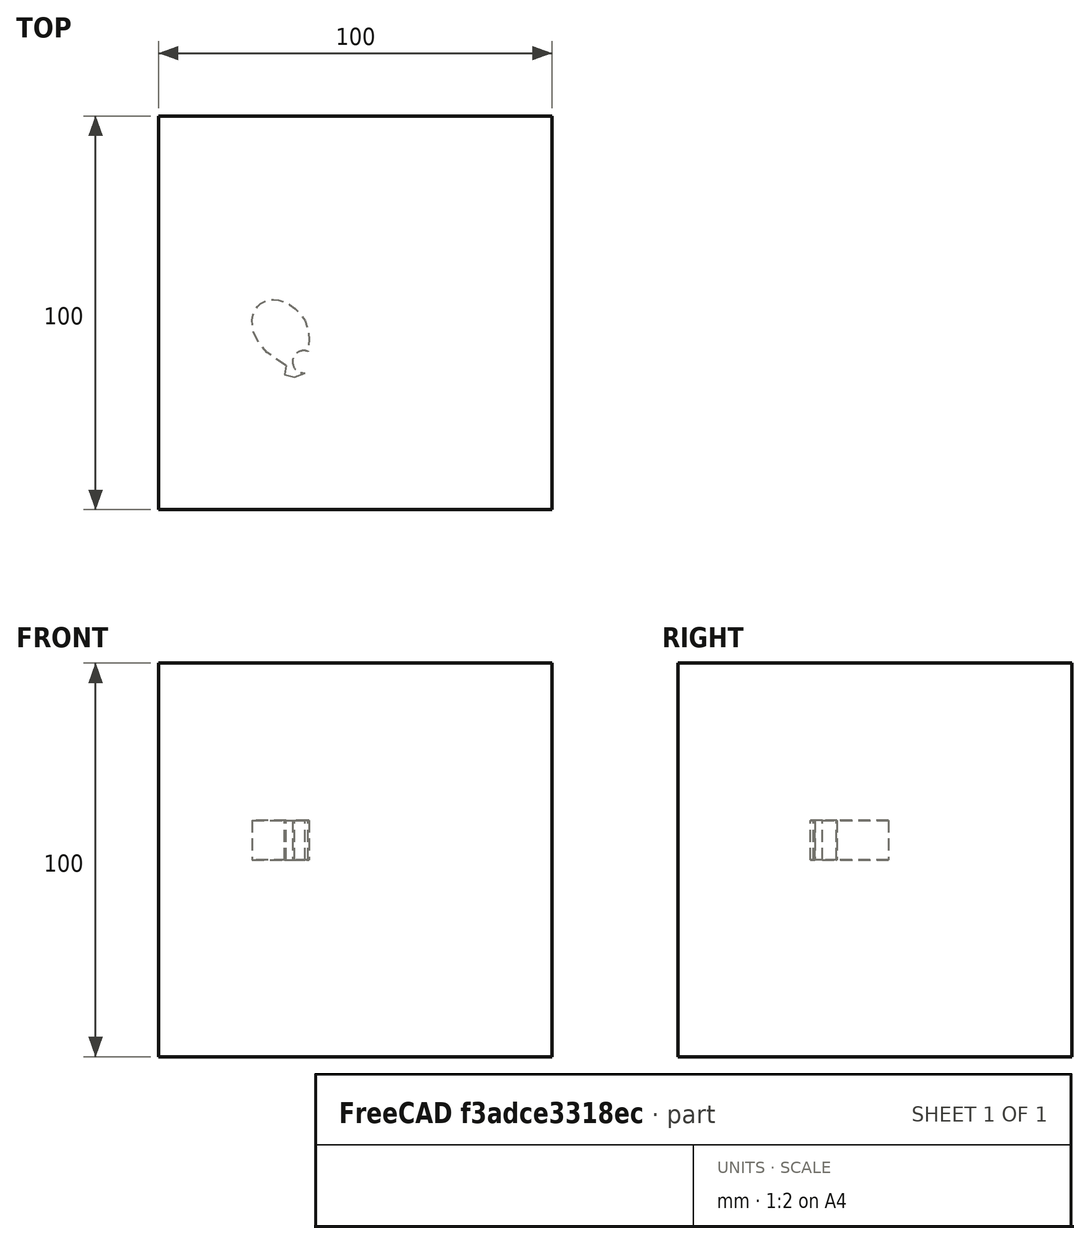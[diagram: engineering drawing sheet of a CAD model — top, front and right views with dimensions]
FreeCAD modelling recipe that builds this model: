
FCSTD DOCUMENT  (FreeCAD 0.19RUnknown)
Label: mirrorTest-3c
License: All rights reserved
LicenseURL: http://en.wikipedia.org/wiki/All_rights_reserved
objects: App::DocumentObjectGroupPython×1248, Part::Mirroring×2, App::Part×2, Part::FeaturePython×1, Sketcher::SketchObject×1, Part::Extrusion×1
note: 5 computed .brp shape members not serialized (recipe doc carries the construction recipe); baked Part::Feature solids carry a one-line shape summary decoded from their .brp

FEATURE [App::DocumentObjectGroupPython] HALFPI  # scripted group (container) (typed FeaturePython)
  name = HALFPI
  value = pi/2.
FEATURE [App::DocumentObjectGroupPython] PI  # scripted group (container) (typed FeaturePython)
  name = PI
  value = 1.*pi
FEATURE [App::DocumentObjectGroupPython] TWOPI  # scripted group (container) (typed FeaturePython)
  name = TWOPI
  value = 2.*pi
FEATURE [App::DocumentObjectGroupPython] Constants  # scripted group (container) (typed FeaturePython)
  Group = -> [HALFPI,PI,TWOPI]
FEATURE [App::DocumentObjectGroupPython] Variables  # scripted group (container) (typed FeaturePython)
FEATURE [App::DocumentObjectGroupPython] Quantities  # scripted group (container) (typed FeaturePython)
FEATURE [App::DocumentObjectGroupPython] Isotopes  # scripted group (container) (typed FeaturePython)
FEATURE [App::DocumentObjectGroupPython] Elements  # scripted group (container) (typed FeaturePython)
FEATURE [App::DocumentObjectGroupPython] G4Isotopes  # scripted group (container) (typed FeaturePython)
FEATURE [App::DocumentObjectGroupPython] H_element  # scripted group (container) (typed FeaturePython)
  Z = 1
  atom_value = 1.008
  formula = H
  name = H_element
FEATURE [App::DocumentObjectGroupPython] He_element  # scripted group (container) (typed FeaturePython)
  Z = 2
  atom_value = 4.0026
  formula = He
  name = He_element
FEATURE [App::DocumentObjectGroupPython] Li_element  # scripted group (container) (typed FeaturePython)
  Z = 3
  atom_value = 6.94
  formula = Li
  name = Li_element
FEATURE [App::DocumentObjectGroupPython] Be_element  # scripted group (container) (typed FeaturePython)
  Z = 4
  atom_value = 9.01218
  formula = Be
  name = Be_element
FEATURE [App::DocumentObjectGroupPython] B_element  # scripted group (container) (typed FeaturePython)
  Z = 5
  atom_value = 10.81
  formula = B
  name = B_element
FEATURE [App::DocumentObjectGroupPython] C_element  # scripted group (container) (typed FeaturePython)
  Z = 6
  atom_value = 12.011
  formula = C
  name = C_element
FEATURE [App::DocumentObjectGroupPython] N_element  # scripted group (container) (typed FeaturePython)
  Z = 7
  atom_value = 14.007
  formula = N
  name = N_element
FEATURE [App::DocumentObjectGroupPython] O_element  # scripted group (container) (typed FeaturePython)
  Z = 8
  atom_value = 15.999
  formula = O
  name = O_element
FEATURE [App::DocumentObjectGroupPython] F_element  # scripted group (container) (typed FeaturePython)
  Z = 9
  atom_value = 18.9984
  formula = F
  name = F_element
FEATURE [App::DocumentObjectGroupPython] Ne_element  # scripted group (container) (typed FeaturePython)
  Z = 10
  atom_value = 20.1797
  formula = Ne
  name = Ne_element
FEATURE [App::DocumentObjectGroupPython] Na_element  # scripted group (container) (typed FeaturePython)
  Z = 11
  atom_value = 22.9898
  formula = Na
  name = Na_element
FEATURE [App::DocumentObjectGroupPython] Mg_element  # scripted group (container) (typed FeaturePython)
  Z = 12
  atom_value = 24.305
  formula = Mg
  name = Mg_element
FEATURE [App::DocumentObjectGroupPython] Al_element  # scripted group (container) (typed FeaturePython)
  Z = 13
  atom_value = 26.9815
  formula = Al
  name = Al_element
FEATURE [App::DocumentObjectGroupPython] Si_element  # scripted group (container) (typed FeaturePython)
  Z = 14
  atom_value = 28.085
  formula = Si
  name = Si_element
FEATURE [App::DocumentObjectGroupPython] P_element  # scripted group (container) (typed FeaturePython)
  Z = 15
  atom_value = 30.9738
  formula = P
  name = P_element
FEATURE [App::DocumentObjectGroupPython] S_element  # scripted group (container) (typed FeaturePython)
  Z = 16
  atom_value = 32.06
  formula = S
  name = S_element
FEATURE [App::DocumentObjectGroupPython] Cl_element  # scripted group (container) (typed FeaturePython)
  Z = 17
  atom_value = 35.45
  formula = Cl
  name = Cl_element
FEATURE [App::DocumentObjectGroupPython] Ar_element  # scripted group (container) (typed FeaturePython)
  Z = 18
  atom_value = 39.95
  formula = Ar
  name = Ar_element
FEATURE [App::DocumentObjectGroupPython] K_element  # scripted group (container) (typed FeaturePython)
  Z = 19
  atom_value = 39.0983
  formula = K
  name = K_element
FEATURE [App::DocumentObjectGroupPython] Ca_element  # scripted group (container) (typed FeaturePython)
  Z = 20
  atom_value = 40.078
  formula = Ca
  name = Ca_element
FEATURE [App::DocumentObjectGroupPython] Sc_element  # scripted group (container) (typed FeaturePython)
  Z = 21
  atom_value = 44.9559
  formula = Sc
  name = Sc_element
FEATURE [App::DocumentObjectGroupPython] Ti_element  # scripted group (container) (typed FeaturePython)
  Z = 22
  atom_value = 47.867
  formula = Ti
  name = Ti_element
FEATURE [App::DocumentObjectGroupPython] V_element  # scripted group (container) (typed FeaturePython)
  Z = 23
  atom_value = 50.9415
  formula = V
  name = V_element
FEATURE [App::DocumentObjectGroupPython] Cr_element  # scripted group (container) (typed FeaturePython)
  Z = 24
  atom_value = 51.9961
  formula = Cr
  name = Cr_element
FEATURE [App::DocumentObjectGroupPython] Mn_element  # scripted group (container) (typed FeaturePython)
  Z = 25
  atom_value = 54.938
  formula = Mn
  name = Mn_element
FEATURE [App::DocumentObjectGroupPython] Fe_element  # scripted group (container) (typed FeaturePython)
  Z = 26
  atom_value = 55.845
  formula = Fe
  name = Fe_element
FEATURE [App::DocumentObjectGroupPython] Co_element  # scripted group (container) (typed FeaturePython)
  Z = 27
  atom_value = 58.9332
  formula = Co
  name = Co_element
FEATURE [App::DocumentObjectGroupPython] Ni_element  # scripted group (container) (typed FeaturePython)
  Z = 28
  atom_value = 58.6934
  formula = Ni
  name = Ni_element
FEATURE [App::DocumentObjectGroupPython] Cu_element  # scripted group (container) (typed FeaturePython)
  Z = 29
  atom_value = 63.546
  formula = Cu
  name = Cu_element
FEATURE [App::DocumentObjectGroupPython] Zn_element  # scripted group (container) (typed FeaturePython)
  Z = 30
  atom_value = 65.38
  formula = Zn
  name = Zn_element
FEATURE [App::DocumentObjectGroupPython] Ga_element  # scripted group (container) (typed FeaturePython)
  Z = 31
  atom_value = 69.723
  formula = Ga
  name = Ga_element
FEATURE [App::DocumentObjectGroupPython] Ge_element  # scripted group (container) (typed FeaturePython)
  Z = 32
  atom_value = 72.63
  formula = Ge
  name = Ge_element
FEATURE [App::DocumentObjectGroupPython] As_element  # scripted group (container) (typed FeaturePython)
  Z = 33
  atom_value = 74.9216
  formula = As
  name = As_element
FEATURE [App::DocumentObjectGroupPython] Se_element  # scripted group (container) (typed FeaturePython)
  Z = 34
  atom_value = 78.971
  formula = Se
  name = Se_element
FEATURE [App::DocumentObjectGroupPython] Br_element  # scripted group (container) (typed FeaturePython)
  Z = 35
  atom_value = 79.904
  formula = Br
  name = Br_element
FEATURE [App::DocumentObjectGroupPython] Kr_element  # scripted group (container) (typed FeaturePython)
  Z = 36
  atom_value = 83.798
  formula = Kr
  name = Kr_element
FEATURE [App::DocumentObjectGroupPython] Rb_element  # scripted group (container) (typed FeaturePython)
  Z = 37
  atom_value = 85.4678
  formula = Rb
  name = Rb_element
FEATURE [App::DocumentObjectGroupPython] Sr_element  # scripted group (container) (typed FeaturePython)
  Z = 38
  atom_value = 87.62
  formula = Sr
  name = Sr_element
FEATURE [App::DocumentObjectGroupPython] Y_element  # scripted group (container) (typed FeaturePython)
  Z = 39
  atom_value = 88.9058
  formula = Y
  name = Y_element
FEATURE [App::DocumentObjectGroupPython] Zr_element  # scripted group (container) (typed FeaturePython)
  Z = 40
  atom_value = 91.224
  formula = Zr
  name = Zr_element
FEATURE [App::DocumentObjectGroupPython] Nb_element  # scripted group (container) (typed FeaturePython)
  Z = 41
  atom_value = 92.9064
  formula = Nb
  name = Nb_element
FEATURE [App::DocumentObjectGroupPython] Mo_element  # scripted group (container) (typed FeaturePython)
  Z = 42
  atom_value = 95.95
  formula = Mo
  name = Mo_element
FEATURE [App::DocumentObjectGroupPython] Tc_element  # scripted group (container) (typed FeaturePython)
  Z = 43
  atom_value = 97
  formula = Tc
  name = Tc_element
FEATURE [App::DocumentObjectGroupPython] Ru_element  # scripted group (container) (typed FeaturePython)
  Z = 44
  atom_value = 101.07
  formula = Ru
  name = Ru_element
FEATURE [App::DocumentObjectGroupPython] Rh_element  # scripted group (container) (typed FeaturePython)
  Z = 45
  atom_value = 102.905
  formula = Rh
  name = Rh_element
FEATURE [App::DocumentObjectGroupPython] Pd_element  # scripted group (container) (typed FeaturePython)
  Z = 46
  atom_value = 106.42
  formula = Pd
  name = Pd_element
FEATURE [App::DocumentObjectGroupPython] Ag_element  # scripted group (container) (typed FeaturePython)
  Z = 47
  atom_value = 107.868
  formula = Ag
  name = Ag_element
FEATURE [App::DocumentObjectGroupPython] Cd_element  # scripted group (container) (typed FeaturePython)
  Z = 48
  atom_value = 112.414
  formula = Cd
  name = Cd_element
FEATURE [App::DocumentObjectGroupPython] In_element  # scripted group (container) (typed FeaturePython)
  Z = 49
  atom_value = 114.818
  formula = In
  name = In_element
FEATURE [App::DocumentObjectGroupPython] Sn_element  # scripted group (container) (typed FeaturePython)
  Z = 50
  atom_value = 118.71
  formula = Sn
  name = Sn_element
FEATURE [App::DocumentObjectGroupPython] Sb_element  # scripted group (container) (typed FeaturePython)
  Z = 51
  atom_value = 121.76
  formula = Sb
  name = Sb_element
FEATURE [App::DocumentObjectGroupPython] Te_element  # scripted group (container) (typed FeaturePython)
  Z = 52
  atom_value = 127.6
  formula = Te
  name = Te_element
FEATURE [App::DocumentObjectGroupPython] I_element  # scripted group (container) (typed FeaturePython)
  Z = 53
  atom_value = 126.904
  formula = I
  name = I_element
FEATURE [App::DocumentObjectGroupPython] Xe_element  # scripted group (container) (typed FeaturePython)
  Z = 54
  atom_value = 131.293
  formula = Xe
  name = Xe_element
FEATURE [App::DocumentObjectGroupPython] Cs_element  # scripted group (container) (typed FeaturePython)
  Z = 55
  atom_value = 132.905
  formula = Cs
  name = Cs_element
FEATURE [App::DocumentObjectGroupPython] Ba_element  # scripted group (container) (typed FeaturePython)
  Z = 56
  atom_value = 137.327
  formula = Ba
  name = Ba_element
FEATURE [App::DocumentObjectGroupPython] La_element  # scripted group (container) (typed FeaturePython)
  Z = 57
  atom_value = 138.905
  formula = La
  name = La_element
FEATURE [App::DocumentObjectGroupPython] Ce_element  # scripted group (container) (typed FeaturePython)
  Z = 58
  atom_value = 140.116
  formula = Ce
  name = Ce_element
FEATURE [App::DocumentObjectGroupPython] Pr_element  # scripted group (container) (typed FeaturePython)
  Z = 59
  atom_value = 140.908
  formula = Pr
  name = Pr_element
FEATURE [App::DocumentObjectGroupPython] Nd_element  # scripted group (container) (typed FeaturePython)
  Z = 60
  atom_value = 144.242
  formula = Nd
  name = Nd_element
FEATURE [App::DocumentObjectGroupPython] Pm_element  # scripted group (container) (typed FeaturePython)
  Z = 61
  atom_value = 145
  formula = Pm
  name = Pm_element
FEATURE [App::DocumentObjectGroupPython] Sm_element  # scripted group (container) (typed FeaturePython)
  Z = 62
  atom_value = 150.36
  formula = Sm
  name = Sm_element
FEATURE [App::DocumentObjectGroupPython] Eu_element  # scripted group (container) (typed FeaturePython)
  Z = 63
  atom_value = 151.964
  formula = Eu
  name = Eu_element
FEATURE [App::DocumentObjectGroupPython] Gd_element  # scripted group (container) (typed FeaturePython)
  Z = 64
  atom_value = 157.25
  formula = Gd
  name = Gd_element
FEATURE [App::DocumentObjectGroupPython] Tb_element  # scripted group (container) (typed FeaturePython)
  Z = 65
  atom_value = 158.925
  formula = Tb
  name = Tb_element
FEATURE [App::DocumentObjectGroupPython] Dy_element  # scripted group (container) (typed FeaturePython)
  Z = 66
  atom_value = 162.5
  formula = Dy
  name = Dy_element
FEATURE [App::DocumentObjectGroupPython] Ho_element  # scripted group (container) (typed FeaturePython)
  Z = 67
  atom_value = 164.93
  formula = Ho
  name = Ho_element
FEATURE [App::DocumentObjectGroupPython] Er_element  # scripted group (container) (typed FeaturePython)
  Z = 68
  atom_value = 167.259
  formula = Er
  name = Er_element
FEATURE [App::DocumentObjectGroupPython] Tm_element  # scripted group (container) (typed FeaturePython)
  Z = 69
  atom_value = 168.934
  formula = Tm
  name = Tm_element
FEATURE [App::DocumentObjectGroupPython] Yb_element  # scripted group (container) (typed FeaturePython)
  Z = 70
  atom_value = 173.045
  formula = Yb
  name = Yb_element
FEATURE [App::DocumentObjectGroupPython] Lu_element  # scripted group (container) (typed FeaturePython)
  Z = 71
  atom_value = 174.967
  formula = Lu
  name = Lu_element
FEATURE [App::DocumentObjectGroupPython] Hf_element  # scripted group (container) (typed FeaturePython)
  Z = 72
  atom_value = 178.49
  formula = Hf
  name = Hf_element
FEATURE [App::DocumentObjectGroupPython] Ta_element  # scripted group (container) (typed FeaturePython)
  Z = 73
  atom_value = 180.948
  formula = Ta
  name = Ta_element
FEATURE [App::DocumentObjectGroupPython] W_element  # scripted group (container) (typed FeaturePython)
  Z = 74
  atom_value = 183.84
  formula = W
  name = W_element
FEATURE [App::DocumentObjectGroupPython] Re_element  # scripted group (container) (typed FeaturePython)
  Z = 75
  atom_value = 186.207
  formula = Re
  name = Re_element
FEATURE [App::DocumentObjectGroupPython] Os_element  # scripted group (container) (typed FeaturePython)
  Z = 76
  atom_value = 190.23
  formula = Os
  name = Os_element
FEATURE [App::DocumentObjectGroupPython] Ir_element  # scripted group (container) (typed FeaturePython)
  Z = 77
  atom_value = 192.217
  formula = Ir
  name = Ir_element
FEATURE [App::DocumentObjectGroupPython] Pt_element  # scripted group (container) (typed FeaturePython)
  Z = 78
  atom_value = 195.084
  formula = Pt
  name = Pt_element
FEATURE [App::DocumentObjectGroupPython] Au_element  # scripted group (container) (typed FeaturePython)
  Z = 79
  atom_value = 196.967
  formula = Au
  name = Au_element
FEATURE [App::DocumentObjectGroupPython] Hg_element  # scripted group (container) (typed FeaturePython)
  Z = 80
  atom_value = 200.592
  formula = Hg
  name = Hg_element
FEATURE [App::DocumentObjectGroupPython] Tl_element  # scripted group (container) (typed FeaturePython)
  Z = 81
  atom_value = 204.38
  formula = Tl
  name = Tl_element
FEATURE [App::DocumentObjectGroupPython] Pb_element  # scripted group (container) (typed FeaturePython)
  Z = 82
  atom_value = 207.2
  formula = Pb
  name = Pb_element
FEATURE [App::DocumentObjectGroupPython] Bi_element  # scripted group (container) (typed FeaturePython)
  Z = 83
  atom_value = 208.98
  formula = Bi
  name = Bi_element
FEATURE [App::DocumentObjectGroupPython] Po_element  # scripted group (container) (typed FeaturePython)
  Z = 84
  atom_value = 209
  formula = Po
  name = Po_element
FEATURE [App::DocumentObjectGroupPython] At_element  # scripted group (container) (typed FeaturePython)
  Z = 85
  atom_value = 210
  formula = At
  name = At_element
FEATURE [App::DocumentObjectGroupPython] Rn_element  # scripted group (container) (typed FeaturePython)
  Z = 86
  atom_value = 222
  formula = Rn
  name = Rn_element
FEATURE [App::DocumentObjectGroupPython] Fr_element  # scripted group (container) (typed FeaturePython)
  Z = 87
  atom_value = 223
  formula = Fr
  name = Fr_element
FEATURE [App::DocumentObjectGroupPython] Ra_element  # scripted group (container) (typed FeaturePython)
  Z = 88
  atom_value = 226
  formula = Ra
  name = Ra_element
FEATURE [App::DocumentObjectGroupPython] Ac_element  # scripted group (container) (typed FeaturePython)
  Z = 89
  atom_value = 227
  formula = Ac
  name = Ac_element
FEATURE [App::DocumentObjectGroupPython] Th_element  # scripted group (container) (typed FeaturePython)
  Z = 90
  atom_value = 232.038
  formula = Th
  name = Th_element
FEATURE [App::DocumentObjectGroupPython] Pa_element  # scripted group (container) (typed FeaturePython)
  Z = 91
  atom_value = 231.036
  formula = Pa
  name = Pa_element
FEATURE [App::DocumentObjectGroupPython] U_element  # scripted group (container) (typed FeaturePython)
  Z = 92
  atom_value = 238.029
  formula = U
  name = U_element
FEATURE [App::DocumentObjectGroupPython] Np_element  # scripted group (container) (typed FeaturePython)
  Z = 93
  atom_value = 237
  formula = Np
  name = Np_element
FEATURE [App::DocumentObjectGroupPython] Pu_element  # scripted group (container) (typed FeaturePython)
  Z = 94
  atom_value = 244
  formula = Pu
  name = Pu_element
FEATURE [App::DocumentObjectGroupPython] Am_element  # scripted group (container) (typed FeaturePython)
  Z = 95
  atom_value = 243
  formula = Am
  name = Am_element
FEATURE [App::DocumentObjectGroupPython] Cm_element  # scripted group (container) (typed FeaturePython)
  Z = 96
  atom_value = 247
  formula = Cm
  name = Cm_element
FEATURE [App::DocumentObjectGroupPython] Bk_element  # scripted group (container) (typed FeaturePython)
  Z = 97
  atom_value = 247
  formula = Bk
  name = Bk_element
FEATURE [App::DocumentObjectGroupPython] Cf_element  # scripted group (container) (typed FeaturePython)
  Z = 98
  atom_value = 251
  formula = Cf
  name = Cf_element
FEATURE [App::DocumentObjectGroupPython] G4Elements  # scripted group (container) (typed FeaturePython)
  Group = -> [H_element,He_element,Li_element,Be_element,B_element,C_element,N_element,O_element,F_element,Ne_element,Na_element,Mg_element,Al_element,Si_element,P_element,S_element,Cl_element,Ar_element,K_element,Ca_element,Sc_element,Ti_element,V_element,Cr_element,Mn_element,Fe_element,Co_element,Ni_element,Cu_element,Zn_element,Ga_element,Ge_element,As_element,Se_element,Br_element,Kr_element,Rb_element,+61 more]
FEATURE [App::DocumentObjectGroupPython] H_element001  label="H_element : 0.101"  # scripted group (container) (typed FeaturePython)
  n = 0.101327
FEATURE [App::DocumentObjectGroupPython] C_element001  label="C_element : 0.775"  # scripted group (container) (typed FeaturePython)
  n = 0.7755
FEATURE [App::DocumentObjectGroupPython] N_element001  label="N_element : 0.035"  # scripted group (container) (typed FeaturePython)
  n = 0.035057
FEATURE [App::DocumentObjectGroupPython] O_element001  label="O_element : 0.052"  # scripted group (container) (typed FeaturePython)
  n = 0.0523159
FEATURE [App::DocumentObjectGroupPython] F_element001  label="F_element : 0.017"  # scripted group (container) (typed FeaturePython)
  n = 0.017422
FEATURE [App::DocumentObjectGroupPython] Ca_element001  label="Ca_element : 0.018"  # scripted group (container) (typed FeaturePython)
  n = 0.018378
FEATURE [App::DocumentObjectGroupPython] G4_A_150_TISSUE  label="G4_A-150_TISSUE"  # scripted group (container) (typed FeaturePython)
  Dunit = g/cm3
  Dvalue = 1.127
  Group = -> [H_element001,C_element001,N_element001,O_element001,F_element001,Ca_element001]
  conduct = 2
  density = 1
  expand = 3
  formula = G4_A-150_TISSUE
  name = G4_A-150_TISSUE
  specific = 4
FEATURE [App::DocumentObjectGroupPython] C_element002  label="C_element : 3"  # scripted group (container) (typed FeaturePython)
  n = 3
  ref = C_element
FEATURE [App::DocumentObjectGroupPython] H_element002  label="H_element : 6"  # scripted group (container) (typed FeaturePython)
  n = 6
  ref = H_element
FEATURE [App::DocumentObjectGroupPython] O_element002  label="O_element : 1"  # scripted group (container) (typed FeaturePython)
  n = 1
  ref = O_element
FEATURE [App::DocumentObjectGroupPython] G4_ACETONE  # scripted group (container) (typed FeaturePython)
  Dunit = g/cm3
  Dvalue = 0.7899
  Group = -> [C_element002,H_element002,O_element002]
  conduct = 2
  density = 1
  expand = 3
  formula = G4_ACETONE
  name = G4_ACETONE
  specific = 4
FEATURE [App::DocumentObjectGroupPython] C_element003  label="C_element : 2"  # scripted group (container) (typed FeaturePython)
  n = 2
  ref = C_element
FEATURE [App::DocumentObjectGroupPython] H_element003  label="H_element : 2"  # scripted group (container) (typed FeaturePython)
  n = 2
  ref = H_element
FEATURE [App::DocumentObjectGroupPython] G4_ACETYLENE  # scripted group (container) (typed FeaturePython)
  Dunit = g/cm3
  Dvalue = 0.0010967
  Group = -> [C_element003,H_element003]
  conduct = 2
  density = 1
  expand = 3
  formula = G4_ACETYLENE
  name = G4_ACETYLENE
  specific = 4
FEATURE [App::DocumentObjectGroupPython] C_element004  label="C_element : 5"  # scripted group (container) (typed FeaturePython)
  n = 5
  ref = C_element
FEATURE [App::DocumentObjectGroupPython] H_element004  label="H_element : 5"  # scripted group (container) (typed FeaturePython)
  n = 5
  ref = H_element
FEATURE [App::DocumentObjectGroupPython] N_element002  label="N_element : 5"  # scripted group (container) (typed FeaturePython)
  n = 5
  ref = N_element
FEATURE [App::DocumentObjectGroupPython] G4_ADENINE  # scripted group (container) (typed FeaturePython)
  Dunit = g/cm3
  Dvalue = 1.6
  Group = -> [C_element004,H_element004,N_element002]
  conduct = 2
  density = 1
  expand = 3
  formula = G4_ADENINE
  name = G4_ADENINE
  specific = 4
FEATURE [App::DocumentObjectGroupPython] H_element005  label="H_element : 0.114"  # scripted group (container) (typed FeaturePython)
  n = 0.114
FEATURE [App::DocumentObjectGroupPython] C_element005  label="C_element : 0.598"  # scripted group (container) (typed FeaturePython)
  n = 0.598
FEATURE [App::DocumentObjectGroupPython] N_element003  label="N_element : 0.007"  # scripted group (container) (typed FeaturePython)
  n = 0.007
FEATURE [App::DocumentObjectGroupPython] O_element003  label="O_element : 0.278"  # scripted group (container) (typed FeaturePython)
  n = 0.278
FEATURE [App::DocumentObjectGroupPython] Na_element001  label="Na_element : 0.001"  # scripted group (container) (typed FeaturePython)
  n = 0.001
FEATURE [App::DocumentObjectGroupPython] S_element001  label="S_element : 0.001"  # scripted group (container) (typed FeaturePython)
  n = 0.001
FEATURE [App::DocumentObjectGroupPython] Cl_element001  label="Cl_element : 0.001"  # scripted group (container) (typed FeaturePython)
  n = 0.001
FEATURE [App::DocumentObjectGroupPython] G4_ADIPOSE_TISSUE_ICRP  # scripted group (container) (typed FeaturePython)
  Dunit = g/cm3
  Dvalue = 0.95
  Group = -> [H_element005,C_element005,N_element003,O_element003,Na_element001,S_element001,Cl_element001]
  conduct = 2
  density = 1
  expand = 3
  formula = G4_ADIPOSE_TISSUE_ICRP
  name = G4_ADIPOSE_TISSUE_ICRP
  specific = 4
FEATURE [App::DocumentObjectGroupPython] C_element006  label="C_element : 0.000"  # scripted group (container) (typed FeaturePython)
  n = 0.000124
FEATURE [App::DocumentObjectGroupPython] N_element004  label="N_element : 0.755"  # scripted group (container) (typed FeaturePython)
  n = 0.755268
FEATURE [App::DocumentObjectGroupPython] O_element004  label="O_element : 0.232"  # scripted group (container) (typed FeaturePython)
  n = 0.231781
FEATURE [App::DocumentObjectGroupPython] Ar_element001  label="Ar_element : 0.013"  # scripted group (container) (typed FeaturePython)
  n = 0.012827
FEATURE [App::DocumentObjectGroupPython] G4_AIR  # scripted group (container) (typed FeaturePython)
  Dunit = g/cm3
  Dvalue = 0.00120479
  Group = -> [C_element006,N_element004,O_element004,Ar_element001]
  conduct = 2
  density = 1
  expand = 3
  formula = G4_AIR
  name = G4_AIR
  specific = 4
FEATURE [App::DocumentObjectGroupPython] C_element007  label="C_element : 006"  # scripted group (container) (typed FeaturePython)
  n = 3
  ref = C_element
FEATURE [App::DocumentObjectGroupPython] H_element006  label="H_element : 7"  # scripted group (container) (typed FeaturePython)
  n = 7
  ref = H_element
FEATURE [App::DocumentObjectGroupPython] N_element005  label="N_element : 1"  # scripted group (container) (typed FeaturePython)
  n = 1
  ref = N_element
FEATURE [App::DocumentObjectGroupPython] O_element005  label="O_element : 2"  # scripted group (container) (typed FeaturePython)
  n = 2
  ref = O_element
FEATURE [App::DocumentObjectGroupPython] G4_ALANINE  # scripted group (container) (typed FeaturePython)
  Dunit = g/cm3
  Dvalue = 1.42
  Group = -> [C_element007,H_element006,N_element005,O_element005]
  conduct = 2
  density = 1
  expand = 3
  formula = G4_ALANINE
  name = G4_ALANINE
  specific = 4
FEATURE [App::DocumentObjectGroupPython] Al_element001  label="Al_element : 2"  # scripted group (container) (typed FeaturePython)
  n = 2
  ref = Al_element
FEATURE [App::DocumentObjectGroupPython] O_element006  label="O_element : 3"  # scripted group (container) (typed FeaturePython)
  n = 3
  ref = O_element
FEATURE [App::DocumentObjectGroupPython] G4_ALUMINUM_OXIDE  # scripted group (container) (typed FeaturePython)
  Dunit = g/cm3
  Dvalue = 3.97
  Group = -> [Al_element001,O_element006]
  conduct = 2
  density = 1
  expand = 3
  formula = G4_ALUMINUM_OXIDE
  name = G4_ALUMINUM_OXIDE
  specific = 4
FEATURE [App::DocumentObjectGroupPython] H_element007  label="H_element : 0.106"  # scripted group (container) (typed FeaturePython)
  n = 0.10593
FEATURE [App::DocumentObjectGroupPython] C_element008  label="C_element : 0.789"  # scripted group (container) (typed FeaturePython)
  n = 0.788974
FEATURE [App::DocumentObjectGroupPython] O_element007  label="O_element : 0.105"  # scripted group (container) (typed FeaturePython)
  n = 0.105096
FEATURE [App::DocumentObjectGroupPython] G4_AMBER  # scripted group (container) (typed FeaturePython)
  Dunit = g/cm3
  Dvalue = 1.1
  Group = -> [H_element007,C_element008,O_element007]
  conduct = 2
  density = 1
  expand = 3
  formula = G4_AMBER
  name = G4_AMBER
  specific = 4
FEATURE [App::DocumentObjectGroupPython] N_element006  label="N_element : 006"  # scripted group (container) (typed FeaturePython)
  n = 1
  ref = N_element
FEATURE [App::DocumentObjectGroupPython] H_element008  label="H_element : 3"  # scripted group (container) (typed FeaturePython)
  n = 3
  ref = H_element
FEATURE [App::DocumentObjectGroupPython] G4_AMMONIA  # scripted group (container) (typed FeaturePython)
  Dunit = g/cm3
  Dvalue = 0.000826019
  Group = -> [N_element006,H_element008]
  conduct = 2
  density = 1
  expand = 3
  formula = G4_AMMONIA
  name = G4_AMMONIA
  specific = 4
FEATURE [App::DocumentObjectGroupPython] C_element009  label="C_element : 6"  # scripted group (container) (typed FeaturePython)
  n = 6
  ref = C_element
FEATURE [App::DocumentObjectGroupPython] H_element009  label="H_element : 008"  # scripted group (container) (typed FeaturePython)
  n = 7
  ref = H_element
FEATURE [App::DocumentObjectGroupPython] N_element007  label="N_element : 007"  # scripted group (container) (typed FeaturePython)
  n = 1
  ref = N_element
FEATURE [App::DocumentObjectGroupPython] G4_ANILINE  # scripted group (container) (typed FeaturePython)
  Dunit = g/cm3
  Dvalue = 1.0235
  Group = -> [C_element009,H_element009,N_element007]
  conduct = 2
  density = 1
  expand = 3
  formula = G4_ANILINE
  name = G4_ANILINE
  specific = 4
FEATURE [App::DocumentObjectGroupPython] C_element010  label="C_element : 14"  # scripted group (container) (typed FeaturePython)
  n = 14
  ref = C_element
FEATURE [App::DocumentObjectGroupPython] H_element010  label="H_element : 10"  # scripted group (container) (typed FeaturePython)
  n = 10
  ref = H_element
FEATURE [App::DocumentObjectGroupPython] G4_ANTHRACENE  # scripted group (container) (typed FeaturePython)
  Dunit = g/cm3
  Dvalue = 1.283
  Group = -> [C_element010,H_element010]
  conduct = 2
  density = 1
  expand = 3
  formula = G4_ANTHRACENE
  name = G4_ANTHRACENE
  specific = 4
FEATURE [App::DocumentObjectGroupPython] H_element011  label="H_element : 0.065"  # scripted group (container) (typed FeaturePython)
  n = 0.0654709
FEATURE [App::DocumentObjectGroupPython] C_element011  label="C_element : 0.537"  # scripted group (container) (typed FeaturePython)
  n = 0.536944
FEATURE [App::DocumentObjectGroupPython] N_element008  label="N_element : 0.021"  # scripted group (container) (typed FeaturePython)
  n = 0.0215
FEATURE [App::DocumentObjectGroupPython] O_element008  label="O_element : 0.032"  # scripted group (container) (typed FeaturePython)
  n = 0.032085
FEATURE [App::DocumentObjectGroupPython] F_element002  label="F_element : 0.167"  # scripted group (container) (typed FeaturePython)
  n = 0.167411
FEATURE [App::DocumentObjectGroupPython] Ca_element002  label="Ca_element : 0.177"  # scripted group (container) (typed FeaturePython)
  n = 0.176589
FEATURE [App::DocumentObjectGroupPython] G4_B_100_BONE  label="G4_B-100_BONE"  # scripted group (container) (typed FeaturePython)
  Dunit = g/cm3
  Dvalue = 1.45
  Group = -> [H_element011,C_element011,N_element008,O_element008,F_element002,Ca_element002]
  conduct = 2
  density = 1
  expand = 3
  formula = G4_B-100_BONE
  name = G4_B-100_BONE
  specific = 4
FEATURE [App::DocumentObjectGroupPython] H_element012  label="H_element : 0.057"  # scripted group (container) (typed FeaturePython)
  n = 0.057441
FEATURE [App::DocumentObjectGroupPython] C_element012  label="C_element : 0.790"  # scripted group (container) (typed FeaturePython)
  n = 0.774591
FEATURE [App::DocumentObjectGroupPython] O_element009  label="O_element : 0.168"  # scripted group (container) (typed FeaturePython)
  n = 0.167968
FEATURE [App::DocumentObjectGroupPython] G4_BAKELITE  # scripted group (container) (typed FeaturePython)
  Dunit = g/cm3
  Dvalue = 1.25
  Group = -> [H_element012,C_element012,O_element009]
  conduct = 2
  density = 1
  expand = 3
  formula = G4_BAKELITE
  name = G4_BAKELITE
  specific = 4
FEATURE [App::DocumentObjectGroupPython] Ba_element001  label="Ba_element : 1"  # scripted group (container) (typed FeaturePython)
  n = 1
  ref = Ba_element
FEATURE [App::DocumentObjectGroupPython] F_element003  label="F_element : 2"  # scripted group (container) (typed FeaturePython)
  n = 2
  ref = F_element
FEATURE [App::DocumentObjectGroupPython] G4_BARIUM_FLUORIDE  # scripted group (container) (typed FeaturePython)
  Dunit = g/cm3
  Dvalue = 4.89
  Group = -> [Ba_element001,F_element003]
  conduct = 2
  density = 1
  expand = 3
  formula = G4_BARIUM_FLUORIDE
  name = G4_BARIUM_FLUORIDE
  specific = 4
FEATURE [App::DocumentObjectGroupPython] Ba_element002  label="Ba_element : 002"  # scripted group (container) (typed FeaturePython)
  n = 1
  ref = Ba_element
FEATURE [App::DocumentObjectGroupPython] S_element002  label="S_element : 1"  # scripted group (container) (typed FeaturePython)
  n = 1
  ref = S_element
FEATURE [App::DocumentObjectGroupPython] O_element010  label="O_element : 4"  # scripted group (container) (typed FeaturePython)
  n = 4
  ref = O_element
FEATURE [App::DocumentObjectGroupPython] G4_BARIUM_SULFATE  # scripted group (container) (typed FeaturePython)
  Dunit = g/cm3
  Dvalue = 4.5
  Group = -> [Ba_element002,S_element002,O_element010]
  conduct = 2
  density = 1
  expand = 3
  formula = G4_BARIUM_SULFATE
  name = G4_BARIUM_SULFATE
  specific = 4
FEATURE [App::DocumentObjectGroupPython] C_element013  label="C_element : 007"  # scripted group (container) (typed FeaturePython)
  n = 6
  ref = C_element
FEATURE [App::DocumentObjectGroupPython] H_element013  label="H_element : 009"  # scripted group (container) (typed FeaturePython)
  n = 6
  ref = H_element
FEATURE [App::DocumentObjectGroupPython] G4_BENZENE  # scripted group (container) (typed FeaturePython)
  Dunit = g/cm3
  Dvalue = 0.87865
  Group = -> [C_element013,H_element013]
  conduct = 2
  density = 1
  expand = 3
  formula = G4_BENZENE
  name = G4_BENZENE
  specific = 4
FEATURE [App::DocumentObjectGroupPython] Be_element001  label="Be_element : 1"  # scripted group (container) (typed FeaturePython)
  n = 1
  ref = Be_element
FEATURE [App::DocumentObjectGroupPython] O_element011  label="O_element : 005"  # scripted group (container) (typed FeaturePython)
  n = 1
  ref = O_element
FEATURE [App::DocumentObjectGroupPython] G4_BERYLLIUM_OXIDE  # scripted group (container) (typed FeaturePython)
  Dunit = g/cm3
  Dvalue = 3.01
  Group = -> [Be_element001,O_element011]
  conduct = 2
  density = 1
  expand = 3
  formula = G4_BERYLLIUM_OXIDE
  name = G4_BERYLLIUM_OXIDE
  specific = 4
FEATURE [App::DocumentObjectGroupPython] Bi_element001  label="Bi_element : 4"  # scripted group (container) (typed FeaturePython)
  n = 4
  ref = Bi_element
FEATURE [App::DocumentObjectGroupPython] Ge_element001  label="Ge_element : 3"  # scripted group (container) (typed FeaturePython)
  n = 3
  ref = Ge_element
FEATURE [App::DocumentObjectGroupPython] O_element012  label="O_element : 12"  # scripted group (container) (typed FeaturePython)
  n = 12
  ref = O_element
FEATURE [App::DocumentObjectGroupPython] G4_BGO  # scripted group (container) (typed FeaturePython)
  Dunit = g/cm3
  Dvalue = 7.13
  Group = -> [Bi_element001,Ge_element001,O_element012]
  conduct = 2
  density = 1
  expand = 3
  formula = G4_BGO
  name = G4_BGO
  specific = 4
FEATURE [App::DocumentObjectGroupPython] H_element014  label="H_element : 0.102"  # scripted group (container) (typed FeaturePython)
  n = 0.102
FEATURE [App::DocumentObjectGroupPython] C_element014  label="C_element : 0.110"  # scripted group (container) (typed FeaturePython)
  n = 0.11
FEATURE [App::DocumentObjectGroupPython] N_element009  label="N_element : 0.033"  # scripted group (container) (typed FeaturePython)
  n = 0.033
FEATURE [App::DocumentObjectGroupPython] O_element013  label="O_element : 0.745"  # scripted group (container) (typed FeaturePython)
  n = 0.745
FEATURE [App::DocumentObjectGroupPython] Na_element002  label="Na_element : 0.002"  # scripted group (container) (typed FeaturePython)
  n = 0.001
FEATURE [App::DocumentObjectGroupPython] P_element001  label="P_element : 0.001"  # scripted group (container) (typed FeaturePython)
  n = 0.001
FEATURE [App::DocumentObjectGroupPython] S_element003  label="S_element : 0.002"  # scripted group (container) (typed FeaturePython)
  n = 0.002
FEATURE [App::DocumentObjectGroupPython] Cl_element002  label="Cl_element : 0.003"  # scripted group (container) (typed FeaturePython)
  n = 0.003
FEATURE [App::DocumentObjectGroupPython] K_element001  label="K_element : 0.002"  # scripted group (container) (typed FeaturePython)
  n = 0.002
FEATURE [App::DocumentObjectGroupPython] Fe_element001  label="Fe_element : 0.001"  # scripted group (container) (typed FeaturePython)
  n = 0.001
FEATURE [App::DocumentObjectGroupPython] G4_BLOOD_ICRP  # scripted group (container) (typed FeaturePython)
  Dunit = g/cm3
  Dvalue = 1.06
  Group = -> [H_element014,C_element014,N_element009,O_element013,Na_element002,P_element001,S_element003,Cl_element002,K_element001,Fe_element001]
  conduct = 2
  density = 1
  expand = 3
  formula = G4_BLOOD_ICRP
  name = G4_BLOOD_ICRP
  specific = 4
FEATURE [App::DocumentObjectGroupPython] H_element015  label="H_element : 0.064"  # scripted group (container) (typed FeaturePython)
  n = 0.064
FEATURE [App::DocumentObjectGroupPython] C_element015  label="C_element : 0.278"  # scripted group (container) (typed FeaturePython)
  n = 0.278
FEATURE [App::DocumentObjectGroupPython] N_element010  label="N_element : 0.027"  # scripted group (container) (typed FeaturePython)
  n = 0.027
FEATURE [App::DocumentObjectGroupPython] O_element014  label="O_element : 0.410"  # scripted group (container) (typed FeaturePython)
  n = 0.41
FEATURE [App::DocumentObjectGroupPython] Mg_element001  label="Mg_element : 0.002"  # scripted group (container) (typed FeaturePython)
  n = 0.002
FEATURE [App::DocumentObjectGroupPython] P_element002  label="P_element : 0.070"  # scripted group (container) (typed FeaturePython)
  n = 0.07
FEATURE [App::DocumentObjectGroupPython] S_element004  label="S_element : 0.003"  # scripted group (container) (typed FeaturePython)
  n = 0.002
FEATURE [App::DocumentObjectGroupPython] Ca_element003  label="Ca_element : 0.147"  # scripted group (container) (typed FeaturePython)
  n = 0.147
FEATURE [App::DocumentObjectGroupPython] G4_BONE_COMPACT_ICRU  # scripted group (container) (typed FeaturePython)
  Dunit = g/cm3
  Dvalue = 1.85
  Group = -> [H_element015,C_element015,N_element010,O_element014,Mg_element001,P_element002,S_element004,Ca_element003]
  conduct = 2
  density = 1
  expand = 3
  formula = G4_BONE_COMPACT_ICRU
  name = G4_BONE_COMPACT_ICRU
  specific = 4
FEATURE [App::DocumentObjectGroupPython] H_element016  label="H_element : 0.034"  # scripted group (container) (typed FeaturePython)
  n = 0.034
FEATURE [App::DocumentObjectGroupPython] C_element016  label="C_element : 0.155"  # scripted group (container) (typed FeaturePython)
  n = 0.155
FEATURE [App::DocumentObjectGroupPython] N_element011  label="N_element : 0.042"  # scripted group (container) (typed FeaturePython)
  n = 0.042
FEATURE [App::DocumentObjectGroupPython] O_element015  label="O_element : 0.435"  # scripted group (container) (typed FeaturePython)
  n = 0.435
FEATURE [App::DocumentObjectGroupPython] Na_element003  label="Na_element : 0.003"  # scripted group (container) (typed FeaturePython)
  n = 0.001
FEATURE [App::DocumentObjectGroupPython] Mg_element002  label="Mg_element : 0.003"  # scripted group (container) (typed FeaturePython)
  n = 0.002
FEATURE [App::DocumentObjectGroupPython] P_element003  label="P_element : 0.103"  # scripted group (container) (typed FeaturePython)
  n = 0.103
FEATURE [App::DocumentObjectGroupPython] S_element005  label="S_element : 0.004"  # scripted group (container) (typed FeaturePython)
  n = 0.003
FEATURE [App::DocumentObjectGroupPython] Ca_element004  label="Ca_element : 0.225"  # scripted group (container) (typed FeaturePython)
  n = 0.225
FEATURE [App::DocumentObjectGroupPython] G4_BONE_CORTICAL_ICRP  # scripted group (container) (typed FeaturePython)
  Dunit = g/cm3
  Dvalue = 1.92
  Group = -> [H_element016,C_element016,N_element011,O_element015,Na_element003,Mg_element002,P_element003,S_element005,Ca_element004]
  conduct = 2
  density = 1
  expand = 3
  formula = G4_BONE_CORTICAL_ICRP
  name = G4_BONE_CORTICAL_ICRP
  specific = 4
FEATURE [App::DocumentObjectGroupPython] B_element001  label="B_element : 4"  # scripted group (container) (typed FeaturePython)
  n = 4
  ref = B_element
FEATURE [App::DocumentObjectGroupPython] C_element017  label="C_element : 1"  # scripted group (container) (typed FeaturePython)
  n = 1
  ref = C_element
FEATURE [App::DocumentObjectGroupPython] G4_BORON_CARBIDE  # scripted group (container) (typed FeaturePython)
  Dunit = g/cm3
  Dvalue = 2.52
  Group = -> [B_element001,C_element017]
  conduct = 2
  density = 1
  expand = 3
  formula = G4_BORON_CARBIDE
  name = G4_BORON_CARBIDE
  specific = 4
FEATURE [App::DocumentObjectGroupPython] B_element002  label="B_element : 2"  # scripted group (container) (typed FeaturePython)
  n = 2
  ref = B_element
FEATURE [App::DocumentObjectGroupPython] O_element016  label="O_element : 006"  # scripted group (container) (typed FeaturePython)
  n = 3
  ref = O_element
FEATURE [App::DocumentObjectGroupPython] G4_BORON_OXIDE  # scripted group (container) (typed FeaturePython)
  Dunit = g/cm3
  Dvalue = 1.812
  Group = -> [B_element002,O_element016]
  conduct = 2
  density = 1
  expand = 3
  formula = G4_BORON_OXIDE
  name = G4_BORON_OXIDE
  specific = 4
FEATURE [App::DocumentObjectGroupPython] H_element017  label="H_element : 0.107"  # scripted group (container) (typed FeaturePython)
  n = 0.107
FEATURE [App::DocumentObjectGroupPython] C_element018  label="C_element : 0.145"  # scripted group (container) (typed FeaturePython)
  n = 0.145
FEATURE [App::DocumentObjectGroupPython] N_element012  label="N_element : 0.022"  # scripted group (container) (typed FeaturePython)
  n = 0.022
FEATURE [App::DocumentObjectGroupPython] O_element017  label="O_element : 0.712"  # scripted group (container) (typed FeaturePython)
  n = 0.712
FEATURE [App::DocumentObjectGroupPython] Na_element004  label="Na_element : 0.004"  # scripted group (container) (typed FeaturePython)
  n = 0.002
FEATURE [App::DocumentObjectGroupPython] P_element004  label="P_element : 0.004"  # scripted group (container) (typed FeaturePython)
  n = 0.004
FEATURE [App::DocumentObjectGroupPython] S_element006  label="S_element : 0.005"  # scripted group (container) (typed FeaturePython)
  n = 0.002
FEATURE [App::DocumentObjectGroupPython] Cl_element003  label="Cl_element : 0.004"  # scripted group (container) (typed FeaturePython)
  n = 0.003
FEATURE [App::DocumentObjectGroupPython] K_element002  label="K_element : 0.003"  # scripted group (container) (typed FeaturePython)
  n = 0.003
FEATURE [App::DocumentObjectGroupPython] G4_BRAIN_ICRP  # scripted group (container) (typed FeaturePython)
  Dunit = g/cm3
  Dvalue = 1.04
  Group = -> [H_element017,C_element018,N_element012,O_element017,Na_element004,P_element004,S_element006,Cl_element003,K_element002]
  conduct = 2
  density = 1
  expand = 3
  formula = G4_BRAIN_ICRP
  name = G4_BRAIN_ICRP
  specific = 4
FEATURE [App::DocumentObjectGroupPython] C_element019  label="C_element : 4"  # scripted group (container) (typed FeaturePython)
  n = 4
  ref = C_element
FEATURE [App::DocumentObjectGroupPython] H_element018  label="H_element : 010"  # scripted group (container) (typed FeaturePython)
  n = 10
  ref = H_element
FEATURE [App::DocumentObjectGroupPython] G4_BUTANE  # scripted group (container) (typed FeaturePython)
  Dunit = g/cm3
  Dvalue = 0.00249343
  Group = -> [C_element019,H_element018]
  conduct = 2
  density = 1
  expand = 3
  formula = G4_BUTANE
  name = G4_BUTANE
  specific = 4
FEATURE [App::DocumentObjectGroupPython] C_element020  label="C_element : 008"  # scripted group (container) (typed FeaturePython)
  n = 4
  ref = C_element
FEATURE [App::DocumentObjectGroupPython] H_element019  label="H_element : 011"  # scripted group (container) (typed FeaturePython)
  n = 10
  ref = H_element
FEATURE [App::DocumentObjectGroupPython] O_element018  label="O_element : 007"  # scripted group (container) (typed FeaturePython)
  n = 1
  ref = O_element
FEATURE [App::DocumentObjectGroupPython] G4_N_BUTYL_ALCOHOL  label="G4_N-BUTYL_ALCOHOL"  # scripted group (container) (typed FeaturePython)
  Dunit = g/cm3
  Dvalue = 0.8098
  Group = -> [C_element020,H_element019,O_element018]
  conduct = 2
  density = 1
  expand = 3
  formula = G4_N-BUTYL_ALCOHOL
  name = G4_N-BUTYL_ALCOHOL
  specific = 4
FEATURE [App::DocumentObjectGroupPython] H_element020  label="H_element : 0.025"  # scripted group (container) (typed FeaturePython)
  n = 0.02468
FEATURE [App::DocumentObjectGroupPython] C_element021  label="C_element : 0.502"  # scripted group (container) (typed FeaturePython)
  n = 0.501611
FEATURE [App::DocumentObjectGroupPython] O_element019  label="O_element : 0.005"  # scripted group (container) (typed FeaturePython)
  n = 0.004527
FEATURE [App::DocumentObjectGroupPython] F_element004  label="F_element : 0.465"  # scripted group (container) (typed FeaturePython)
  n = 0.465209
FEATURE [App::DocumentObjectGroupPython] Si_element001  label="Si_element : 0.004"  # scripted group (container) (typed FeaturePython)
  n = 0.003973
FEATURE [App::DocumentObjectGroupPython] G4_C_552  label="G4_C-552"  # scripted group (container) (typed FeaturePython)
  Dunit = g/cm3
  Dvalue = 1.76
  Group = -> [H_element020,C_element021,O_element019,F_element004,Si_element001]
  conduct = 2
  density = 1
  expand = 3
  formula = G4_C-552
  name = G4_C-552
  specific = 4
FEATURE [App::DocumentObjectGroupPython] Cd_element001  label="Cd_element : 1"  # scripted group (container) (typed FeaturePython)
  n = 1
  ref = Cd_element
FEATURE [App::DocumentObjectGroupPython] Te_element001  label="Te_element : 1"  # scripted group (container) (typed FeaturePython)
  n = 1
  ref = Te_element
FEATURE [App::DocumentObjectGroupPython] G4_CADMIUM_TELLURIDE  # scripted group (container) (typed FeaturePython)
  Dunit = g/cm3
  Dvalue = 6.2
  Group = -> [Cd_element001,Te_element001]
  conduct = 2
  density = 1
  expand = 3
  formula = G4_CADMIUM_TELLURIDE
  name = G4_CADMIUM_TELLURIDE
  specific = 4
FEATURE [App::DocumentObjectGroupPython] Cd_element002  label="Cd_element : 002"  # scripted group (container) (typed FeaturePython)
  n = 1
  ref = Cd_element
FEATURE [App::DocumentObjectGroupPython] W_element001  label="W_element : 1"  # scripted group (container) (typed FeaturePython)
  n = 1
  ref = W_element
FEATURE [App::DocumentObjectGroupPython] O_element020  label="O_element : 008"  # scripted group (container) (typed FeaturePython)
  n = 4
  ref = O_element
FEATURE [App::DocumentObjectGroupPython] G4_CADMIUM_TUNGSTATE  # scripted group (container) (typed FeaturePython)
  Dunit = g/cm3
  Dvalue = 7.9
  Group = -> [Cd_element002,W_element001,O_element020]
  conduct = 2
  density = 1
  expand = 3
  formula = G4_CADMIUM_TUNGSTATE
  name = G4_CADMIUM_TUNGSTATE
  specific = 4
FEATURE [App::DocumentObjectGroupPython] Ca_element005  label="Ca_element : 1"  # scripted group (container) (typed FeaturePython)
  n = 1
  ref = Ca_element
FEATURE [App::DocumentObjectGroupPython] C_element022  label="C_element : 009"  # scripted group (container) (typed FeaturePython)
  n = 1
  ref = C_element
FEATURE [App::DocumentObjectGroupPython] O_element021  label="O_element : 009"  # scripted group (container) (typed FeaturePython)
  n = 3
  ref = O_element
FEATURE [App::DocumentObjectGroupPython] G4_CALCIUM_CARBONATE  # scripted group (container) (typed FeaturePython)
  Dunit = g/cm3
  Dvalue = 2.8
  Group = -> [Ca_element005,C_element022,O_element021]
  conduct = 2
  density = 1
  expand = 3
  formula = G4_CALCIUM_CARBONATE
  name = G4_CALCIUM_CARBONATE
  specific = 4
FEATURE [App::DocumentObjectGroupPython] Ca_element006  label="Ca_element : 002"  # scripted group (container) (typed FeaturePython)
  n = 1
  ref = Ca_element
FEATURE [App::DocumentObjectGroupPython] F_element005  label="F_element : 003"  # scripted group (container) (typed FeaturePython)
  n = 2
  ref = F_element
FEATURE [App::DocumentObjectGroupPython] G4_CALCIUM_FLUORIDE  # scripted group (container) (typed FeaturePython)
  Dunit = g/cm3
  Dvalue = 3.18
  Group = -> [Ca_element006,F_element005]
  conduct = 2
  density = 1
  expand = 3
  formula = G4_CALCIUM_FLUORIDE
  name = G4_CALCIUM_FLUORIDE
  specific = 4
FEATURE [App::DocumentObjectGroupPython] Ca_element007  label="Ca_element : 003"  # scripted group (container) (typed FeaturePython)
  n = 1
  ref = Ca_element
FEATURE [App::DocumentObjectGroupPython] O_element022  label="O_element : 010"  # scripted group (container) (typed FeaturePython)
  n = 1
  ref = O_element
FEATURE [App::DocumentObjectGroupPython] G4_CALCIUM_OXIDE  # scripted group (container) (typed FeaturePython)
  Dunit = g/cm3
  Dvalue = 3.3
  Group = -> [Ca_element007,O_element022]
  conduct = 2
  density = 1
  expand = 3
  formula = G4_CALCIUM_OXIDE
  name = G4_CALCIUM_OXIDE
  specific = 4
FEATURE [App::DocumentObjectGroupPython] Ca_element008  label="Ca_element : 004"  # scripted group (container) (typed FeaturePython)
  n = 1
  ref = Ca_element
FEATURE [App::DocumentObjectGroupPython] S_element007  label="S_element : 002"  # scripted group (container) (typed FeaturePython)
  n = 1
  ref = S_element
FEATURE [App::DocumentObjectGroupPython] O_element023  label="O_element : 011"  # scripted group (container) (typed FeaturePython)
  n = 4
  ref = O_element
FEATURE [App::DocumentObjectGroupPython] G4_CALCIUM_SULFATE  # scripted group (container) (typed FeaturePython)
  Dunit = g/cm3
  Dvalue = 2.96
  Group = -> [Ca_element008,S_element007,O_element023]
  conduct = 2
  density = 1
  expand = 3
  formula = G4_CALCIUM_SULFATE
  name = G4_CALCIUM_SULFATE
  specific = 4
FEATURE [App::DocumentObjectGroupPython] Ca_element009  label="Ca_element : 005"  # scripted group (container) (typed FeaturePython)
  n = 1
  ref = Ca_element
FEATURE [App::DocumentObjectGroupPython] W_element002  label="W_element : 002"  # scripted group (container) (typed FeaturePython)
  n = 1
  ref = W_element
FEATURE [App::DocumentObjectGroupPython] O_element024  label="O_element : 012"  # scripted group (container) (typed FeaturePython)
  n = 4
  ref = O_element
FEATURE [App::DocumentObjectGroupPython] G4_CALCIUM_TUNGSTATE  # scripted group (container) (typed FeaturePython)
  Dunit = g/cm3
  Dvalue = 6.062
  Group = -> [Ca_element009,W_element002,O_element024]
  conduct = 2
  density = 1
  expand = 3
  formula = G4_CALCIUM_TUNGSTATE
  name = G4_CALCIUM_TUNGSTATE
  specific = 4
FEATURE [App::DocumentObjectGroupPython] C_element023  label="C_element : 010"  # scripted group (container) (typed FeaturePython)
  n = 1
  ref = C_element
FEATURE [App::DocumentObjectGroupPython] O_element025  label="O_element : 013"  # scripted group (container) (typed FeaturePython)
  n = 2
  ref = O_element
FEATURE [App::DocumentObjectGroupPython] G4_CARBON_DIOXIDE  # scripted group (container) (typed FeaturePython)
  Dunit = g/cm3
  Dvalue = 0.00184212
  Group = -> [C_element023,O_element025]
  conduct = 2
  density = 1
  expand = 3
  formula = G4_CARBON_DIOXIDE
  name = G4_CARBON_DIOXIDE
  specific = 4
FEATURE [App::DocumentObjectGroupPython] C_element024  label="C_element : 011"  # scripted group (container) (typed FeaturePython)
  n = 1
  ref = C_element
FEATURE [App::DocumentObjectGroupPython] Cl_element004  label="Cl_element : 4"  # scripted group (container) (typed FeaturePython)
  n = 4
  ref = Cl_element
FEATURE [App::DocumentObjectGroupPython] G4_CARBON_TETRACHLORIDE  # scripted group (container) (typed FeaturePython)
  Dunit = g/cm3
  Dvalue = 1.594
  Group = -> [C_element024,Cl_element004]
  conduct = 2
  density = 1
  expand = 3
  formula = G4_CARBON_TETRACHLORIDE
  name = G4_CARBON_TETRACHLORIDE
  specific = 4
FEATURE [App::DocumentObjectGroupPython] C_element025  label="C_element : 012"  # scripted group (container) (typed FeaturePython)
  n = 6
  ref = C_element
FEATURE [App::DocumentObjectGroupPython] H_element021  label="H_element : 012"  # scripted group (container) (typed FeaturePython)
  n = 10
  ref = H_element
FEATURE [App::DocumentObjectGroupPython] O_element026  label="O_element : 5"  # scripted group (container) (typed FeaturePython)
  n = 5
  ref = O_element
FEATURE [App::DocumentObjectGroupPython] G4_CELLULOSE_CELLOPHANE  # scripted group (container) (typed FeaturePython)
  Dunit = g/cm3
  Dvalue = 1.42
  Group = -> [C_element025,H_element021,O_element026]
  conduct = 2
  density = 1
  expand = 3
  formula = G4_CELLULOSE_CELLOPHANE
  name = G4_CELLULOSE_CELLOPHANE
  specific = 4
FEATURE [App::DocumentObjectGroupPython] H_element022  label="H_element : 0.067"  # scripted group (container) (typed FeaturePython)
  n = 0.067125
FEATURE [App::DocumentObjectGroupPython] C_element026  label="C_element : 0.545"  # scripted group (container) (typed FeaturePython)
  n = 0.545403
FEATURE [App::DocumentObjectGroupPython] O_element027  label="O_element : 0.387"  # scripted group (container) (typed FeaturePython)
  n = 0.387472
FEATURE [App::DocumentObjectGroupPython] G4_CELLULOSE_BUTYRATE  # scripted group (container) (typed FeaturePython)
  Dunit = g/cm3
  Dvalue = 1.2
  Group = -> [H_element022,C_element026,O_element027]
  conduct = 2
  density = 1
  expand = 3
  formula = G4_CELLULOSE_BUTYRATE
  name = G4_CELLULOSE_BUTYRATE
  specific = 4
FEATURE [App::DocumentObjectGroupPython] H_element023  label="H_element : 0.029"  # scripted group (container) (typed FeaturePython)
  n = 0.029216
FEATURE [App::DocumentObjectGroupPython] C_element027  label="C_element : 0.271"  # scripted group (container) (typed FeaturePython)
  n = 0.271296
FEATURE [App::DocumentObjectGroupPython] N_element013  label="N_element : 0.121"  # scripted group (container) (typed FeaturePython)
  n = 0.121276
FEATURE [App::DocumentObjectGroupPython] O_element028  label="O_element : 0.578"  # scripted group (container) (typed FeaturePython)
  n = 0.578212
FEATURE [App::DocumentObjectGroupPython] G4_CELLULOSE_NITRATE  # scripted group (container) (typed FeaturePython)
  Dunit = g/cm3
  Dvalue = 1.49
  Group = -> [H_element023,C_element027,N_element013,O_element028]
  conduct = 2
  density = 1
  expand = 3
  formula = G4_CELLULOSE_NITRATE
  name = G4_CELLULOSE_NITRATE
  specific = 4
FEATURE [App::DocumentObjectGroupPython] H_element024  label="H_element : 0.108"  # scripted group (container) (typed FeaturePython)
  n = 0.107596
FEATURE [App::DocumentObjectGroupPython] N_element014  label="N_element : 0.001"  # scripted group (container) (typed FeaturePython)
  n = 0.0008
FEATURE [App::DocumentObjectGroupPython] O_element029  label="O_element : 0.875"  # scripted group (container) (typed FeaturePython)
  n = 0.874976
FEATURE [App::DocumentObjectGroupPython] S_element008  label="S_element : 0.015"  # scripted group (container) (typed FeaturePython)
  n = 0.014627
FEATURE [App::DocumentObjectGroupPython] Ce_element001  label="Ce_element : 0.002"  # scripted group (container) (typed FeaturePython)
  n = 0.002001
FEATURE [App::DocumentObjectGroupPython] G4_CERIC_SULFATE  # scripted group (container) (typed FeaturePython)
  Dunit = g/cm3
  Dvalue = 1.03
  Group = -> [H_element024,N_element014,O_element029,S_element008,Ce_element001]
  conduct = 2
  density = 1
  expand = 3
  formula = G4_CERIC_SULFATE
  name = G4_CERIC_SULFATE
  specific = 4
FEATURE [App::DocumentObjectGroupPython] Cs_element001  label="Cs_element : 1"  # scripted group (container) (typed FeaturePython)
  n = 1
  ref = Cs_element
FEATURE [App::DocumentObjectGroupPython] F_element006  label="F_element : 1"  # scripted group (container) (typed FeaturePython)
  n = 1
  ref = F_element
FEATURE [App::DocumentObjectGroupPython] G4_CESIUM_FLUORIDE  # scripted group (container) (typed FeaturePython)
  Dunit = g/cm3
  Dvalue = 4.115
  Group = -> [Cs_element001,F_element006]
  conduct = 2
  density = 1
  expand = 3
  formula = G4_CESIUM_FLUORIDE
  name = G4_CESIUM_FLUORIDE
  specific = 4
FEATURE [App::DocumentObjectGroupPython] Cs_element002  label="Cs_element : 002"  # scripted group (container) (typed FeaturePython)
  n = 1
  ref = Cs_element
FEATURE [App::DocumentObjectGroupPython] I_element001  label="I_element : 1"  # scripted group (container) (typed FeaturePython)
  n = 1
  ref = I_element
FEATURE [App::DocumentObjectGroupPython] G4_CESIUM_IODIDE  # scripted group (container) (typed FeaturePython)
  Dunit = g/cm3
  Dvalue = 4.51
  Group = -> [Cs_element002,I_element001]
  conduct = 2
  density = 1
  expand = 3
  formula = G4_CESIUM_IODIDE
  name = G4_CESIUM_IODIDE
  specific = 4
FEATURE [App::DocumentObjectGroupPython] C_element028  label="C_element : 013"  # scripted group (container) (typed FeaturePython)
  n = 6
  ref = C_element
FEATURE [App::DocumentObjectGroupPython] H_element025  label="H_element : 013"  # scripted group (container) (typed FeaturePython)
  n = 5
  ref = H_element
FEATURE [App::DocumentObjectGroupPython] Cl_element005  label="Cl_element : 1"  # scripted group (container) (typed FeaturePython)
  n = 1
  ref = Cl_element
FEATURE [App::DocumentObjectGroupPython] G4_CHLOROBENZENE  # scripted group (container) (typed FeaturePython)
  Dunit = g/cm3
  Dvalue = 1.1058
  Group = -> [C_element028,H_element025,Cl_element005]
  conduct = 2
  density = 1
  expand = 3
  formula = G4_CHLOROBENZENE
  name = G4_CHLOROBENZENE
  specific = 4
FEATURE [App::DocumentObjectGroupPython] C_element029  label="C_element : 014"  # scripted group (container) (typed FeaturePython)
  n = 1
  ref = C_element
FEATURE [App::DocumentObjectGroupPython] H_element026  label="H_element : 1"  # scripted group (container) (typed FeaturePython)
  n = 1
  ref = H_element
FEATURE [App::DocumentObjectGroupPython] Cl_element006  label="Cl_element : 3"  # scripted group (container) (typed FeaturePython)
  n = 3
  ref = Cl_element
FEATURE [App::DocumentObjectGroupPython] G4_CHLOROFORM  # scripted group (container) (typed FeaturePython)
  Dunit = g/cm3
  Dvalue = 1.4832
  Group = -> [C_element029,H_element026,Cl_element006]
  conduct = 2
  density = 1
  expand = 3
  formula = G4_CHLOROFORM
  name = G4_CHLOROFORM
  specific = 4
FEATURE [App::DocumentObjectGroupPython] H_element027  label="H_element : 0.010"  # scripted group (container) (typed FeaturePython)
  n = 0.01
FEATURE [App::DocumentObjectGroupPython] C_element030  label="C_element : 0.001"  # scripted group (container) (typed FeaturePython)
  n = 0.001
FEATURE [App::DocumentObjectGroupPython] O_element030  label="O_element : 0.529"  # scripted group (container) (typed FeaturePython)
  n = 0.529107
FEATURE [App::DocumentObjectGroupPython] Na_element005  label="Na_element : 0.016"  # scripted group (container) (typed FeaturePython)
  n = 0.016
FEATURE [App::DocumentObjectGroupPython] Mg_element003  label="Mg_element : 0.004"  # scripted group (container) (typed FeaturePython)
  n = 0.002
FEATURE [App::DocumentObjectGroupPython] Al_element002  label="Al_element : 0.034"  # scripted group (container) (typed FeaturePython)
  n = 0.033872
FEATURE [App::DocumentObjectGroupPython] Si_element002  label="Si_element : 0.337"  # scripted group (container) (typed FeaturePython)
  n = 0.337021
FEATURE [App::DocumentObjectGroupPython] K_element003  label="K_element : 0.013"  # scripted group (container) (typed FeaturePython)
  n = 0.013
FEATURE [App::DocumentObjectGroupPython] Ca_element010  label="Ca_element : 0.044"  # scripted group (container) (typed FeaturePython)
  n = 0.044
FEATURE [App::DocumentObjectGroupPython] Fe_element002  label="Fe_element : 0.014"  # scripted group (container) (typed FeaturePython)
  n = 0.014
FEATURE [App::DocumentObjectGroupPython] G4_CONCRETE  # scripted group (container) (typed FeaturePython)
  Dunit = g/cm3
  Dvalue = 2.3
  Group = -> [H_element027,C_element030,O_element030,Na_element005,Mg_element003,Al_element002,Si_element002,K_element003,Ca_element010,Fe_element002]
  conduct = 2
  density = 1
  expand = 3
  formula = G4_CONCRETE
  name = G4_CONCRETE
  specific = 4
FEATURE [App::DocumentObjectGroupPython] C_element031  label="C_element : 015"  # scripted group (container) (typed FeaturePython)
  n = 6
  ref = C_element
FEATURE [App::DocumentObjectGroupPython] H_element028  label="H_element : 12"  # scripted group (container) (typed FeaturePython)
  n = 12
  ref = H_element
FEATURE [App::DocumentObjectGroupPython] G4_CYCLOHEXANE  # scripted group (container) (typed FeaturePython)
  Dunit = g/cm3
  Dvalue = 0.779
  Group = -> [C_element031,H_element028]
  conduct = 2
  density = 1
  expand = 3
  formula = G4_CYCLOHEXANE
  name = G4_CYCLOHEXANE
  specific = 4
FEATURE [App::DocumentObjectGroupPython] C_element032  label="C_element : 016"  # scripted group (container) (typed FeaturePython)
  n = 6
  ref = C_element
FEATURE [App::DocumentObjectGroupPython] H_element029  label="H_element : 4"  # scripted group (container) (typed FeaturePython)
  n = 4
  ref = H_element
FEATURE [App::DocumentObjectGroupPython] Cl_element007  label="Cl_element : 2"  # scripted group (container) (typed FeaturePython)
  n = 2
  ref = Cl_element
FEATURE [App::DocumentObjectGroupPython] G4_1_2_DICHLOROBENZENE  label="G4_1.2-DICHLOROBENZENE"  # scripted group (container) (typed FeaturePython)
  Dunit = g/cm3
  Dvalue = 1.3048
  Group = -> [C_element032,H_element029,Cl_element007]
  conduct = 2
  density = 1
  expand = 3
  formula = G4_1.2-DICHLOROBENZENE
  name = G4_1.2-DICHLOROBENZENE
  specific = 4
FEATURE [App::DocumentObjectGroupPython] C_element033  label="C_element : 017"  # scripted group (container) (typed FeaturePython)
  n = 4
  ref = C_element
FEATURE [App::DocumentObjectGroupPython] H_element030  label="H_element : 8"  # scripted group (container) (typed FeaturePython)
  n = 8
  ref = H_element
FEATURE [App::DocumentObjectGroupPython] O_element031  label="O_element : 014"  # scripted group (container) (typed FeaturePython)
  n = 1
  ref = O_element
FEATURE [App::DocumentObjectGroupPython] Cl_element008  label="Cl_element : 005"  # scripted group (container) (typed FeaturePython)
  n = 2
  ref = Cl_element
FEATURE [App::DocumentObjectGroupPython] G4_DICHLORODIETHYL_ETHER  # scripted group (container) (typed FeaturePython)
  Dunit = g/cm3
  Dvalue = 1.2199
  Group = -> [C_element033,H_element030,O_element031,Cl_element008]
  conduct = 2
  density = 1
  expand = 3
  formula = G4_DICHLORODIETHYL_ETHER
  name = G4_DICHLORODIETHYL_ETHER
  specific = 4
FEATURE [App::DocumentObjectGroupPython] C_element034  label="C_element : 018"  # scripted group (container) (typed FeaturePython)
  n = 2
  ref = C_element
FEATURE [App::DocumentObjectGroupPython] H_element031  label="H_element : 014"  # scripted group (container) (typed FeaturePython)
  n = 4
  ref = H_element
FEATURE [App::DocumentObjectGroupPython] Cl_element009  label="Cl_element : 006"  # scripted group (container) (typed FeaturePython)
  n = 2
  ref = Cl_element
FEATURE [App::DocumentObjectGroupPython] G4_1_2_DICHLOROETHANE  label="G4_1.2-DICHLOROETHANE"  # scripted group (container) (typed FeaturePython)
  Dunit = g/cm3
  Dvalue = 1.2351
  Group = -> [C_element034,H_element031,Cl_element009]
  conduct = 2
  density = 1
  expand = 3
  formula = G4_1.2-DICHLOROETHANE
  name = G4_1.2-DICHLOROETHANE
  specific = 4
FEATURE [App::DocumentObjectGroupPython] C_element035  label="C_element : 019"  # scripted group (container) (typed FeaturePython)
  n = 4
  ref = C_element
FEATURE [App::DocumentObjectGroupPython] H_element032  label="H_element : 015"  # scripted group (container) (typed FeaturePython)
  n = 10
  ref = H_element
FEATURE [App::DocumentObjectGroupPython] O_element032  label="O_element : 015"  # scripted group (container) (typed FeaturePython)
  n = 1
  ref = O_element
FEATURE [App::DocumentObjectGroupPython] G4_DIETHYL_ETHER  # scripted group (container) (typed FeaturePython)
  Dunit = g/cm3
  Dvalue = 0.71378
  Group = -> [C_element035,H_element032,O_element032]
  conduct = 2
  density = 1
  expand = 3
  formula = G4_DIETHYL_ETHER
  name = G4_DIETHYL_ETHER
  specific = 4
FEATURE [App::DocumentObjectGroupPython] C_element036  label="C_element : 020"  # scripted group (container) (typed FeaturePython)
  n = 3
  ref = C_element
FEATURE [App::DocumentObjectGroupPython] H_element033  label="H_element : 016"  # scripted group (container) (typed FeaturePython)
  n = 7
  ref = H_element
FEATURE [App::DocumentObjectGroupPython] N_element015  label="N_element : 008"  # scripted group (container) (typed FeaturePython)
  n = 1
  ref = N_element
FEATURE [App::DocumentObjectGroupPython] O_element033  label="O_element : 016"  # scripted group (container) (typed FeaturePython)
  n = 1
  ref = O_element
FEATURE [App::DocumentObjectGroupPython] G4_N_N_DIMETHYL_FORMAMIDE  label="G4_N.N-DIMETHYL_FORMAMIDE"  # scripted group (container) (typed FeaturePython)
  Dunit = g/cm3
  Dvalue = 0.9487
  Group = -> [C_element036,H_element033,N_element015,O_element033]
  conduct = 2
  density = 1
  expand = 3
  formula = G4_N.N-DIMETHYL_FORMAMIDE
  name = G4_N.N-DIMETHYL_FORMAMIDE
  specific = 4
FEATURE [App::DocumentObjectGroupPython] C_element037  label="C_element : 021"  # scripted group (container) (typed FeaturePython)
  n = 2
  ref = C_element
FEATURE [App::DocumentObjectGroupPython] H_element034  label="H_element : 017"  # scripted group (container) (typed FeaturePython)
  n = 6
  ref = H_element
FEATURE [App::DocumentObjectGroupPython] O_element034  label="O_element : 017"  # scripted group (container) (typed FeaturePython)
  n = 1
  ref = O_element
FEATURE [App::DocumentObjectGroupPython] S_element009  label="S_element : 003"  # scripted group (container) (typed FeaturePython)
  n = 1
  ref = S_element
FEATURE [App::DocumentObjectGroupPython] G4_DIMETHYL_SULFOXIDE  # scripted group (container) (typed FeaturePython)
  Dunit = g/cm3
  Dvalue = 1.1014
  Group = -> [C_element037,H_element034,O_element034,S_element009]
  conduct = 2
  density = 1
  expand = 3
  formula = G4_DIMETHYL_SULFOXIDE
  name = G4_DIMETHYL_SULFOXIDE
  specific = 4
FEATURE [App::DocumentObjectGroupPython] C_element038  label="C_element : 022"  # scripted group (container) (typed FeaturePython)
  n = 2
  ref = C_element
FEATURE [App::DocumentObjectGroupPython] H_element035  label="H_element : 018"  # scripted group (container) (typed FeaturePython)
  n = 6
  ref = H_element
FEATURE [App::DocumentObjectGroupPython] G4_ETHANE  # scripted group (container) (typed FeaturePython)
  Dunit = g/cm3
  Dvalue = 0.00125324
  Group = -> [C_element038,H_element035]
  conduct = 2
  density = 1
  expand = 3
  formula = G4_ETHANE
  name = G4_ETHANE
  specific = 4
FEATURE [App::DocumentObjectGroupPython] C_element039  label="C_element : 023"  # scripted group (container) (typed FeaturePython)
  n = 2
  ref = C_element
FEATURE [App::DocumentObjectGroupPython] H_element036  label="H_element : 019"  # scripted group (container) (typed FeaturePython)
  n = 6
  ref = H_element
FEATURE [App::DocumentObjectGroupPython] O_element035  label="O_element : 018"  # scripted group (container) (typed FeaturePython)
  n = 1
  ref = O_element
FEATURE [App::DocumentObjectGroupPython] G4_ETHYL_ALCOHOL  # scripted group (container) (typed FeaturePython)
  Dunit = g/cm3
  Dvalue = 0.7893
  Group = -> [C_element039,H_element036,O_element035]
  conduct = 2
  density = 1
  expand = 3
  formula = G4_ETHYL_ALCOHOL
  name = G4_ETHYL_ALCOHOL
  specific = 4
FEATURE [App::DocumentObjectGroupPython] H_element037  label="H_element : 0.090"  # scripted group (container) (typed FeaturePython)
  n = 0.090027
FEATURE [App::DocumentObjectGroupPython] C_element040  label="C_element : 0.585"  # scripted group (container) (typed FeaturePython)
  n = 0.585182
FEATURE [App::DocumentObjectGroupPython] O_element036  label="O_element : 0.325"  # scripted group (container) (typed FeaturePython)
  n = 0.324791
FEATURE [App::DocumentObjectGroupPython] G4_ETHYL_CELLULOSE  # scripted group (container) (typed FeaturePython)
  Dunit = g/cm3
  Dvalue = 1.13
  Group = -> [H_element037,C_element040,O_element036]
  conduct = 2
  density = 1
  expand = 3
  formula = G4_ETHYL_CELLULOSE
  name = G4_ETHYL_CELLULOSE
  specific = 4
FEATURE [App::DocumentObjectGroupPython] C_element041  label="C_element : 024"  # scripted group (container) (typed FeaturePython)
  n = 2
  ref = C_element
FEATURE [App::DocumentObjectGroupPython] H_element038  label="H_element : 020"  # scripted group (container) (typed FeaturePython)
  n = 4
  ref = H_element
FEATURE [App::DocumentObjectGroupPython] G4_ETHYLENE  # scripted group (container) (typed FeaturePython)
  Dunit = g/cm3
  Dvalue = 0.00117497
  Group = -> [C_element041,H_element038]
  conduct = 2
  density = 1
  expand = 3
  formula = G4_ETHYLENE
  name = G4_ETHYLENE
  specific = 4
FEATURE [App::DocumentObjectGroupPython] H_element039  label="H_element : 0.096"  # scripted group (container) (typed FeaturePython)
  n = 0.096
FEATURE [App::DocumentObjectGroupPython] C_element042  label="C_element : 0.195"  # scripted group (container) (typed FeaturePython)
  n = 0.195
FEATURE [App::DocumentObjectGroupPython] N_element016  label="N_element : 0.057"  # scripted group (container) (typed FeaturePython)
  n = 0.057
FEATURE [App::DocumentObjectGroupPython] O_element037  label="O_element : 0.646"  # scripted group (container) (typed FeaturePython)
  n = 0.646
FEATURE [App::DocumentObjectGroupPython] Na_element006  label="Na_element : 0.017"  # scripted group (container) (typed FeaturePython)
  n = 0.001
FEATURE [App::DocumentObjectGroupPython] P_element005  label="P_element : 0.104"  # scripted group (container) (typed FeaturePython)
  n = 0.001
FEATURE [App::DocumentObjectGroupPython] S_element010  label="S_element : 0.016"  # scripted group (container) (typed FeaturePython)
  n = 0.003
FEATURE [App::DocumentObjectGroupPython] Cl_element010  label="Cl_element : 0.005"  # scripted group (container) (typed FeaturePython)
  n = 0.001
FEATURE [App::DocumentObjectGroupPython] G4_EYE_LENS_ICRP  # scripted group (container) (typed FeaturePython)
  Dunit = g/cm3
  Dvalue = 1.07
  Group = -> [H_element039,C_element042,N_element016,O_element037,Na_element006,P_element005,S_element010,Cl_element010]
  conduct = 2
  density = 1
  expand = 3
  formula = G4_EYE_LENS_ICRP
  name = G4_EYE_LENS_ICRP
  specific = 4
FEATURE [App::DocumentObjectGroupPython] Fe_element003  label="Fe_element : 2"  # scripted group (container) (typed FeaturePython)
  n = 2
  ref = Fe_element
FEATURE [App::DocumentObjectGroupPython] O_element038  label="O_element : 019"  # scripted group (container) (typed FeaturePython)
  n = 3
  ref = O_element
FEATURE [App::DocumentObjectGroupPython] G4_FERRIC_OXIDE  # scripted group (container) (typed FeaturePython)
  Dunit = g/cm3
  Dvalue = 5.2
  Group = -> [Fe_element003,O_element038]
  conduct = 2
  density = 1
  expand = 3
  formula = G4_FERRIC_OXIDE
  name = G4_FERRIC_OXIDE
  specific = 4
FEATURE [App::DocumentObjectGroupPython] Fe_element004  label="Fe_element : 1"  # scripted group (container) (typed FeaturePython)
  n = 1
  ref = Fe_element
FEATURE [App::DocumentObjectGroupPython] B_element003  label="B_element : 1"  # scripted group (container) (typed FeaturePython)
  n = 1
  ref = B_element
FEATURE [App::DocumentObjectGroupPython] G4_FERROBORIDE  # scripted group (container) (typed FeaturePython)
  Dunit = g/cm3
  Dvalue = 7.15
  Group = -> [Fe_element004,B_element003]
  conduct = 2
  density = 1
  expand = 3
  formula = G4_FERROBORIDE
  name = G4_FERROBORIDE
  specific = 4
FEATURE [App::DocumentObjectGroupPython] Fe_element005  label="Fe_element : 003"  # scripted group (container) (typed FeaturePython)
  n = 1
  ref = Fe_element
FEATURE [App::DocumentObjectGroupPython] O_element039  label="O_element : 020"  # scripted group (container) (typed FeaturePython)
  n = 1
  ref = O_element
FEATURE [App::DocumentObjectGroupPython] G4_FERROUS_OXIDE  # scripted group (container) (typed FeaturePython)
  Dunit = g/cm3
  Dvalue = 5.7
  Group = -> [Fe_element005,O_element039]
  conduct = 2
  density = 1
  expand = 3
  formula = G4_FERROUS_OXIDE
  name = G4_FERROUS_OXIDE
  specific = 4
FEATURE [App::DocumentObjectGroupPython] H_element040  label="H_element : 0.115"  # scripted group (container) (typed FeaturePython)
  n = 0.108259
FEATURE [App::DocumentObjectGroupPython] N_element017  label="N_element : 0.000"  # scripted group (container) (typed FeaturePython)
  n = 2.7e-05
FEATURE [App::DocumentObjectGroupPython] O_element040  label="O_element : 0.879"  # scripted group (container) (typed FeaturePython)
  n = 0.878636
FEATURE [App::DocumentObjectGroupPython] Na_element007  label="Na_element : 0.000"  # scripted group (container) (typed FeaturePython)
  n = 2.2e-05
FEATURE [App::DocumentObjectGroupPython] S_element011  label="S_element : 0.013"  # scripted group (container) (typed FeaturePython)
  n = 0.012968
FEATURE [App::DocumentObjectGroupPython] Cl_element011  label="Cl_element : 0.000"  # scripted group (container) (typed FeaturePython)
  n = 3.4e-05
FEATURE [App::DocumentObjectGroupPython] Fe_element006  label="Fe_element : 0.000"  # scripted group (container) (typed FeaturePython)
  n = 5.4e-05
FEATURE [App::DocumentObjectGroupPython] G4_FERROUS_SULFATE  # scripted group (container) (typed FeaturePython)
  Dunit = g/cm3
  Dvalue = 1.024
  Group = -> [H_element040,N_element017,O_element040,Na_element007,S_element011,Cl_element011,Fe_element006]
  conduct = 2
  density = 1
  expand = 3
  formula = G4_FERROUS_SULFATE
  name = G4_FERROUS_SULFATE
  specific = 4
FEATURE [App::DocumentObjectGroupPython] C_element043  label="C_element : 0.099"  # scripted group (container) (typed FeaturePython)
  n = 0.099335
FEATURE [App::DocumentObjectGroupPython] F_element007  label="F_element : 0.314"  # scripted group (container) (typed FeaturePython)
  n = 0.314247
FEATURE [App::DocumentObjectGroupPython] Cl_element012  label="Cl_element : 0.586"  # scripted group (container) (typed FeaturePython)
  n = 0.586418
FEATURE [App::DocumentObjectGroupPython] G4_FREON_12  label="G4_FREON-12"  # scripted group (container) (typed FeaturePython)
  Dunit = g/cm3
  Dvalue = 1.12
  Group = -> [C_element043,F_element007,Cl_element012]
  conduct = 2
  density = 1
  expand = 3
  formula = G4_FREON-12
  name = G4_FREON-12
  specific = 4
FEATURE [App::DocumentObjectGroupPython] C_element044  label="C_element : 0.057"  # scripted group (container) (typed FeaturePython)
  n = 0.057245
FEATURE [App::DocumentObjectGroupPython] F_element008  label="F_element : 0.181"  # scripted group (container) (typed FeaturePython)
  n = 0.181096
FEATURE [App::DocumentObjectGroupPython] Br_element001  label="Br_element : 0.762"  # scripted group (container) (typed FeaturePython)
  n = 0.761659
FEATURE [App::DocumentObjectGroupPython] G4_FREON_12B2  label="G4_FREON-12B2"  # scripted group (container) (typed FeaturePython)
  Dunit = g/cm3
  Dvalue = 1.8
  Group = -> [C_element044,F_element008,Br_element001]
  conduct = 2
  density = 1
  expand = 3
  formula = G4_FREON-12B2
  name = G4_FREON-12B2
  specific = 4
FEATURE [App::DocumentObjectGroupPython] C_element045  label="C_element : 0.115"  # scripted group (container) (typed FeaturePython)
  n = 0.114983
FEATURE [App::DocumentObjectGroupPython] F_element009  label="F_element : 0.546"  # scripted group (container) (typed FeaturePython)
  n = 0.545621
FEATURE [App::DocumentObjectGroupPython] Cl_element013  label="Cl_element : 0.339"  # scripted group (container) (typed FeaturePython)
  n = 0.339396
FEATURE [App::DocumentObjectGroupPython] G4_FREON_13  label="G4_FREON-13"  # scripted group (container) (typed FeaturePython)
  Dunit = g/cm3
  Dvalue = 0.95
  Group = -> [C_element045,F_element009,Cl_element013]
  conduct = 2
  density = 1
  expand = 3
  formula = G4_FREON-13
  name = G4_FREON-13
  specific = 4
FEATURE [App::DocumentObjectGroupPython] C_element046  label="C_element : 025"  # scripted group (container) (typed FeaturePython)
  n = 1
  ref = C_element
FEATURE [App::DocumentObjectGroupPython] F_element010  label="F_element : 3"  # scripted group (container) (typed FeaturePython)
  n = 3
  ref = F_element
FEATURE [App::DocumentObjectGroupPython] Br_element002  label="Br_element : 1"  # scripted group (container) (typed FeaturePython)
  n = 1
  ref = Br_element
FEATURE [App::DocumentObjectGroupPython] G4_FREON_13B1  label="G4_FREON-13B1"  # scripted group (container) (typed FeaturePython)
  Dunit = g/cm3
  Dvalue = 1.5
  Group = -> [C_element046,F_element010,Br_element002]
  conduct = 2
  density = 1
  expand = 3
  formula = G4_FREON-13B1
  name = G4_FREON-13B1
  specific = 4
FEATURE [App::DocumentObjectGroupPython] C_element047  label="C_element : 0.061"  # scripted group (container) (typed FeaturePython)
  n = 0.061309
FEATURE [App::DocumentObjectGroupPython] F_element011  label="F_element : 0.291"  # scripted group (container) (typed FeaturePython)
  n = 0.290924
FEATURE [App::DocumentObjectGroupPython] I_element002  label="I_element : 0.648"  # scripted group (container) (typed FeaturePython)
  n = 0.647767
FEATURE [App::DocumentObjectGroupPython] G4_FREON_13I1  label="G4_FREON-13I1"  # scripted group (container) (typed FeaturePython)
  Dunit = g/cm3
  Dvalue = 1.8
  Group = -> [C_element047,F_element011,I_element002]
  conduct = 2
  density = 1
  expand = 3
  formula = G4_FREON-13I1
  name = G4_FREON-13I1
  specific = 4
FEATURE [App::DocumentObjectGroupPython] Gd_element001  label="Gd_element : 2"  # scripted group (container) (typed FeaturePython)
  n = 2
  ref = Gd_element
FEATURE [App::DocumentObjectGroupPython] O_element041  label="O_element : 021"  # scripted group (container) (typed FeaturePython)
  n = 2
  ref = O_element
FEATURE [App::DocumentObjectGroupPython] S_element012  label="S_element : 004"  # scripted group (container) (typed FeaturePython)
  n = 1
  ref = S_element
FEATURE [App::DocumentObjectGroupPython] G4_GADOLINIUM_OXYSULFIDE  # scripted group (container) (typed FeaturePython)
  Dunit = g/cm3
  Dvalue = 7.44
  Group = -> [Gd_element001,O_element041,S_element012]
  conduct = 2
  density = 1
  expand = 3
  formula = G4_GADOLINIUM_OXYSULFIDE
  name = G4_GADOLINIUM_OXYSULFIDE
  specific = 4
FEATURE [App::DocumentObjectGroupPython] Ga_element001  label="Ga_element : 1"  # scripted group (container) (typed FeaturePython)
  n = 1
  ref = Ga_element
FEATURE [App::DocumentObjectGroupPython] As_element001  label="As_element : 1"  # scripted group (container) (typed FeaturePython)
  n = 1
  ref = As_element
FEATURE [App::DocumentObjectGroupPython] G4_GALLIUM_ARSENIDE  # scripted group (container) (typed FeaturePython)
  Dunit = g/cm3
  Dvalue = 5.31
  Group = -> [Ga_element001,As_element001]
  conduct = 2
  density = 1
  expand = 3
  formula = G4_GALLIUM_ARSENIDE
  name = G4_GALLIUM_ARSENIDE
  specific = 4
FEATURE [App::DocumentObjectGroupPython] H_element041  label="H_element : 0.081"  # scripted group (container) (typed FeaturePython)
  n = 0.08118
FEATURE [App::DocumentObjectGroupPython] C_element048  label="C_element : 0.416"  # scripted group (container) (typed FeaturePython)
  n = 0.41606
FEATURE [App::DocumentObjectGroupPython] N_element018  label="N_element : 0.111"  # scripted group (container) (typed FeaturePython)
  n = 0.11124
FEATURE [App::DocumentObjectGroupPython] O_element042  label="O_element : 0.381"  # scripted group (container) (typed FeaturePython)
  n = 0.38064
FEATURE [App::DocumentObjectGroupPython] S_element013  label="S_element : 0.011"  # scripted group (container) (typed FeaturePython)
  n = 0.01088
FEATURE [App::DocumentObjectGroupPython] G4_GEL_PHOTO_EMULSION  # scripted group (container) (typed FeaturePython)
  Dunit = g/cm3
  Dvalue = 1.2914
  Group = -> [H_element041,C_element048,N_element018,O_element042,S_element013]
  conduct = 2
  density = 1
  expand = 3
  formula = G4_GEL_PHOTO_EMULSION
  name = G4_GEL_PHOTO_EMULSION
  specific = 4
FEATURE [App::DocumentObjectGroupPython] B_element004  label="B_element : 0.040"  # scripted group (container) (typed FeaturePython)
  n = 0.0400639
FEATURE [App::DocumentObjectGroupPython] O_element043  label="O_element : 0.540"  # scripted group (container) (typed FeaturePython)
  n = 0.539561
FEATURE [App::DocumentObjectGroupPython] Na_element008  label="Na_element : 0.028"  # scripted group (container) (typed FeaturePython)
  n = 0.0281909
FEATURE [App::DocumentObjectGroupPython] Al_element003  label="Al_element : 0.012"  # scripted group (container) (typed FeaturePython)
  n = 0.011644
FEATURE [App::DocumentObjectGroupPython] Si_element003  label="Si_element : 0.377"  # scripted group (container) (typed FeaturePython)
  n = 0.377219
FEATURE [App::DocumentObjectGroupPython] K_element004  label="K_element : 0.014"  # scripted group (container) (typed FeaturePython)
  n = 0.00332099
FEATURE [App::DocumentObjectGroupPython] G4_Pyrex_Glass  # scripted group (container) (typed FeaturePython)
  Dunit = g/cm3
  Dvalue = 2.23
  Group = -> [B_element004,O_element043,Na_element008,Al_element003,Si_element003,K_element004]
  conduct = 2
  density = 1
  expand = 3
  formula = G4_Pyrex_Glass
  name = G4_Pyrex_Glass
  specific = 4
FEATURE [App::DocumentObjectGroupPython] O_element044  label="O_element : 0.156"  # scripted group (container) (typed FeaturePython)
  n = 0.156453
FEATURE [App::DocumentObjectGroupPython] Si_element004  label="Si_element : 0.081"  # scripted group (container) (typed FeaturePython)
  n = 0.080866
FEATURE [App::DocumentObjectGroupPython] Ti_element001  label="Ti_element : 0.008"  # scripted group (container) (typed FeaturePython)
  n = 0.008092
FEATURE [App::DocumentObjectGroupPython] As_element002  label="As_element : 0.003"  # scripted group (container) (typed FeaturePython)
  n = 0.002651
FEATURE [App::DocumentObjectGroupPython] Pb_element001  label="Pb_element : 0.752"  # scripted group (container) (typed FeaturePython)
  n = 0.751938
FEATURE [App::DocumentObjectGroupPython] G4_GLASS_LEAD  # scripted group (container) (typed FeaturePython)
  Dunit = g/cm3
  Dvalue = 6.22
  Group = -> [O_element044,Si_element004,Ti_element001,As_element002,Pb_element001]
  conduct = 2
  density = 1
  expand = 3
  formula = G4_GLASS_LEAD
  name = G4_GLASS_LEAD
  specific = 4
FEATURE [App::DocumentObjectGroupPython] O_element045  label="O_element : 0.460"  # scripted group (container) (typed FeaturePython)
  n = 0.4598
FEATURE [App::DocumentObjectGroupPython] Na_element009  label="Na_element : 0.096"  # scripted group (container) (typed FeaturePython)
  n = 0.0964411
FEATURE [App::DocumentObjectGroupPython] Si_element005  label="Si_element : 0.378"  # scripted group (container) (typed FeaturePython)
  n = 0.336553
FEATURE [App::DocumentObjectGroupPython] Ca_element011  label="Ca_element : 0.107"  # scripted group (container) (typed FeaturePython)
  n = 0.107205
FEATURE [App::DocumentObjectGroupPython] G4_GLASS_PLATE  # scripted group (container) (typed FeaturePython)
  Dunit = g/cm3
  Dvalue = 2.4
  Group = -> [O_element045,Na_element009,Si_element005,Ca_element011]
  conduct = 2
  density = 1
  expand = 3
  formula = G4_GLASS_PLATE
  name = G4_GLASS_PLATE
  specific = 4
FEATURE [App::DocumentObjectGroupPython] C_element049  label="C_element : 026"  # scripted group (container) (typed FeaturePython)
  n = 5
  ref = C_element
FEATURE [App::DocumentObjectGroupPython] H_element042  label="H_element : 021"  # scripted group (container) (typed FeaturePython)
  n = 10
  ref = H_element
FEATURE [App::DocumentObjectGroupPython] N_element019  label="N_element : 2"  # scripted group (container) (typed FeaturePython)
  n = 2
  ref = N_element
FEATURE [App::DocumentObjectGroupPython] O_element046  label="O_element : 022"  # scripted group (container) (typed FeaturePython)
  n = 3
  ref = O_element
FEATURE [App::DocumentObjectGroupPython] G4_GLUTAMINE  # scripted group (container) (typed FeaturePython)
  Dunit = g/cm3
  Dvalue = 1.46
  Group = -> [C_element049,H_element042,N_element019,O_element046]
  conduct = 2
  density = 1
  expand = 3
  formula = G4_GLUTAMINE
  name = G4_GLUTAMINE
  specific = 4
FEATURE [App::DocumentObjectGroupPython] C_element050  label="C_element : 027"  # scripted group (container) (typed FeaturePython)
  n = 3
  ref = C_element
FEATURE [App::DocumentObjectGroupPython] H_element043  label="H_element : 022"  # scripted group (container) (typed FeaturePython)
  n = 8
  ref = H_element
FEATURE [App::DocumentObjectGroupPython] O_element047  label="O_element : 023"  # scripted group (container) (typed FeaturePython)
  n = 3
  ref = O_element
FEATURE [App::DocumentObjectGroupPython] G4_GLYCEROL  # scripted group (container) (typed FeaturePython)
  Dunit = g/cm3
  Dvalue = 1.2613
  Group = -> [C_element050,H_element043,O_element047]
  conduct = 2
  density = 1
  expand = 3
  formula = G4_GLYCEROL
  name = G4_GLYCEROL
  specific = 4
FEATURE [App::DocumentObjectGroupPython] C_element051  label="C_element : 028"  # scripted group (container) (typed FeaturePython)
  n = 5
  ref = C_element
FEATURE [App::DocumentObjectGroupPython] H_element044  label="H_element : 023"  # scripted group (container) (typed FeaturePython)
  n = 5
  ref = H_element
FEATURE [App::DocumentObjectGroupPython] N_element020  label="N_element : 009"  # scripted group (container) (typed FeaturePython)
  n = 5
  ref = N_element
FEATURE [App::DocumentObjectGroupPython] O_element048  label="O_element : 024"  # scripted group (container) (typed FeaturePython)
  n = 1
  ref = O_element
FEATURE [App::DocumentObjectGroupPython] G4_GUANINE  # scripted group (container) (typed FeaturePython)
  Dunit = g/cm3
  Dvalue = 2.2
  Group = -> [C_element051,H_element044,N_element020,O_element048]
  conduct = 2
  density = 1
  expand = 3
  formula = G4_GUANINE
  name = G4_GUANINE
  specific = 4
FEATURE [App::DocumentObjectGroupPython] Ca_element012  label="Ca_element : 006"  # scripted group (container) (typed FeaturePython)
  n = 1
  ref = Ca_element
FEATURE [App::DocumentObjectGroupPython] S_element014  label="S_element : 005"  # scripted group (container) (typed FeaturePython)
  n = 1
  ref = S_element
FEATURE [App::DocumentObjectGroupPython] O_element049  label="O_element : 6"  # scripted group (container) (typed FeaturePython)
  n = 6
  ref = O_element
FEATURE [App::DocumentObjectGroupPython] H_element045  label="H_element : 024"  # scripted group (container) (typed FeaturePython)
  n = 4
  ref = H_element
FEATURE [App::DocumentObjectGroupPython] G4_GYPSUM  # scripted group (container) (typed FeaturePython)
  Dunit = g/cm3
  Dvalue = 2.32
  Group = -> [Ca_element012,S_element014,O_element049,H_element045]
  conduct = 2
  density = 1
  expand = 3
  formula = G4_GYPSUM
  name = G4_GYPSUM
  specific = 4
FEATURE [App::DocumentObjectGroupPython] C_element052  label="C_element : 7"  # scripted group (container) (typed FeaturePython)
  n = 7
  ref = C_element
FEATURE [App::DocumentObjectGroupPython] H_element046  label="H_element : 16"  # scripted group (container) (typed FeaturePython)
  n = 16
  ref = H_element
FEATURE [App::DocumentObjectGroupPython] G4_N_HEPTANE  label="G4_N-HEPTANE"  # scripted group (container) (typed FeaturePython)
  Dunit = g/cm3
  Dvalue = 0.68376
  Group = -> [C_element052,H_element046]
  conduct = 2
  density = 1
  expand = 3
  formula = G4_N-HEPTANE
  name = G4_N-HEPTANE
  specific = 4
FEATURE [App::DocumentObjectGroupPython] C_element053  label="C_element : 029"  # scripted group (container) (typed FeaturePython)
  n = 6
  ref = C_element
FEATURE [App::DocumentObjectGroupPython] H_element047  label="H_element : 14"  # scripted group (container) (typed FeaturePython)
  n = 14
  ref = H_element
FEATURE [App::DocumentObjectGroupPython] G4_N_HEXANE  label="G4_N-HEXANE"  # scripted group (container) (typed FeaturePython)
  Dunit = g/cm3
  Dvalue = 0.6603
  Group = -> [C_element053,H_element047]
  conduct = 2
  density = 1
  expand = 3
  formula = G4_N-HEXANE
  name = G4_N-HEXANE
  specific = 4
FEATURE [App::DocumentObjectGroupPython] C_element054  label="C_element : 22"  # scripted group (container) (typed FeaturePython)
  n = 22
  ref = C_element
FEATURE [App::DocumentObjectGroupPython] H_element048  label="H_element : 025"  # scripted group (container) (typed FeaturePython)
  n = 10
  ref = H_element
FEATURE [App::DocumentObjectGroupPython] N_element021  label="N_element : 010"  # scripted group (container) (typed FeaturePython)
  n = 2
  ref = N_element
FEATURE [App::DocumentObjectGroupPython] O_element050  label="O_element : 025"  # scripted group (container) (typed FeaturePython)
  n = 5
  ref = O_element
FEATURE [App::DocumentObjectGroupPython] G4_KAPTON  # scripted group (container) (typed FeaturePython)
  Dunit = g/cm3
  Dvalue = 1.42
  Group = -> [C_element054,H_element048,N_element021,O_element050]
  conduct = 2
  density = 1
  expand = 3
  formula = G4_KAPTON
  name = G4_KAPTON
  specific = 4
FEATURE [App::DocumentObjectGroupPython] La_element001  label="La_element : 1"  # scripted group (container) (typed FeaturePython)
  n = 1
  ref = La_element
FEATURE [App::DocumentObjectGroupPython] Br_element003  label="Br_element : 002"  # scripted group (container) (typed FeaturePython)
  n = 1
  ref = Br_element
FEATURE [App::DocumentObjectGroupPython] O_element051  label="O_element : 026"  # scripted group (container) (typed FeaturePython)
  n = 1
  ref = O_element
FEATURE [App::DocumentObjectGroupPython] G4_LANTHANUM_OXYBROMIDE  # scripted group (container) (typed FeaturePython)
  Dunit = g/cm3
  Dvalue = 6.28
  Group = -> [La_element001,Br_element003,O_element051]
  conduct = 2
  density = 1
  expand = 3
  formula = G4_LANTHANUM_OXYBROMIDE
  name = G4_LANTHANUM_OXYBROMIDE
  specific = 4
FEATURE [App::DocumentObjectGroupPython] La_element002  label="La_element : 2"  # scripted group (container) (typed FeaturePython)
  n = 2
  ref = La_element
FEATURE [App::DocumentObjectGroupPython] O_element052  label="O_element : 027"  # scripted group (container) (typed FeaturePython)
  n = 2
  ref = O_element
FEATURE [App::DocumentObjectGroupPython] S_element015  label="S_element : 006"  # scripted group (container) (typed FeaturePython)
  n = 1
  ref = S_element
FEATURE [App::DocumentObjectGroupPython] G4_LANTHANUM_OXYSULFIDE  # scripted group (container) (typed FeaturePython)
  Dunit = g/cm3
  Dvalue = 5.86
  Group = -> [La_element002,O_element052,S_element015]
  conduct = 2
  density = 1
  expand = 3
  formula = G4_LANTHANUM_OXYSULFIDE
  name = G4_LANTHANUM_OXYSULFIDE
  specific = 4
FEATURE [App::DocumentObjectGroupPython] O_element053  label="O_element : 0.072"  # scripted group (container) (typed FeaturePython)
  n = 0.071682
FEATURE [App::DocumentObjectGroupPython] Pb_element002  label="Pb_element : 0.928"  # scripted group (container) (typed FeaturePython)
  n = 0.928318
FEATURE [App::DocumentObjectGroupPython] G4_LEAD_OXIDE  # scripted group (container) (typed FeaturePython)
  Dunit = g/cm3
  Dvalue = 9.53
  Group = -> [O_element053,Pb_element002]
  conduct = 2
  density = 1
  expand = 3
  formula = G4_LEAD_OXIDE
  name = G4_LEAD_OXIDE
  specific = 4
FEATURE [App::DocumentObjectGroupPython] Li_element001  label="Li_element : 1"  # scripted group (container) (typed FeaturePython)
  n = 1
  ref = Li_element
FEATURE [App::DocumentObjectGroupPython] N_element022  label="N_element : 011"  # scripted group (container) (typed FeaturePython)
  n = 1
  ref = N_element
FEATURE [App::DocumentObjectGroupPython] H_element049  label="H_element : 026"  # scripted group (container) (typed FeaturePython)
  n = 2
  ref = H_element
FEATURE [App::DocumentObjectGroupPython] G4_LITHIUM_AMIDE  # scripted group (container) (typed FeaturePython)
  Dunit = g/cm3
  Dvalue = 1.178
  Group = -> [Li_element001,N_element022,H_element049]
  conduct = 2
  density = 1
  expand = 3
  formula = G4_LITHIUM_AMIDE
  name = G4_LITHIUM_AMIDE
  specific = 4
FEATURE [App::DocumentObjectGroupPython] Li_element002  label="Li_element : 2"  # scripted group (container) (typed FeaturePython)
  n = 2
  ref = Li_element
FEATURE [App::DocumentObjectGroupPython] C_element055  label="C_element : 030"  # scripted group (container) (typed FeaturePython)
  n = 1
  ref = C_element
FEATURE [App::DocumentObjectGroupPython] O_element054  label="O_element : 028"  # scripted group (container) (typed FeaturePython)
  n = 3
  ref = O_element
FEATURE [App::DocumentObjectGroupPython] G4_LITHIUM_CARBONATE  # scripted group (container) (typed FeaturePython)
  Dunit = g/cm3
  Dvalue = 2.11
  Group = -> [Li_element002,C_element055,O_element054]
  conduct = 2
  density = 1
  expand = 3
  formula = G4_LITHIUM_CARBONATE
  name = G4_LITHIUM_CARBONATE
  specific = 4
FEATURE [App::DocumentObjectGroupPython] Li_element003  label="Li_element : 003"  # scripted group (container) (typed FeaturePython)
  n = 1
  ref = Li_element
FEATURE [App::DocumentObjectGroupPython] F_element012  label="F_element : 004"  # scripted group (container) (typed FeaturePython)
  n = 1
  ref = F_element
FEATURE [App::DocumentObjectGroupPython] G4_LITHIUM_FLUORIDE  # scripted group (container) (typed FeaturePython)
  Dunit = g/cm3
  Dvalue = 2.635
  Group = -> [Li_element003,F_element012]
  conduct = 2
  density = 1
  expand = 3
  formula = G4_LITHIUM_FLUORIDE
  name = G4_LITHIUM_FLUORIDE
  specific = 4
FEATURE [App::DocumentObjectGroupPython] Li_element004  label="Li_element : 004"  # scripted group (container) (typed FeaturePython)
  n = 1
  ref = Li_element
FEATURE [App::DocumentObjectGroupPython] H_element050  label="H_element : 027"  # scripted group (container) (typed FeaturePython)
  n = 1
  ref = H_element
FEATURE [App::DocumentObjectGroupPython] G4_LITHIUM_HYDRIDE  # scripted group (container) (typed FeaturePython)
  Dunit = g/cm3
  Dvalue = 0.82
  Group = -> [Li_element004,H_element050]
  conduct = 2
  density = 1
  expand = 3
  formula = G4_LITHIUM_HYDRIDE
  name = G4_LITHIUM_HYDRIDE
  specific = 4
FEATURE [App::DocumentObjectGroupPython] Li_element005  label="Li_element : 005"  # scripted group (container) (typed FeaturePython)
  n = 1
  ref = Li_element
FEATURE [App::DocumentObjectGroupPython] I_element003  label="I_element : 002"  # scripted group (container) (typed FeaturePython)
  n = 1
  ref = I_element
FEATURE [App::DocumentObjectGroupPython] G4_LITHIUM_IODIDE  # scripted group (container) (typed FeaturePython)
  Dunit = g/cm3
  Dvalue = 3.494
  Group = -> [Li_element005,I_element003]
  conduct = 2
  density = 1
  expand = 3
  formula = G4_LITHIUM_IODIDE
  name = G4_LITHIUM_IODIDE
  specific = 4
FEATURE [App::DocumentObjectGroupPython] Li_element006  label="Li_element : 006"  # scripted group (container) (typed FeaturePython)
  n = 2
  ref = Li_element
FEATURE [App::DocumentObjectGroupPython] O_element055  label="O_element : 029"  # scripted group (container) (typed FeaturePython)
  n = 1
  ref = O_element
FEATURE [App::DocumentObjectGroupPython] G4_LITHIUM_OXIDE  # scripted group (container) (typed FeaturePython)
  Dunit = g/cm3
  Dvalue = 2.013
  Group = -> [Li_element006,O_element055]
  conduct = 2
  density = 1
  expand = 3
  formula = G4_LITHIUM_OXIDE
  name = G4_LITHIUM_OXIDE
  specific = 4
FEATURE [App::DocumentObjectGroupPython] Li_element007  label="Li_element : 007"  # scripted group (container) (typed FeaturePython)
  n = 2
  ref = Li_element
FEATURE [App::DocumentObjectGroupPython] B_element005  label="B_element : 005"  # scripted group (container) (typed FeaturePython)
  n = 4
  ref = B_element
FEATURE [App::DocumentObjectGroupPython] O_element056  label="O_element : 7"  # scripted group (container) (typed FeaturePython)
  n = 7
  ref = O_element
FEATURE [App::DocumentObjectGroupPython] G4_LITHIUM_TETRABORATE  # scripted group (container) (typed FeaturePython)
  Dunit = g/cm3
  Dvalue = 2.44
  Group = -> [Li_element007,B_element005,O_element056]
  conduct = 2
  density = 1
  expand = 3
  formula = G4_LITHIUM_TETRABORATE
  name = G4_LITHIUM_TETRABORATE
  specific = 4
FEATURE [App::DocumentObjectGroupPython] H_element051  label="H_element : 0.105"  # scripted group (container) (typed FeaturePython)
  n = 0.105
FEATURE [App::DocumentObjectGroupPython] C_element056  label="C_element : 0.083"  # scripted group (container) (typed FeaturePython)
  n = 0.083
FEATURE [App::DocumentObjectGroupPython] N_element023  label="N_element : 0.023"  # scripted group (container) (typed FeaturePython)
  n = 0.023
FEATURE [App::DocumentObjectGroupPython] O_element057  label="O_element : 0.779"  # scripted group (container) (typed FeaturePython)
  n = 0.779
FEATURE [App::DocumentObjectGroupPython] Na_element010  label="Na_element : 0.097"  # scripted group (container) (typed FeaturePython)
  n = 0.002
FEATURE [App::DocumentObjectGroupPython] P_element006  label="P_element : 0.105"  # scripted group (container) (typed FeaturePython)
  n = 0.001
FEATURE [App::DocumentObjectGroupPython] S_element016  label="S_element : 0.017"  # scripted group (container) (typed FeaturePython)
  n = 0.002
FEATURE [App::DocumentObjectGroupPython] Cl_element014  label="Cl_element : 0.587"  # scripted group (container) (typed FeaturePython)
  n = 0.003
FEATURE [App::DocumentObjectGroupPython] K_element005  label="K_element : 0.015"  # scripted group (container) (typed FeaturePython)
  n = 0.002
FEATURE [App::DocumentObjectGroupPython] G4_LUNG_ICRP  # scripted group (container) (typed FeaturePython)
  Dunit = g/cm3
  Dvalue = 1.04
  Group = -> [H_element051,C_element056,N_element023,O_element057,Na_element010,P_element006,S_element016,Cl_element014,K_element005]
  conduct = 2
  density = 1
  expand = 3
  formula = G4_LUNG_ICRP
  name = G4_LUNG_ICRP
  specific = 4
FEATURE [App::DocumentObjectGroupPython] H_element052  label="H_element : 0.116"  # scripted group (container) (typed FeaturePython)
  n = 0.114318
FEATURE [App::DocumentObjectGroupPython] C_element057  label="C_element : 0.656"  # scripted group (container) (typed FeaturePython)
  n = 0.655824
FEATURE [App::DocumentObjectGroupPython] O_element058  label="O_element : 0.092"  # scripted group (container) (typed FeaturePython)
  n = 0.0921831
FEATURE [App::DocumentObjectGroupPython] Mg_element004  label="Mg_element : 0.135"  # scripted group (container) (typed FeaturePython)
  n = 0.134792
FEATURE [App::DocumentObjectGroupPython] Ca_element013  label="Ca_element : 0.003"  # scripted group (container) (typed FeaturePython)
  n = 0.002883
FEATURE [App::DocumentObjectGroupPython] G4_M3_WAX  # scripted group (container) (typed FeaturePython)
  Dunit = g/cm3
  Dvalue = 1.05
  Group = -> [H_element052,C_element057,O_element058,Mg_element004,Ca_element013]
  conduct = 2
  density = 1
  expand = 3
  formula = G4_M3_WAX
  name = G4_M3_WAX
  specific = 4
FEATURE [App::DocumentObjectGroupPython] Mg_element005  label="Mg_element : 1"  # scripted group (container) (typed FeaturePython)
  n = 1
  ref = Mg_element
FEATURE [App::DocumentObjectGroupPython] C_element058  label="C_element : 031"  # scripted group (container) (typed FeaturePython)
  n = 1
  ref = C_element
FEATURE [App::DocumentObjectGroupPython] O_element059  label="O_element : 030"  # scripted group (container) (typed FeaturePython)
  n = 3
  ref = O_element
FEATURE [App::DocumentObjectGroupPython] G4_MAGNESIUM_CARBONATE  # scripted group (container) (typed FeaturePython)
  Dunit = g/cm3
  Dvalue = 2.958
  Group = -> [Mg_element005,C_element058,O_element059]
  conduct = 2
  density = 1
  expand = 3
  formula = G4_MAGNESIUM_CARBONATE
  name = G4_MAGNESIUM_CARBONATE
  specific = 4
FEATURE [App::DocumentObjectGroupPython] Mg_element006  label="Mg_element : 002"  # scripted group (container) (typed FeaturePython)
  n = 1
  ref = Mg_element
FEATURE [App::DocumentObjectGroupPython] F_element013  label="F_element : 005"  # scripted group (container) (typed FeaturePython)
  n = 2
  ref = F_element
FEATURE [App::DocumentObjectGroupPython] G4_MAGNESIUM_FLUORIDE  # scripted group (container) (typed FeaturePython)
  Dunit = g/cm3
  Dvalue = 3
  Group = -> [Mg_element006,F_element013]
  conduct = 2
  density = 1
  expand = 3
  formula = G4_MAGNESIUM_FLUORIDE
  name = G4_MAGNESIUM_FLUORIDE
  specific = 4
FEATURE [App::DocumentObjectGroupPython] Mg_element007  label="Mg_element : 003"  # scripted group (container) (typed FeaturePython)
  n = 1
  ref = Mg_element
FEATURE [App::DocumentObjectGroupPython] O_element060  label="O_element : 031"  # scripted group (container) (typed FeaturePython)
  n = 1
  ref = O_element
FEATURE [App::DocumentObjectGroupPython] G4_MAGNESIUM_OXIDE  # scripted group (container) (typed FeaturePython)
  Dunit = g/cm3
  Dvalue = 3.58
  Group = -> [Mg_element007,O_element060]
  conduct = 2
  density = 1
  expand = 3
  formula = G4_MAGNESIUM_OXIDE
  name = G4_MAGNESIUM_OXIDE
  specific = 4
FEATURE [App::DocumentObjectGroupPython] Mg_element008  label="Mg_element : 004"  # scripted group (container) (typed FeaturePython)
  n = 1
  ref = Mg_element
FEATURE [App::DocumentObjectGroupPython] B_element006  label="B_element : 006"  # scripted group (container) (typed FeaturePython)
  n = 4
  ref = B_element
FEATURE [App::DocumentObjectGroupPython] O_element061  label="O_element : 032"  # scripted group (container) (typed FeaturePython)
  n = 7
  ref = O_element
FEATURE [App::DocumentObjectGroupPython] G4_MAGNESIUM_TETRABORATE  # scripted group (container) (typed FeaturePython)
  Dunit = g/cm3
  Dvalue = 2.53
  Group = -> [Mg_element008,B_element006,O_element061]
  conduct = 2
  density = 1
  expand = 3
  formula = G4_MAGNESIUM_TETRABORATE
  name = G4_MAGNESIUM_TETRABORATE
  specific = 4
FEATURE [App::DocumentObjectGroupPython] Hg_element001  label="Hg_element : 1"  # scripted group (container) (typed FeaturePython)
  n = 1
  ref = Hg_element
FEATURE [App::DocumentObjectGroupPython] I_element004  label="I_element : 2"  # scripted group (container) (typed FeaturePython)
  n = 2
  ref = I_element
FEATURE [App::DocumentObjectGroupPython] G4_MERCURIC_IODIDE  # scripted group (container) (typed FeaturePython)
  Dunit = g/cm3
  Dvalue = 6.36
  Group = -> [Hg_element001,I_element004]
  conduct = 2
  density = 1
  expand = 3
  formula = G4_MERCURIC_IODIDE
  name = G4_MERCURIC_IODIDE
  specific = 4
FEATURE [App::DocumentObjectGroupPython] C_element059  label="C_element : 032"  # scripted group (container) (typed FeaturePython)
  n = 1
  ref = C_element
FEATURE [App::DocumentObjectGroupPython] H_element053  label="H_element : 028"  # scripted group (container) (typed FeaturePython)
  n = 4
  ref = H_element
FEATURE [App::DocumentObjectGroupPython] G4_METHANE  # scripted group (container) (typed FeaturePython)
  Dunit = g/cm3
  Dvalue = 0.000667151
  Group = -> [C_element059,H_element053]
  conduct = 2
  density = 1
  expand = 3
  formula = G4_METHANE
  name = G4_METHANE
  specific = 4
FEATURE [App::DocumentObjectGroupPython] C_element060  label="C_element : 033"  # scripted group (container) (typed FeaturePython)
  n = 1
  ref = C_element
FEATURE [App::DocumentObjectGroupPython] H_element054  label="H_element : 029"  # scripted group (container) (typed FeaturePython)
  n = 4
  ref = H_element
FEATURE [App::DocumentObjectGroupPython] O_element062  label="O_element : 033"  # scripted group (container) (typed FeaturePython)
  n = 1
  ref = O_element
FEATURE [App::DocumentObjectGroupPython] G4_METHANOL  # scripted group (container) (typed FeaturePython)
  Dunit = g/cm3
  Dvalue = 0.7914
  Group = -> [C_element060,H_element054,O_element062]
  conduct = 2
  density = 1
  expand = 3
  formula = G4_METHANOL
  name = G4_METHANOL
  specific = 4
FEATURE [App::DocumentObjectGroupPython] H_element055  label="H_element : 0.134"  # scripted group (container) (typed FeaturePython)
  n = 0.13404
FEATURE [App::DocumentObjectGroupPython] C_element061  label="C_element : 0.778"  # scripted group (container) (typed FeaturePython)
  n = 0.77796
FEATURE [App::DocumentObjectGroupPython] O_element063  label="O_element : 0.035"  # scripted group (container) (typed FeaturePython)
  n = 0.03502
FEATURE [App::DocumentObjectGroupPython] Mg_element009  label="Mg_element : 0.039"  # scripted group (container) (typed FeaturePython)
  n = 0.038594
FEATURE [App::DocumentObjectGroupPython] Ti_element002  label="Ti_element : 0.014"  # scripted group (container) (typed FeaturePython)
  n = 0.014386
FEATURE [App::DocumentObjectGroupPython] G4_MIX_D_WAX  # scripted group (container) (typed FeaturePython)
  Dunit = g/cm3
  Dvalue = 0.99
  Group = -> [H_element055,C_element061,O_element063,Mg_element009,Ti_element002]
  conduct = 2
  density = 1
  expand = 3
  formula = G4_MIX_D_WAX
  name = G4_MIX_D_WAX
  specific = 4
FEATURE [App::DocumentObjectGroupPython] H_element056  label="H_element : 0.135"  # scripted group (container) (typed FeaturePython)
  n = 0.081192
FEATURE [App::DocumentObjectGroupPython] C_element062  label="C_element : 0.583"  # scripted group (container) (typed FeaturePython)
  n = 0.583442
FEATURE [App::DocumentObjectGroupPython] N_element024  label="N_element : 0.018"  # scripted group (container) (typed FeaturePython)
  n = 0.017798
FEATURE [App::DocumentObjectGroupPython] O_element064  label="O_element : 0.186"  # scripted group (container) (typed FeaturePython)
  n = 0.186381
FEATURE [App::DocumentObjectGroupPython] Mg_element010  label="Mg_element : 0.130"  # scripted group (container) (typed FeaturePython)
  n = 0.130287
FEATURE [App::DocumentObjectGroupPython] Cl_element015  label="Cl_element : 0.588"  # scripted group (container) (typed FeaturePython)
  n = 0.0009
FEATURE [App::DocumentObjectGroupPython] G4_MS20_TISSUE  # scripted group (container) (typed FeaturePython)
  Dunit = g/cm3
  Dvalue = 1
  Group = -> [H_element056,C_element062,N_element024,O_element064,Mg_element010,Cl_element015]
  conduct = 2
  density = 1
  expand = 3
  formula = G4_MS20_TISSUE
  name = G4_MS20_TISSUE
  specific = 4
FEATURE [App::DocumentObjectGroupPython] H_element057  label="H_element : 0.136"  # scripted group (container) (typed FeaturePython)
  n = 0.102
FEATURE [App::DocumentObjectGroupPython] C_element063  label="C_element : 0.143"  # scripted group (container) (typed FeaturePython)
  n = 0.143
FEATURE [App::DocumentObjectGroupPython] N_element025  label="N_element : 0.034"  # scripted group (container) (typed FeaturePython)
  n = 0.034
FEATURE [App::DocumentObjectGroupPython] O_element065  label="O_element : 0.710"  # scripted group (container) (typed FeaturePython)
  n = 0.71
FEATURE [App::DocumentObjectGroupPython] Na_element011  label="Na_element : 0.098"  # scripted group (container) (typed FeaturePython)
  n = 0.001
FEATURE [App::DocumentObjectGroupPython] P_element007  label="P_element : 0.002"  # scripted group (container) (typed FeaturePython)
  n = 0.002
FEATURE [App::DocumentObjectGroupPython] S_element017  label="S_element : 0.018"  # scripted group (container) (typed FeaturePython)
  n = 0.003
FEATURE [App::DocumentObjectGroupPython] Cl_element016  label="Cl_element : 0.589"  # scripted group (container) (typed FeaturePython)
  n = 0.001
FEATURE [App::DocumentObjectGroupPython] K_element006  label="K_element : 0.004"  # scripted group (container) (typed FeaturePython)
  n = 0.004
FEATURE [App::DocumentObjectGroupPython] G4_MUSCLE_SKELETAL_ICRP  # scripted group (container) (typed FeaturePython)
  Dunit = g/cm3
  Dvalue = 1.05
  Group = -> [H_element057,C_element063,N_element025,O_element065,Na_element011,P_element007,S_element017,Cl_element016,K_element006]
  conduct = 2
  density = 1
  expand = 3
  formula = G4_MUSCLE_SKELETAL_ICRP
  name = G4_MUSCLE_SKELETAL_ICRP
  specific = 4
FEATURE [App::DocumentObjectGroupPython] H_element058  label="H_element : 0.137"  # scripted group (container) (typed FeaturePython)
  n = 0.102102
FEATURE [App::DocumentObjectGroupPython] C_element064  label="C_element : 0.123"  # scripted group (container) (typed FeaturePython)
  n = 0.123123
FEATURE [App::DocumentObjectGroupPython] N_element026  label="N_element : 0.756"  # scripted group (container) (typed FeaturePython)
  n = 0.035035
FEATURE [App::DocumentObjectGroupPython] O_element066  label="O_element : 0.730"  # scripted group (container) (typed FeaturePython)
  n = 0.72973
FEATURE [App::DocumentObjectGroupPython] Na_element012  label="Na_element : 0.099"  # scripted group (container) (typed FeaturePython)
  n = 0.001001
FEATURE [App::DocumentObjectGroupPython] P_element008  label="P_element : 0.106"  # scripted group (container) (typed FeaturePython)
  n = 0.002002
FEATURE [App::DocumentObjectGroupPython] S_element018  label="S_element : 0.019"  # scripted group (container) (typed FeaturePython)
  n = 0.004004
FEATURE [App::DocumentObjectGroupPython] K_element007  label="K_element : 0.016"  # scripted group (container) (typed FeaturePython)
  n = 0.003003
FEATURE [App::DocumentObjectGroupPython] G4_MUSCLE_STRIATED_ICRU  # scripted group (container) (typed FeaturePython)
  Dunit = g/cm3
  Dvalue = 1.04
  Group = -> [H_element058,C_element064,N_element026,O_element066,Na_element012,P_element008,S_element018,K_element007]
  conduct = 2
  density = 1
  expand = 3
  formula = G4_MUSCLE_STRIATED_ICRU
  name = G4_MUSCLE_STRIATED_ICRU
  specific = 4
FEATURE [App::DocumentObjectGroupPython] H_element059  label="H_element : 0.098"  # scripted group (container) (typed FeaturePython)
  n = 0.0982341
FEATURE [App::DocumentObjectGroupPython] C_element065  label="C_element : 0.156"  # scripted group (container) (typed FeaturePython)
  n = 0.156214
FEATURE [App::DocumentObjectGroupPython] N_element027  label="N_element : 0.757"  # scripted group (container) (typed FeaturePython)
  n = 0.035451
FEATURE [App::DocumentObjectGroupPython] O_element067  label="O_element : 0.880"  # scripted group (container) (typed FeaturePython)
  n = 0.710101
FEATURE [App::DocumentObjectGroupPython] G4_MUSCLE_WITH_SUCROSE  # scripted group (container) (typed FeaturePython)
  Dunit = g/cm3
  Dvalue = 1.11
  Group = -> [H_element059,C_element065,N_element027,O_element067]
  conduct = 2
  density = 1
  expand = 3
  formula = G4_MUSCLE_WITH_SUCROSE
  name = G4_MUSCLE_WITH_SUCROSE
  specific = 4
FEATURE [App::DocumentObjectGroupPython] H_element060  label="H_element : 0.138"  # scripted group (container) (typed FeaturePython)
  n = 0.101969
FEATURE [App::DocumentObjectGroupPython] C_element066  label="C_element : 0.120"  # scripted group (container) (typed FeaturePython)
  n = 0.120058
FEATURE [App::DocumentObjectGroupPython] N_element028  label="N_element : 0.758"  # scripted group (container) (typed FeaturePython)
  n = 0.035451
FEATURE [App::DocumentObjectGroupPython] O_element068  label="O_element : 0.743"  # scripted group (container) (typed FeaturePython)
  n = 0.742522
FEATURE [App::DocumentObjectGroupPython] G4_MUSCLE_WITHOUT_SUCROSE  # scripted group (container) (typed FeaturePython)
  Dunit = g/cm3
  Dvalue = 1.07
  Group = -> [H_element060,C_element066,N_element028,O_element068]
  conduct = 2
  density = 1
  expand = 3
  formula = G4_MUSCLE_WITHOUT_SUCROSE
  name = G4_MUSCLE_WITHOUT_SUCROSE
  specific = 4
FEATURE [App::DocumentObjectGroupPython] C_element067  label="C_element : 10"  # scripted group (container) (typed FeaturePython)
  n = 10
  ref = C_element
FEATURE [App::DocumentObjectGroupPython] H_element061  label="H_element : 030"  # scripted group (container) (typed FeaturePython)
  n = 8
  ref = H_element
FEATURE [App::DocumentObjectGroupPython] G4_NAPHTHALENE  # scripted group (container) (typed FeaturePython)
  Dunit = g/cm3
  Dvalue = 1.145
  Group = -> [C_element067,H_element061]
  conduct = 2
  density = 1
  expand = 3
  formula = G4_NAPHTHALENE
  name = G4_NAPHTHALENE
  specific = 4
FEATURE [App::DocumentObjectGroupPython] C_element068  label="C_element : 034"  # scripted group (container) (typed FeaturePython)
  n = 6
  ref = C_element
FEATURE [App::DocumentObjectGroupPython] H_element062  label="H_element : 031"  # scripted group (container) (typed FeaturePython)
  n = 5
  ref = H_element
FEATURE [App::DocumentObjectGroupPython] N_element029  label="N_element : 012"  # scripted group (container) (typed FeaturePython)
  n = 1
  ref = N_element
FEATURE [App::DocumentObjectGroupPython] O_element069  label="O_element : 034"  # scripted group (container) (typed FeaturePython)
  n = 2
  ref = O_element
FEATURE [App::DocumentObjectGroupPython] G4_NITROBENZENE  # scripted group (container) (typed FeaturePython)
  Dunit = g/cm3
  Dvalue = 1.19867
  Group = -> [C_element068,H_element062,N_element029,O_element069]
  conduct = 2
  density = 1
  expand = 3
  formula = G4_NITROBENZENE
  name = G4_NITROBENZENE
  specific = 4
FEATURE [App::DocumentObjectGroupPython] N_element030  label="N_element : 013"  # scripted group (container) (typed FeaturePython)
  n = 2
  ref = N_element
FEATURE [App::DocumentObjectGroupPython] O_element070  label="O_element : 035"  # scripted group (container) (typed FeaturePython)
  n = 1
  ref = O_element
FEATURE [App::DocumentObjectGroupPython] G4_NITROUS_OXIDE  # scripted group (container) (typed FeaturePython)
  Dunit = g/cm3
  Dvalue = 0.00183094
  Group = -> [N_element030,O_element070]
  conduct = 2
  density = 1
  expand = 3
  formula = G4_NITROUS_OXIDE
  name = G4_NITROUS_OXIDE
  specific = 4
FEATURE [App::DocumentObjectGroupPython] H_element063  label="H_element : 0.104"  # scripted group (container) (typed FeaturePython)
  n = 0.103509
FEATURE [App::DocumentObjectGroupPython] C_element069  label="C_element : 0.648"  # scripted group (container) (typed FeaturePython)
  n = 0.648416
FEATURE [App::DocumentObjectGroupPython] N_element031  label="N_element : 0.100"  # scripted group (container) (typed FeaturePython)
  n = 0.0995361
FEATURE [App::DocumentObjectGroupPython] O_element071  label="O_element : 0.149"  # scripted group (container) (typed FeaturePython)
  n = 0.148539
FEATURE [App::DocumentObjectGroupPython] G4_NYLON_8062  label="G4_NYLON-8062"  # scripted group (container) (typed FeaturePython)
  Dunit = g/cm3
  Dvalue = 1.08
  Group = -> [H_element063,C_element069,N_element031,O_element071]
  conduct = 2
  density = 1
  expand = 3
  formula = G4_NYLON-8062
  name = G4_NYLON-8062
  specific = 4
FEATURE [App::DocumentObjectGroupPython] C_element070  label="C_element : 035"  # scripted group (container) (typed FeaturePython)
  n = 6
  ref = C_element
FEATURE [App::DocumentObjectGroupPython] H_element064  label="H_element : 11"  # scripted group (container) (typed FeaturePython)
  n = 11
  ref = H_element
FEATURE [App::DocumentObjectGroupPython] N_element032  label="N_element : 014"  # scripted group (container) (typed FeaturePython)
  n = 1
  ref = N_element
FEATURE [App::DocumentObjectGroupPython] O_element072  label="O_element : 036"  # scripted group (container) (typed FeaturePython)
  n = 1
  ref = O_element
FEATURE [App::DocumentObjectGroupPython] G4_NYLON_6_6  label="G4_NYLON-6-6"  # scripted group (container) (typed FeaturePython)
  Dunit = g/cm3
  Dvalue = 1.14
  Group = -> [C_element070,H_element064,N_element032,O_element072]
  conduct = 2
  density = 1
  expand = 3
  formula = G4_NYLON-6-6
  name = G4_NYLON-6-6
  specific = 4
FEATURE [App::DocumentObjectGroupPython] H_element065  label="H_element : 0.139"  # scripted group (container) (typed FeaturePython)
  n = 0.107062
FEATURE [App::DocumentObjectGroupPython] C_element071  label="C_element : 0.680"  # scripted group (container) (typed FeaturePython)
  n = 0.680449
FEATURE [App::DocumentObjectGroupPython] N_element033  label="N_element : 0.099"  # scripted group (container) (typed FeaturePython)
  n = 0.099189
FEATURE [App::DocumentObjectGroupPython] O_element073  label="O_element : 0.113"  # scripted group (container) (typed FeaturePython)
  n = 0.1133
FEATURE [App::DocumentObjectGroupPython] G4_NYLON_6_10  label="G4_NYLON-6-10"  # scripted group (container) (typed FeaturePython)
  Dunit = g/cm3
  Dvalue = 1.14
  Group = -> [H_element065,C_element071,N_element033,O_element073]
  conduct = 2
  density = 1
  expand = 3
  formula = G4_NYLON-6-10
  name = G4_NYLON-6-10
  specific = 4
FEATURE [App::DocumentObjectGroupPython] H_element066  label="H_element : 0.140"  # scripted group (container) (typed FeaturePython)
  n = 0.115476
FEATURE [App::DocumentObjectGroupPython] C_element072  label="C_element : 0.721"  # scripted group (container) (typed FeaturePython)
  n = 0.720818
FEATURE [App::DocumentObjectGroupPython] N_element034  label="N_element : 0.076"  # scripted group (container) (typed FeaturePython)
  n = 0.0764169
FEATURE [App::DocumentObjectGroupPython] O_element074  label="O_element : 0.087"  # scripted group (container) (typed FeaturePython)
  n = 0.0872889
FEATURE [App::DocumentObjectGroupPython] G4_NYLON_11_RILSAN  label="G4_NYLON-11_RILSAN"  # scripted group (container) (typed FeaturePython)
  Dunit = g/cm3
  Dvalue = 1.425
  Group = -> [H_element066,C_element072,N_element034,O_element074]
  conduct = 2
  density = 1
  expand = 3
  formula = G4_NYLON-11_RILSAN
  name = G4_NYLON-11_RILSAN
  specific = 4
FEATURE [App::DocumentObjectGroupPython] C_element073  label="C_element : 8"  # scripted group (container) (typed FeaturePython)
  n = 8
  ref = C_element
FEATURE [App::DocumentObjectGroupPython] H_element067  label="H_element : 18"  # scripted group (container) (typed FeaturePython)
  n = 18
  ref = H_element
FEATURE [App::DocumentObjectGroupPython] G4_OCTANE  # scripted group (container) (typed FeaturePython)
  Dunit = g/cm3
  Dvalue = 0.7026
  Group = -> [C_element073,H_element067]
  conduct = 2
  density = 1
  expand = 3
  formula = G4_OCTANE
  name = G4_OCTANE
  specific = 4
FEATURE [App::DocumentObjectGroupPython] C_element074  label="C_element : 25"  # scripted group (container) (typed FeaturePython)
  n = 25
  ref = C_element
FEATURE [App::DocumentObjectGroupPython] H_element068  label="H_element : 52"  # scripted group (container) (typed FeaturePython)
  n = 52
  ref = H_element
FEATURE [App::DocumentObjectGroupPython] G4_PARAFFIN  # scripted group (container) (typed FeaturePython)
  Dunit = g/cm3
  Dvalue = 0.93
  Group = -> [C_element074,H_element068]
  conduct = 2
  density = 1
  expand = 3
  formula = G4_PARAFFIN
  name = G4_PARAFFIN
  specific = 4
FEATURE [App::DocumentObjectGroupPython] C_element075  label="C_element : 036"  # scripted group (container) (typed FeaturePython)
  n = 5
  ref = C_element
FEATURE [App::DocumentObjectGroupPython] H_element069  label="H_element : 032"  # scripted group (container) (typed FeaturePython)
  n = 12
  ref = H_element
FEATURE [App::DocumentObjectGroupPython] G4_N_PENTANE  label="G4_N-PENTANE"  # scripted group (container) (typed FeaturePython)
  Dunit = g/cm3
  Dvalue = 0.6262
  Group = -> [C_element075,H_element069]
  conduct = 2
  density = 1
  expand = 3
  formula = G4_N-PENTANE
  name = G4_N-PENTANE
  specific = 4
FEATURE [App::DocumentObjectGroupPython] H_element070  label="H_element : 0.014"  # scripted group (container) (typed FeaturePython)
  n = 0.0141
FEATURE [App::DocumentObjectGroupPython] C_element076  label="C_element : 0.072"  # scripted group (container) (typed FeaturePython)
  n = 0.072261
FEATURE [App::DocumentObjectGroupPython] N_element035  label="N_element : 0.019"  # scripted group (container) (typed FeaturePython)
  n = 0.01932
FEATURE [App::DocumentObjectGroupPython] O_element075  label="O_element : 0.066"  # scripted group (container) (typed FeaturePython)
  n = 0.066101
FEATURE [App::DocumentObjectGroupPython] S_element019  label="S_element : 0.020"  # scripted group (container) (typed FeaturePython)
  n = 0.00189
FEATURE [App::DocumentObjectGroupPython] Br_element004  label="Br_element : 0.349"  # scripted group (container) (typed FeaturePython)
  n = 0.349103
FEATURE [App::DocumentObjectGroupPython] Ag_element001  label="Ag_element : 0.474"  # scripted group (container) (typed FeaturePython)
  n = 0.474105
FEATURE [App::DocumentObjectGroupPython] I_element005  label="I_element : 0.003"  # scripted group (container) (typed FeaturePython)
  n = 0.00312
FEATURE [App::DocumentObjectGroupPython] G4_PHOTO_EMULSION  # scripted group (container) (typed FeaturePython)
  Dunit = g/cm3
  Dvalue = 3.815
  Group = -> [H_element070,C_element076,N_element035,O_element075,S_element019,Br_element004,Ag_element001,I_element005]
  conduct = 2
  density = 1
  expand = 3
  formula = G4_PHOTO_EMULSION
  name = G4_PHOTO_EMULSION
  specific = 4
FEATURE [App::DocumentObjectGroupPython] C_element077  label="C_element : 9"  # scripted group (container) (typed FeaturePython)
  n = 9
  ref = C_element
FEATURE [App::DocumentObjectGroupPython] H_element071  label="H_element : 033"  # scripted group (container) (typed FeaturePython)
  n = 10
  ref = H_element
FEATURE [App::DocumentObjectGroupPython] G4_PLASTIC_SC_VINYLTOLUENE  # scripted group (container) (typed FeaturePython)
  Dunit = g/cm3
  Dvalue = 1.032
  Group = -> [C_element077,H_element071]
  conduct = 2
  density = 1
  expand = 3
  formula = G4_PLASTIC_SC_VINYLTOLUENE
  name = G4_PLASTIC_SC_VINYLTOLUENE
  specific = 4
FEATURE [App::DocumentObjectGroupPython] Pu_element001  label="Pu_element : 1"  # scripted group (container) (typed FeaturePython)
  n = 1
  ref = Pu_element
FEATURE [App::DocumentObjectGroupPython] O_element076  label="O_element : 037"  # scripted group (container) (typed FeaturePython)
  n = 2
  ref = O_element
FEATURE [App::DocumentObjectGroupPython] G4_PLUTONIUM_DIOXIDE  # scripted group (container) (typed FeaturePython)
  Dunit = g/cm3
  Dvalue = 11.46
  Group = -> [Pu_element001,O_element076]
  conduct = 2
  density = 1
  expand = 3
  formula = G4_PLUTONIUM_DIOXIDE
  name = G4_PLUTONIUM_DIOXIDE
  specific = 4
FEATURE [App::DocumentObjectGroupPython] C_element078  label="C_element : 037"  # scripted group (container) (typed FeaturePython)
  n = 3
  ref = C_element
FEATURE [App::DocumentObjectGroupPython] H_element072  label="H_element : 034"  # scripted group (container) (typed FeaturePython)
  n = 3
  ref = H_element
FEATURE [App::DocumentObjectGroupPython] N_element036  label="N_element : 015"  # scripted group (container) (typed FeaturePython)
  n = 1
  ref = N_element
FEATURE [App::DocumentObjectGroupPython] G4_POLYACRYLONITRILE  # scripted group (container) (typed FeaturePython)
  Dunit = g/cm3
  Dvalue = 1.17
  Group = -> [C_element078,H_element072,N_element036]
  conduct = 2
  density = 1
  expand = 3
  formula = G4_POLYACRYLONITRILE
  name = G4_POLYACRYLONITRILE
  specific = 4
FEATURE [App::DocumentObjectGroupPython] C_element079  label="C_element : 16"  # scripted group (container) (typed FeaturePython)
  n = 16
  ref = C_element
FEATURE [App::DocumentObjectGroupPython] H_element073  label="H_element : 035"  # scripted group (container) (typed FeaturePython)
  n = 14
  ref = H_element
FEATURE [App::DocumentObjectGroupPython] O_element077  label="O_element : 038"  # scripted group (container) (typed FeaturePython)
  n = 3
  ref = O_element
FEATURE [App::DocumentObjectGroupPython] G4_POLYCARBONATE  # scripted group (container) (typed FeaturePython)
  Dunit = g/cm3
  Dvalue = 1.2
  Group = -> [C_element079,H_element073,O_element077]
  conduct = 2
  density = 1
  expand = 3
  formula = G4_POLYCARBONATE
  name = G4_POLYCARBONATE
  specific = 4
FEATURE [App::DocumentObjectGroupPython] C_element080  label="C_element : 038"  # scripted group (container) (typed FeaturePython)
  n = 8
  ref = C_element
FEATURE [App::DocumentObjectGroupPython] H_element074  label="H_element : 036"  # scripted group (container) (typed FeaturePython)
  n = 7
  ref = H_element
FEATURE [App::DocumentObjectGroupPython] Cl_element017  label="Cl_element : 007"  # scripted group (container) (typed FeaturePython)
  n = 1
  ref = Cl_element
FEATURE [App::DocumentObjectGroupPython] G4_POLYCHLOROSTYRENE  # scripted group (container) (typed FeaturePython)
  Dunit = g/cm3
  Dvalue = 1.3
  Group = -> [C_element080,H_element074,Cl_element017]
  conduct = 2
  density = 1
  expand = 3
  formula = G4_POLYCHLOROSTYRENE
  name = G4_POLYCHLOROSTYRENE
  specific = 4
FEATURE [App::DocumentObjectGroupPython] C_element081  label="C_element : 039"  # scripted group (container) (typed FeaturePython)
  n = 1
  ref = C_element
FEATURE [App::DocumentObjectGroupPython] H_element075  label="H_element : 037"  # scripted group (container) (typed FeaturePython)
  n = 2
  ref = H_element
FEATURE [App::DocumentObjectGroupPython] G4_POLYETHYLENE  # scripted group (container) (typed FeaturePython)
  Dunit = g/cm3
  Dvalue = 0.94
  Group = -> [C_element081,H_element075]
  conduct = 2
  density = 1
  expand = 3
  formula = G4_POLYETHYLENE
  name = G4_POLYETHYLENE
  specific = 4
FEATURE [App::DocumentObjectGroupPython] C_element082  label="C_element : 040"  # scripted group (container) (typed FeaturePython)
  n = 10
  ref = C_element
FEATURE [App::DocumentObjectGroupPython] H_element076  label="H_element : 038"  # scripted group (container) (typed FeaturePython)
  n = 8
  ref = H_element
FEATURE [App::DocumentObjectGroupPython] O_element078  label="O_element : 039"  # scripted group (container) (typed FeaturePython)
  n = 4
  ref = O_element
FEATURE [App::DocumentObjectGroupPython] G4_MYLAR  # scripted group (container) (typed FeaturePython)
  Dunit = g/cm3
  Dvalue = 1.4
  Group = -> [C_element082,H_element076,O_element078]
  conduct = 2
  density = 1
  expand = 3
  formula = G4_MYLAR
  name = G4_MYLAR
  specific = 4
FEATURE [App::DocumentObjectGroupPython] C_element083  label="C_element : 041"  # scripted group (container) (typed FeaturePython)
  n = 5
  ref = C_element
FEATURE [App::DocumentObjectGroupPython] H_element077  label="H_element : 039"  # scripted group (container) (typed FeaturePython)
  n = 8
  ref = H_element
FEATURE [App::DocumentObjectGroupPython] O_element079  label="O_element : 040"  # scripted group (container) (typed FeaturePython)
  n = 2
  ref = O_element
FEATURE [App::DocumentObjectGroupPython] G4_PLEXIGLASS  # scripted group (container) (typed FeaturePython)
  Dunit = g/cm3
  Dvalue = 1.19
  Group = -> [C_element083,H_element077,O_element079]
  conduct = 2
  density = 1
  expand = 3
  formula = G4_PLEXIGLASS
  name = G4_PLEXIGLASS
  specific = 4
FEATURE [App::DocumentObjectGroupPython] C_element084  label="C_element : 042"  # scripted group (container) (typed FeaturePython)
  n = 1
  ref = C_element
FEATURE [App::DocumentObjectGroupPython] H_element078  label="H_element : 040"  # scripted group (container) (typed FeaturePython)
  n = 2
  ref = H_element
FEATURE [App::DocumentObjectGroupPython] O_element080  label="O_element : 041"  # scripted group (container) (typed FeaturePython)
  n = 1
  ref = O_element
FEATURE [App::DocumentObjectGroupPython] G4_POLYOXYMETHYLENE  # scripted group (container) (typed FeaturePython)
  Dunit = g/cm3
  Dvalue = 1.425
  Group = -> [C_element084,H_element078,O_element080]
  conduct = 2
  density = 1
  expand = 3
  formula = G4_POLYOXYMETHYLENE
  name = G4_POLYOXYMETHYLENE
  specific = 4
FEATURE [App::DocumentObjectGroupPython] C_element085  label="C_element : 043"  # scripted group (container) (typed FeaturePython)
  n = 2
  ref = C_element
FEATURE [App::DocumentObjectGroupPython] H_element079  label="H_element : 041"  # scripted group (container) (typed FeaturePython)
  n = 4
  ref = H_element
FEATURE [App::DocumentObjectGroupPython] G4_POLYPROPYLENE  # scripted group (container) (typed FeaturePython)
  Dunit = g/cm3
  Dvalue = 0.9
  Group = -> [C_element085,H_element079]
  conduct = 2
  density = 1
  expand = 3
  formula = G4_POLYPROPYLENE
  name = G4_POLYPROPYLENE
  specific = 4
FEATURE [App::DocumentObjectGroupPython] C_element086  label="C_element : 044"  # scripted group (container) (typed FeaturePython)
  n = 8
  ref = C_element
FEATURE [App::DocumentObjectGroupPython] H_element080  label="H_element : 042"  # scripted group (container) (typed FeaturePython)
  n = 8
  ref = H_element
FEATURE [App::DocumentObjectGroupPython] G4_POLYSTYRENE  # scripted group (container) (typed FeaturePython)
  Dunit = g/cm3
  Dvalue = 1.06
  Group = -> [C_element086,H_element080]
  conduct = 2
  density = 1
  expand = 3
  formula = G4_POLYSTYRENE
  name = G4_POLYSTYRENE
  specific = 4
FEATURE [App::DocumentObjectGroupPython] C_element087  label="C_element : 045"  # scripted group (container) (typed FeaturePython)
  n = 2
  ref = C_element
FEATURE [App::DocumentObjectGroupPython] F_element014  label="F_element : 4"  # scripted group (container) (typed FeaturePython)
  n = 4
  ref = F_element
FEATURE [App::DocumentObjectGroupPython] G4_TEFLON  # scripted group (container) (typed FeaturePython)
  Dunit = g/cm3
  Dvalue = 2.2
  Group = -> [C_element087,F_element014]
  conduct = 2
  density = 1
  expand = 3
  formula = G4_TEFLON
  name = G4_TEFLON
  specific = 4
FEATURE [App::DocumentObjectGroupPython] C_element088  label="C_element : 046"  # scripted group (container) (typed FeaturePython)
  n = 2
  ref = C_element
FEATURE [App::DocumentObjectGroupPython] F_element015  label="F_element : 006"  # scripted group (container) (typed FeaturePython)
  n = 3
  ref = F_element
FEATURE [App::DocumentObjectGroupPython] Cl_element018  label="Cl_element : 008"  # scripted group (container) (typed FeaturePython)
  n = 1
  ref = Cl_element
FEATURE [App::DocumentObjectGroupPython] G4_POLYTRIFLUOROCHLOROETHYLENE  # scripted group (container) (typed FeaturePython)
  Dunit = g/cm3
  Dvalue = 2.1
  Group = -> [C_element088,F_element015,Cl_element018]
  conduct = 2
  density = 1
  expand = 3
  formula = G4_POLYTRIFLUOROCHLOROETHYLENE
  name = G4_POLYTRIFLUOROCHLOROETHYLENE
  specific = 4
FEATURE [App::DocumentObjectGroupPython] C_element089  label="C_element : 047"  # scripted group (container) (typed FeaturePython)
  n = 4
  ref = C_element
FEATURE [App::DocumentObjectGroupPython] H_element081  label="H_element : 043"  # scripted group (container) (typed FeaturePython)
  n = 6
  ref = H_element
FEATURE [App::DocumentObjectGroupPython] O_element081  label="O_element : 042"  # scripted group (container) (typed FeaturePython)
  n = 2
  ref = O_element
FEATURE [App::DocumentObjectGroupPython] G4_POLYVINYL_ACETATE  # scripted group (container) (typed FeaturePython)
  Dunit = g/cm3
  Dvalue = 1.19
  Group = -> [C_element089,H_element081,O_element081]
  conduct = 2
  density = 1
  expand = 3
  formula = G4_POLYVINYL_ACETATE
  name = G4_POLYVINYL_ACETATE
  specific = 4
FEATURE [App::DocumentObjectGroupPython] C_element090  label="C_element : 048"  # scripted group (container) (typed FeaturePython)
  n = 2
  ref = C_element
FEATURE [App::DocumentObjectGroupPython] H_element082  label="H_element : 044"  # scripted group (container) (typed FeaturePython)
  n = 4
  ref = H_element
FEATURE [App::DocumentObjectGroupPython] O_element082  label="O_element : 043"  # scripted group (container) (typed FeaturePython)
  n = 1
  ref = O_element
FEATURE [App::DocumentObjectGroupPython] G4_POLYVINYL_ALCOHOL  # scripted group (container) (typed FeaturePython)
  Dunit = g/cm3
  Dvalue = 1.3
  Group = -> [C_element090,H_element082,O_element082]
  conduct = 2
  density = 1
  expand = 3
  formula = G4_POLYVINYL_ALCOHOL
  name = G4_POLYVINYL_ALCOHOL
  specific = 4
FEATURE [App::DocumentObjectGroupPython] C_element091  label="C_element : 049"  # scripted group (container) (typed FeaturePython)
  n = 8
  ref = C_element
FEATURE [App::DocumentObjectGroupPython] H_element083  label="H_element : 045"  # scripted group (container) (typed FeaturePython)
  n = 14
  ref = H_element
FEATURE [App::DocumentObjectGroupPython] O_element083  label="O_element : 044"  # scripted group (container) (typed FeaturePython)
  n = 2
  ref = O_element
FEATURE [App::DocumentObjectGroupPython] G4_POLYVINYL_BUTYRAL  # scripted group (container) (typed FeaturePython)
  Dunit = g/cm3
  Dvalue = 1.12
  Group = -> [C_element091,H_element083,O_element083]
  conduct = 2
  density = 1
  expand = 3
  formula = G4_POLYVINYL_BUTYRAL
  name = G4_POLYVINYL_BUTYRAL
  specific = 4
FEATURE [App::DocumentObjectGroupPython] C_element092  label="C_element : 050"  # scripted group (container) (typed FeaturePython)
  n = 2
  ref = C_element
FEATURE [App::DocumentObjectGroupPython] H_element084  label="H_element : 046"  # scripted group (container) (typed FeaturePython)
  n = 3
  ref = H_element
FEATURE [App::DocumentObjectGroupPython] Cl_element019  label="Cl_element : 009"  # scripted group (container) (typed FeaturePython)
  n = 1
  ref = Cl_element
FEATURE [App::DocumentObjectGroupPython] G4_POLYVINYL_CHLORIDE  # scripted group (container) (typed FeaturePython)
  Dunit = g/cm3
  Dvalue = 1.3
  Group = -> [C_element092,H_element084,Cl_element019]
  conduct = 2
  density = 1
  expand = 3
  formula = G4_POLYVINYL_CHLORIDE
  name = G4_POLYVINYL_CHLORIDE
  specific = 4
FEATURE [App::DocumentObjectGroupPython] C_element093  label="C_element : 051"  # scripted group (container) (typed FeaturePython)
  n = 2
  ref = C_element
FEATURE [App::DocumentObjectGroupPython] H_element085  label="H_element : 047"  # scripted group (container) (typed FeaturePython)
  n = 2
  ref = H_element
FEATURE [App::DocumentObjectGroupPython] Cl_element020  label="Cl_element : 010"  # scripted group (container) (typed FeaturePython)
  n = 2
  ref = Cl_element
FEATURE [App::DocumentObjectGroupPython] G4_POLYVINYLIDENE_CHLORIDE  # scripted group (container) (typed FeaturePython)
  Dunit = g/cm3
  Dvalue = 1.7
  Group = -> [C_element093,H_element085,Cl_element020]
  conduct = 2
  density = 1
  expand = 3
  formula = G4_POLYVINYLIDENE_CHLORIDE
  name = G4_POLYVINYLIDENE_CHLORIDE
  specific = 4
FEATURE [App::DocumentObjectGroupPython] C_element094  label="C_element : 052"  # scripted group (container) (typed FeaturePython)
  n = 2
  ref = C_element
FEATURE [App::DocumentObjectGroupPython] H_element086  label="H_element : 048"  # scripted group (container) (typed FeaturePython)
  n = 2
  ref = H_element
FEATURE [App::DocumentObjectGroupPython] F_element016  label="F_element : 007"  # scripted group (container) (typed FeaturePython)
  n = 2
  ref = F_element
FEATURE [App::DocumentObjectGroupPython] G4_POLYVINYLIDENE_FLUORIDE  # scripted group (container) (typed FeaturePython)
  Dunit = g/cm3
  Dvalue = 1.76
  Group = -> [C_element094,H_element086,F_element016]
  conduct = 2
  density = 1
  expand = 3
  formula = G4_POLYVINYLIDENE_FLUORIDE
  name = G4_POLYVINYLIDENE_FLUORIDE
  specific = 4
FEATURE [App::DocumentObjectGroupPython] C_element095  label="C_element : 053"  # scripted group (container) (typed FeaturePython)
  n = 6
  ref = C_element
FEATURE [App::DocumentObjectGroupPython] H_element087  label="H_element : 9"  # scripted group (container) (typed FeaturePython)
  n = 9
  ref = H_element
FEATURE [App::DocumentObjectGroupPython] N_element037  label="N_element : 016"  # scripted group (container) (typed FeaturePython)
  n = 1
  ref = N_element
FEATURE [App::DocumentObjectGroupPython] O_element084  label="O_element : 045"  # scripted group (container) (typed FeaturePython)
  n = 1
  ref = O_element
FEATURE [App::DocumentObjectGroupPython] G4_POLYVINYL_PYRROLIDONE  # scripted group (container) (typed FeaturePython)
  Dunit = g/cm3
  Dvalue = 1.25
  Group = -> [C_element095,H_element087,N_element037,O_element084]
  conduct = 2
  density = 1
  expand = 3
  formula = G4_POLYVINYL_PYRROLIDONE
  name = G4_POLYVINYL_PYRROLIDONE
  specific = 4
FEATURE [App::DocumentObjectGroupPython] K_element008  label="K_element : 1"  # scripted group (container) (typed FeaturePython)
  n = 1
  ref = K_element
FEATURE [App::DocumentObjectGroupPython] I_element006  label="I_element : 003"  # scripted group (container) (typed FeaturePython)
  n = 1
  ref = I_element
FEATURE [App::DocumentObjectGroupPython] G4_POTASSIUM_IODIDE  # scripted group (container) (typed FeaturePython)
  Dunit = g/cm3
  Dvalue = 3.13
  Group = -> [K_element008,I_element006]
  conduct = 2
  density = 1
  expand = 3
  formula = G4_POTASSIUM_IODIDE
  name = G4_POTASSIUM_IODIDE
  specific = 4
FEATURE [App::DocumentObjectGroupPython] K_element009  label="K_element : 2"  # scripted group (container) (typed FeaturePython)
  n = 2
  ref = K_element
FEATURE [App::DocumentObjectGroupPython] O_element085  label="O_element : 046"  # scripted group (container) (typed FeaturePython)
  n = 1
  ref = O_element
FEATURE [App::DocumentObjectGroupPython] G4_POTASSIUM_OXIDE  # scripted group (container) (typed FeaturePython)
  Dunit = g/cm3
  Dvalue = 2.32
  Group = -> [K_element009,O_element085]
  conduct = 2
  density = 1
  expand = 3
  formula = G4_POTASSIUM_OXIDE
  name = G4_POTASSIUM_OXIDE
  specific = 4
FEATURE [App::DocumentObjectGroupPython] C_element096  label="C_element : 054"  # scripted group (container) (typed FeaturePython)
  n = 3
  ref = C_element
FEATURE [App::DocumentObjectGroupPython] H_element088  label="H_element : 049"  # scripted group (container) (typed FeaturePython)
  n = 8
  ref = H_element
FEATURE [App::DocumentObjectGroupPython] G4_PROPANE  # scripted group (container) (typed FeaturePython)
  Dunit = g/cm3
  Dvalue = 0.00187939
  Group = -> [C_element096,H_element088]
  conduct = 2
  density = 1
  expand = 3
  formula = G4_PROPANE
  name = G4_PROPANE
  specific = 4
FEATURE [App::DocumentObjectGroupPython] C_element097  label="C_element : 055"  # scripted group (container) (typed FeaturePython)
  n = 3
  ref = C_element
FEATURE [App::DocumentObjectGroupPython] H_element089  label="H_element : 050"  # scripted group (container) (typed FeaturePython)
  n = 8
  ref = H_element
FEATURE [App::DocumentObjectGroupPython] G4_lPROPANE  # scripted group (container) (typed FeaturePython)
  Dunit = g/cm3
  Dvalue = 0.43
  Group = -> [C_element097,H_element089]
  conduct = 2
  density = 1
  expand = 3
  formula = G4_lPROPANE
  name = G4_lPROPANE
  specific = 4
FEATURE [App::DocumentObjectGroupPython] C_element098  label="C_element : 056"  # scripted group (container) (typed FeaturePython)
  n = 3
  ref = C_element
FEATURE [App::DocumentObjectGroupPython] H_element090  label="H_element : 051"  # scripted group (container) (typed FeaturePython)
  n = 8
  ref = H_element
FEATURE [App::DocumentObjectGroupPython] O_element086  label="O_element : 047"  # scripted group (container) (typed FeaturePython)
  n = 1
  ref = O_element
FEATURE [App::DocumentObjectGroupPython] G4_N_PROPYL_ALCOHOL  label="G4_N-PROPYL_ALCOHOL"  # scripted group (container) (typed FeaturePython)
  Dunit = g/cm3
  Dvalue = 0.8035
  Group = -> [C_element098,H_element090,O_element086]
  conduct = 2
  density = 1
  expand = 3
  formula = G4_N-PROPYL_ALCOHOL
  name = G4_N-PROPYL_ALCOHOL
  specific = 4
FEATURE [App::DocumentObjectGroupPython] C_element099  label="C_element : 057"  # scripted group (container) (typed FeaturePython)
  n = 5
  ref = C_element
FEATURE [App::DocumentObjectGroupPython] H_element091  label="H_element : 052"  # scripted group (container) (typed FeaturePython)
  n = 5
  ref = H_element
FEATURE [App::DocumentObjectGroupPython] N_element038  label="N_element : 017"  # scripted group (container) (typed FeaturePython)
  n = 1
  ref = N_element
FEATURE [App::DocumentObjectGroupPython] G4_PYRIDINE  # scripted group (container) (typed FeaturePython)
  Dunit = g/cm3
  Dvalue = 0.9819
  Group = -> [C_element099,H_element091,N_element038]
  conduct = 2
  density = 1
  expand = 3
  formula = G4_PYRIDINE
  name = G4_PYRIDINE
  specific = 4
FEATURE [App::DocumentObjectGroupPython] H_element092  label="H_element : 0.144"  # scripted group (container) (typed FeaturePython)
  n = 0.143711
FEATURE [App::DocumentObjectGroupPython] C_element100  label="C_element : 0.856"  # scripted group (container) (typed FeaturePython)
  n = 0.856289
FEATURE [App::DocumentObjectGroupPython] G4_RUBBER_BUTYL  # scripted group (container) (typed FeaturePython)
  Dunit = g/cm3
  Dvalue = 0.92
  Group = -> [H_element092,C_element100]
  conduct = 2
  density = 1
  expand = 3
  formula = G4_RUBBER_BUTYL
  name = G4_RUBBER_BUTYL
  specific = 4
FEATURE [App::DocumentObjectGroupPython] H_element093  label="H_element : 0.118"  # scripted group (container) (typed FeaturePython)
  n = 0.118371
FEATURE [App::DocumentObjectGroupPython] C_element101  label="C_element : 0.882"  # scripted group (container) (typed FeaturePython)
  n = 0.881629
FEATURE [App::DocumentObjectGroupPython] G4_RUBBER_NATURAL  # scripted group (container) (typed FeaturePython)
  Dunit = g/cm3
  Dvalue = 0.92
  Group = -> [H_element093,C_element101]
  conduct = 2
  density = 1
  expand = 3
  formula = G4_RUBBER_NATURAL
  name = G4_RUBBER_NATURAL
  specific = 4
FEATURE [App::DocumentObjectGroupPython] H_element094  label="H_element : 0.145"  # scripted group (container) (typed FeaturePython)
  n = 0.05692
FEATURE [App::DocumentObjectGroupPython] C_element102  label="C_element : 0.543"  # scripted group (container) (typed FeaturePython)
  n = 0.542646
FEATURE [App::DocumentObjectGroupPython] Cl_element021  label="Cl_element : 0.400"  # scripted group (container) (typed FeaturePython)
  n = 0.400434
FEATURE [App::DocumentObjectGroupPython] G4_RUBBER_NEOPRENE  # scripted group (container) (typed FeaturePython)
  Dunit = g/cm3
  Dvalue = 1.23
  Group = -> [H_element094,C_element102,Cl_element021]
  conduct = 2
  density = 1
  expand = 3
  formula = G4_RUBBER_NEOPRENE
  name = G4_RUBBER_NEOPRENE
  specific = 4
FEATURE [App::DocumentObjectGroupPython] Si_element006  label="Si_element : 1"  # scripted group (container) (typed FeaturePython)
  n = 1
  ref = Si_element
FEATURE [App::DocumentObjectGroupPython] O_element087  label="O_element : 048"  # scripted group (container) (typed FeaturePython)
  n = 2
  ref = O_element
FEATURE [App::DocumentObjectGroupPython] G4_SILICON_DIOXIDE  # scripted group (container) (typed FeaturePython)
  Dunit = g/cm3
  Dvalue = 2.32
  Group = -> [Si_element006,O_element087]
  conduct = 2
  density = 1
  expand = 3
  formula = G4_SILICON_DIOXIDE
  name = G4_SILICON_DIOXIDE
  specific = 4
FEATURE [App::DocumentObjectGroupPython] Ag_element002  label="Ag_element : 1"  # scripted group (container) (typed FeaturePython)
  n = 1
  ref = Ag_element
FEATURE [App::DocumentObjectGroupPython] Br_element005  label="Br_element : 003"  # scripted group (container) (typed FeaturePython)
  n = 1
  ref = Br_element
FEATURE [App::DocumentObjectGroupPython] G4_SILVER_BROMIDE  # scripted group (container) (typed FeaturePython)
  Dunit = g/cm3
  Dvalue = 6.473
  Group = -> [Ag_element002,Br_element005]
  conduct = 2
  density = 1
  expand = 3
  formula = G4_SILVER_BROMIDE
  name = G4_SILVER_BROMIDE
  specific = 4
FEATURE [App::DocumentObjectGroupPython] Ag_element003  label="Ag_element : 002"  # scripted group (container) (typed FeaturePython)
  n = 1
  ref = Ag_element
FEATURE [App::DocumentObjectGroupPython] Cl_element022  label="Cl_element : 011"  # scripted group (container) (typed FeaturePython)
  n = 1
  ref = Cl_element
FEATURE [App::DocumentObjectGroupPython] G4_SILVER_CHLORIDE  # scripted group (container) (typed FeaturePython)
  Dunit = g/cm3
  Dvalue = 5.56
  Group = -> [Ag_element003,Cl_element022]
  conduct = 2
  density = 1
  expand = 3
  formula = G4_SILVER_CHLORIDE
  name = G4_SILVER_CHLORIDE
  specific = 4
FEATURE [App::DocumentObjectGroupPython] Br_element006  label="Br_element : 0.423"  # scripted group (container) (typed FeaturePython)
  n = 0.422895
FEATURE [App::DocumentObjectGroupPython] Ag_element004  label="Ag_element : 0.574"  # scripted group (container) (typed FeaturePython)
  n = 0.573748
FEATURE [App::DocumentObjectGroupPython] I_element007  label="I_element : 0.649"  # scripted group (container) (typed FeaturePython)
  n = 0.003357
FEATURE [App::DocumentObjectGroupPython] G4_SILVER_HALIDES  # scripted group (container) (typed FeaturePython)
  Dunit = g/cm3
  Dvalue = 6.47
  Group = -> [Br_element006,Ag_element004,I_element007]
  conduct = 2
  density = 1
  expand = 3
  formula = G4_SILVER_HALIDES
  name = G4_SILVER_HALIDES
  specific = 4
FEATURE [App::DocumentObjectGroupPython] Ag_element005  label="Ag_element : 003"  # scripted group (container) (typed FeaturePython)
  n = 1
  ref = Ag_element
FEATURE [App::DocumentObjectGroupPython] I_element008  label="I_element : 004"  # scripted group (container) (typed FeaturePython)
  n = 1
  ref = I_element
FEATURE [App::DocumentObjectGroupPython] G4_SILVER_IODIDE  # scripted group (container) (typed FeaturePython)
  Dunit = g/cm3
  Dvalue = 6.01
  Group = -> [Ag_element005,I_element008]
  conduct = 2
  density = 1
  expand = 3
  formula = G4_SILVER_IODIDE
  name = G4_SILVER_IODIDE
  specific = 4
FEATURE [App::DocumentObjectGroupPython] H_element095  label="H_element : 0.100"  # scripted group (container) (typed FeaturePython)
  n = 0.1
FEATURE [App::DocumentObjectGroupPython] C_element103  label="C_element : 0.204"  # scripted group (container) (typed FeaturePython)
  n = 0.204
FEATURE [App::DocumentObjectGroupPython] N_element039  label="N_element : 0.759"  # scripted group (container) (typed FeaturePython)
  n = 0.042
FEATURE [App::DocumentObjectGroupPython] O_element088  label="O_element : 0.645"  # scripted group (container) (typed FeaturePython)
  n = 0.645
FEATURE [App::DocumentObjectGroupPython] Na_element013  label="Na_element : 0.100"  # scripted group (container) (typed FeaturePython)
  n = 0.002
FEATURE [App::DocumentObjectGroupPython] P_element009  label="P_element : 0.107"  # scripted group (container) (typed FeaturePython)
  n = 0.001
FEATURE [App::DocumentObjectGroupPython] S_element020  label="S_element : 0.021"  # scripted group (container) (typed FeaturePython)
  n = 0.002
FEATURE [App::DocumentObjectGroupPython] Cl_element023  label="Cl_element : 0.590"  # scripted group (container) (typed FeaturePython)
  n = 0.003
FEATURE [App::DocumentObjectGroupPython] K_element010  label="K_element : 0.001"  # scripted group (container) (typed FeaturePython)
  n = 0.001
FEATURE [App::DocumentObjectGroupPython] G4_SKIN_ICRP  # scripted group (container) (typed FeaturePython)
  Dunit = g/cm3
  Dvalue = 1.09
  Group = -> [H_element095,C_element103,N_element039,O_element088,Na_element013,P_element009,S_element020,Cl_element023,K_element010]
  conduct = 2
  density = 1
  expand = 3
  formula = G4_SKIN_ICRP
  name = G4_SKIN_ICRP
  specific = 4
FEATURE [App::DocumentObjectGroupPython] Na_element014  label="Na_element : 2"  # scripted group (container) (typed FeaturePython)
  n = 2
  ref = Na_element
FEATURE [App::DocumentObjectGroupPython] C_element104  label="C_element : 058"  # scripted group (container) (typed FeaturePython)
  n = 1
  ref = C_element
FEATURE [App::DocumentObjectGroupPython] O_element089  label="O_element : 049"  # scripted group (container) (typed FeaturePython)
  n = 3
  ref = O_element
FEATURE [App::DocumentObjectGroupPython] G4_SODIUM_CARBONATE  # scripted group (container) (typed FeaturePython)
  Dunit = g/cm3
  Dvalue = 2.532
  Group = -> [Na_element014,C_element104,O_element089]
  conduct = 2
  density = 1
  expand = 3
  formula = G4_SODIUM_CARBONATE
  name = G4_SODIUM_CARBONATE
  specific = 4
FEATURE [App::DocumentObjectGroupPython] Na_element015  label="Na_element : 1"  # scripted group (container) (typed FeaturePython)
  n = 1
  ref = Na_element
FEATURE [App::DocumentObjectGroupPython] I_element009  label="I_element : 005"  # scripted group (container) (typed FeaturePython)
  n = 1
  ref = I_element
FEATURE [App::DocumentObjectGroupPython] G4_SODIUM_IODIDE  # scripted group (container) (typed FeaturePython)
  Dunit = g/cm3
  Dvalue = 3.667
  Group = -> [Na_element015,I_element009]
  conduct = 2
  density = 1
  expand = 3
  formula = G4_SODIUM_IODIDE
  name = G4_SODIUM_IODIDE
  specific = 4
FEATURE [App::DocumentObjectGroupPython] Na_element016  label="Na_element : 003"  # scripted group (container) (typed FeaturePython)
  n = 2
  ref = Na_element
FEATURE [App::DocumentObjectGroupPython] O_element090  label="O_element : 050"  # scripted group (container) (typed FeaturePython)
  n = 1
  ref = O_element
FEATURE [App::DocumentObjectGroupPython] G4_SODIUM_MONOXIDE  # scripted group (container) (typed FeaturePython)
  Dunit = g/cm3
  Dvalue = 2.27
  Group = -> [Na_element016,O_element090]
  conduct = 2
  density = 1
  expand = 3
  formula = G4_SODIUM_MONOXIDE
  name = G4_SODIUM_MONOXIDE
  specific = 4
FEATURE [App::DocumentObjectGroupPython] Na_element017  label="Na_element : 004"  # scripted group (container) (typed FeaturePython)
  n = 1
  ref = Na_element
FEATURE [App::DocumentObjectGroupPython] N_element040  label="N_element : 018"  # scripted group (container) (typed FeaturePython)
  n = 1
  ref = N_element
FEATURE [App::DocumentObjectGroupPython] O_element091  label="O_element : 051"  # scripted group (container) (typed FeaturePython)
  n = 3
  ref = O_element
FEATURE [App::DocumentObjectGroupPython] G4_SODIUM_NITRATE  # scripted group (container) (typed FeaturePython)
  Dunit = g/cm3
  Dvalue = 2.261
  Group = -> [Na_element017,N_element040,O_element091]
  conduct = 2
  density = 1
  expand = 3
  formula = G4_SODIUM_NITRATE
  name = G4_SODIUM_NITRATE
  specific = 4
FEATURE [App::DocumentObjectGroupPython] C_element105  label="C_element : 059"  # scripted group (container) (typed FeaturePython)
  n = 14
  ref = C_element
FEATURE [App::DocumentObjectGroupPython] H_element096  label="H_element : 053"  # scripted group (container) (typed FeaturePython)
  n = 12
  ref = H_element
FEATURE [App::DocumentObjectGroupPython] G4_STILBENE  # scripted group (container) (typed FeaturePython)
  Dunit = g/cm3
  Dvalue = 0.9707
  Group = -> [C_element105,H_element096]
  conduct = 2
  density = 1
  expand = 3
  formula = G4_STILBENE
  name = G4_STILBENE
  specific = 4
FEATURE [App::DocumentObjectGroupPython] C_element106  label="C_element : 12"  # scripted group (container) (typed FeaturePython)
  n = 12
  ref = C_element
FEATURE [App::DocumentObjectGroupPython] H_element097  label="H_element : 22"  # scripted group (container) (typed FeaturePython)
  n = 22
  ref = H_element
FEATURE [App::DocumentObjectGroupPython] O_element092  label="O_element : 11"  # scripted group (container) (typed FeaturePython)
  n = 11
  ref = O_element
FEATURE [App::DocumentObjectGroupPython] G4_SUCROSE  # scripted group (container) (typed FeaturePython)
  Dunit = g/cm3
  Dvalue = 1.5805
  Group = -> [C_element106,H_element097,O_element092]
  conduct = 2
  density = 1
  expand = 3
  formula = G4_SUCROSE
  name = G4_SUCROSE
  specific = 4
FEATURE [App::DocumentObjectGroupPython] C_element107  label="C_element : 18"  # scripted group (container) (typed FeaturePython)
  n = 18
  ref = C_element
FEATURE [App::DocumentObjectGroupPython] H_element098  label="H_element : 054"  # scripted group (container) (typed FeaturePython)
  n = 14
  ref = H_element
FEATURE [App::DocumentObjectGroupPython] G4_TERPHENYL  # scripted group (container) (typed FeaturePython)
  Dunit = g/cm3
  Dvalue = 1.24
  Group = -> [C_element107,H_element098]
  conduct = 2
  density = 1
  expand = 3
  formula = G4_TERPHENYL
  name = G4_TERPHENYL
  specific = 4
FEATURE [App::DocumentObjectGroupPython] H_element099  label="H_element : 0.146"  # scripted group (container) (typed FeaturePython)
  n = 0.106
FEATURE [App::DocumentObjectGroupPython] C_element108  label="C_element : 0.883"  # scripted group (container) (typed FeaturePython)
  n = 0.099
FEATURE [App::DocumentObjectGroupPython] N_element041  label="N_element : 0.020"  # scripted group (container) (typed FeaturePython)
  n = 0.02
FEATURE [App::DocumentObjectGroupPython] O_element093  label="O_element : 0.766"  # scripted group (container) (typed FeaturePython)
  n = 0.766
FEATURE [App::DocumentObjectGroupPython] Na_element018  label="Na_element : 0.101"  # scripted group (container) (typed FeaturePython)
  n = 0.002
FEATURE [App::DocumentObjectGroupPython] P_element010  label="P_element : 0.108"  # scripted group (container) (typed FeaturePython)
  n = 0.001
FEATURE [App::DocumentObjectGroupPython] S_element021  label="S_element : 0.022"  # scripted group (container) (typed FeaturePython)
  n = 0.002
FEATURE [App::DocumentObjectGroupPython] Cl_element024  label="Cl_element : 0.002"  # scripted group (container) (typed FeaturePython)
  n = 0.002
FEATURE [App::DocumentObjectGroupPython] K_element011  label="K_element : 0.017"  # scripted group (container) (typed FeaturePython)
  n = 0.002
FEATURE [App::DocumentObjectGroupPython] G4_TESTIS_ICRP  # scripted group (container) (typed FeaturePython)
  Dunit = g/cm3
  Dvalue = 1.04
  Group = -> [H_element099,C_element108,N_element041,O_element093,Na_element018,P_element010,S_element021,Cl_element024,K_element011]
  conduct = 2
  density = 1
  expand = 3
  formula = G4_TESTIS_ICRP
  name = G4_TESTIS_ICRP
  specific = 4
FEATURE [App::DocumentObjectGroupPython] C_element109  label="C_element : 060"  # scripted group (container) (typed FeaturePython)
  n = 2
  ref = C_element
FEATURE [App::DocumentObjectGroupPython] Cl_element025  label="Cl_element : 012"  # scripted group (container) (typed FeaturePython)
  n = 4
  ref = Cl_element
FEATURE [App::DocumentObjectGroupPython] G4_TETRACHLOROETHYLENE  # scripted group (container) (typed FeaturePython)
  Dunit = g/cm3
  Dvalue = 1.625
  Group = -> [C_element109,Cl_element025]
  conduct = 2
  density = 1
  expand = 3
  formula = G4_TETRACHLOROETHYLENE
  name = G4_TETRACHLOROETHYLENE
  specific = 4
FEATURE [App::DocumentObjectGroupPython] Tl_element001  label="Tl_element : 1"  # scripted group (container) (typed FeaturePython)
  n = 1
  ref = Tl_element
FEATURE [App::DocumentObjectGroupPython] Cl_element026  label="Cl_element : 013"  # scripted group (container) (typed FeaturePython)
  n = 1
  ref = Cl_element
FEATURE [App::DocumentObjectGroupPython] G4_THALLIUM_CHLORIDE  # scripted group (container) (typed FeaturePython)
  Dunit = g/cm3
  Dvalue = 7.004
  Group = -> [Tl_element001,Cl_element026]
  conduct = 2
  density = 1
  expand = 3
  formula = G4_THALLIUM_CHLORIDE
  name = G4_THALLIUM_CHLORIDE
  specific = 4
FEATURE [App::DocumentObjectGroupPython] H_element100  label="H_element : 0.147"  # scripted group (container) (typed FeaturePython)
  n = 0.105
FEATURE [App::DocumentObjectGroupPython] C_element110  label="C_element : 0.256"  # scripted group (container) (typed FeaturePython)
  n = 0.256
FEATURE [App::DocumentObjectGroupPython] N_element042  label="N_element : 0.760"  # scripted group (container) (typed FeaturePython)
  n = 0.027
FEATURE [App::DocumentObjectGroupPython] O_element094  label="O_element : 0.602"  # scripted group (container) (typed FeaturePython)
  n = 0.602
FEATURE [App::DocumentObjectGroupPython] Na_element019  label="Na_element : 0.102"  # scripted group (container) (typed FeaturePython)
  n = 0.001
FEATURE [App::DocumentObjectGroupPython] P_element011  label="P_element : 0.109"  # scripted group (container) (typed FeaturePython)
  n = 0.002
FEATURE [App::DocumentObjectGroupPython] S_element022  label="S_element : 0.023"  # scripted group (container) (typed FeaturePython)
  n = 0.003
FEATURE [App::DocumentObjectGroupPython] Cl_element027  label="Cl_element : 0.591"  # scripted group (container) (typed FeaturePython)
  n = 0.002
FEATURE [App::DocumentObjectGroupPython] K_element012  label="K_element : 0.018"  # scripted group (container) (typed FeaturePython)
  n = 0.002
FEATURE [App::DocumentObjectGroupPython] G4_TISSUE_SOFT_ICRP  # scripted group (container) (typed FeaturePython)
  Dunit = g/cm3
  Dvalue = 1.03
  Group = -> [H_element100,C_element110,N_element042,O_element094,Na_element019,P_element011,S_element022,Cl_element027,K_element012]
  conduct = 2
  density = 1
  expand = 3
  formula = G4_TISSUE_SOFT_ICRP
  name = G4_TISSUE_SOFT_ICRP
  specific = 4
FEATURE [App::DocumentObjectGroupPython] H_element101  label="H_element : 0.148"  # scripted group (container) (typed FeaturePython)
  n = 0.101
FEATURE [App::DocumentObjectGroupPython] C_element111  label="C_element : 0.111"  # scripted group (container) (typed FeaturePython)
  n = 0.111
FEATURE [App::DocumentObjectGroupPython] N_element043  label="N_element : 0.026"  # scripted group (container) (typed FeaturePython)
  n = 0.026
FEATURE [App::DocumentObjectGroupPython] O_element095  label="O_element : 0.762"  # scripted group (container) (typed FeaturePython)
  n = 0.762
FEATURE [App::DocumentObjectGroupPython] G4_TISSUE_SOFT_ICRU_4  label="G4_TISSUE_SOFT_ICRU-4"  # scripted group (container) (typed FeaturePython)
  Dunit = g/cm3
  Dvalue = 1
  Group = -> [H_element101,C_element111,N_element043,O_element095]
  conduct = 2
  density = 1
  expand = 3
  formula = G4_TISSUE_SOFT_ICRU-4
  name = G4_TISSUE_SOFT_ICRU-4
  specific = 4
FEATURE [App::DocumentObjectGroupPython] H_element102  label="H_element : 0.149"  # scripted group (container) (typed FeaturePython)
  n = 0.101869
FEATURE [App::DocumentObjectGroupPython] C_element112  label="C_element : 0.456"  # scripted group (container) (typed FeaturePython)
  n = 0.456179
FEATURE [App::DocumentObjectGroupPython] N_element044  label="N_element : 0.761"  # scripted group (container) (typed FeaturePython)
  n = 0.035172
FEATURE [App::DocumentObjectGroupPython] O_element096  label="O_element : 0.407"  # scripted group (container) (typed FeaturePython)
  n = 0.40678
FEATURE [App::DocumentObjectGroupPython] G4_TISSUE_METHANE  label="G4_TISSUE-METHANE"  # scripted group (container) (typed FeaturePython)
  Dunit = g/cm3
  Dvalue = 0.00106409
  Group = -> [H_element102,C_element112,N_element044,O_element096]
  conduct = 2
  density = 1
  expand = 3
  formula = G4_TISSUE-METHANE
  name = G4_TISSUE-METHANE
  specific = 4
FEATURE [App::DocumentObjectGroupPython] H_element103  label="H_element : 0.103"  # scripted group (container) (typed FeaturePython)
  n = 0.102672
FEATURE [App::DocumentObjectGroupPython] C_element113  label="C_element : 0.569"  # scripted group (container) (typed FeaturePython)
  n = 0.56894
FEATURE [App::DocumentObjectGroupPython] N_element045  label="N_element : 0.762"  # scripted group (container) (typed FeaturePython)
  n = 0.035022
FEATURE [App::DocumentObjectGroupPython] O_element097  label="O_element : 0.293"  # scripted group (container) (typed FeaturePython)
  n = 0.293366
FEATURE [App::DocumentObjectGroupPython] G4_TISSUE_PROPANE  label="G4_TISSUE-PROPANE"  # scripted group (container) (typed FeaturePython)
  Dunit = g/cm3
  Dvalue = 0.00182628
  Group = -> [H_element103,C_element113,N_element045,O_element097]
  conduct = 2
  density = 1
  expand = 3
  formula = G4_TISSUE-PROPANE
  name = G4_TISSUE-PROPANE
  specific = 4
FEATURE [App::DocumentObjectGroupPython] Ti_element003  label="Ti_element : 1"  # scripted group (container) (typed FeaturePython)
  n = 1
  ref = Ti_element
FEATURE [App::DocumentObjectGroupPython] O_element098  label="O_element : 052"  # scripted group (container) (typed FeaturePython)
  n = 2
  ref = O_element
FEATURE [App::DocumentObjectGroupPython] G4_TITANIUM_DIOXIDE  # scripted group (container) (typed FeaturePython)
  Dunit = g/cm3
  Dvalue = 4.26
  Group = -> [Ti_element003,O_element098]
  conduct = 2
  density = 1
  expand = 3
  formula = G4_TITANIUM_DIOXIDE
  name = G4_TITANIUM_DIOXIDE
  specific = 4
FEATURE [App::DocumentObjectGroupPython] C_element114  label="C_element : 061"  # scripted group (container) (typed FeaturePython)
  n = 7
  ref = C_element
FEATURE [App::DocumentObjectGroupPython] H_element104  label="H_element : 055"  # scripted group (container) (typed FeaturePython)
  n = 8
  ref = H_element
FEATURE [App::DocumentObjectGroupPython] G4_TOLUENE  # scripted group (container) (typed FeaturePython)
  Dunit = g/cm3
  Dvalue = 0.8669
  Group = -> [C_element114,H_element104]
  conduct = 2
  density = 1
  expand = 3
  formula = G4_TOLUENE
  name = G4_TOLUENE
  specific = 4
FEATURE [App::DocumentObjectGroupPython] C_element115  label="C_element : 062"  # scripted group (container) (typed FeaturePython)
  n = 2
  ref = C_element
FEATURE [App::DocumentObjectGroupPython] H_element105  label="H_element : 056"  # scripted group (container) (typed FeaturePython)
  n = 1
  ref = H_element
FEATURE [App::DocumentObjectGroupPython] Cl_element028  label="Cl_element : 014"  # scripted group (container) (typed FeaturePython)
  n = 3
  ref = Cl_element
FEATURE [App::DocumentObjectGroupPython] G4_TRICHLOROETHYLENE  # scripted group (container) (typed FeaturePython)
  Dunit = g/cm3
  Dvalue = 1.46
  Group = -> [C_element115,H_element105,Cl_element028]
  conduct = 2
  density = 1
  expand = 3
  formula = G4_TRICHLOROETHYLENE
  name = G4_TRICHLOROETHYLENE
  specific = 4
FEATURE [App::DocumentObjectGroupPython] C_element116  label="C_element : 063"  # scripted group (container) (typed FeaturePython)
  n = 6
  ref = C_element
FEATURE [App::DocumentObjectGroupPython] H_element106  label="H_element : 15"  # scripted group (container) (typed FeaturePython)
  n = 15
  ref = H_element
FEATURE [App::DocumentObjectGroupPython] O_element099  label="O_element : 053"  # scripted group (container) (typed FeaturePython)
  n = 4
  ref = O_element
FEATURE [App::DocumentObjectGroupPython] P_element012  label="P_element : 1"  # scripted group (container) (typed FeaturePython)
  n = 1
  ref = P_element
FEATURE [App::DocumentObjectGroupPython] G4_TRIETHYL_PHOSPHATE  # scripted group (container) (typed FeaturePython)
  Dunit = g/cm3
  Dvalue = 1.07
  Group = -> [C_element116,H_element106,O_element099,P_element012]
  conduct = 2
  density = 1
  expand = 3
  formula = G4_TRIETHYL_PHOSPHATE
  name = G4_TRIETHYL_PHOSPHATE
  specific = 4
FEATURE [App::DocumentObjectGroupPython] W_element003  label="W_element : 003"  # scripted group (container) (typed FeaturePython)
  n = 1
  ref = W_element
FEATURE [App::DocumentObjectGroupPython] F_element017  label="F_element : 6"  # scripted group (container) (typed FeaturePython)
  n = 6
  ref = F_element
FEATURE [App::DocumentObjectGroupPython] G4_TUNGSTEN_HEXAFLUORIDE  # scripted group (container) (typed FeaturePython)
  Dunit = g/cm3
  Dvalue = 2.4
  Group = -> [W_element003,F_element017]
  conduct = 2
  density = 1
  expand = 3
  formula = G4_TUNGSTEN_HEXAFLUORIDE
  name = G4_TUNGSTEN_HEXAFLUORIDE
  specific = 4
FEATURE [App::DocumentObjectGroupPython] U_element001  label="U_element : 1"  # scripted group (container) (typed FeaturePython)
  n = 1
  ref = U_element
FEATURE [App::DocumentObjectGroupPython] C_element117  label="C_element : 064"  # scripted group (container) (typed FeaturePython)
  n = 2
  ref = C_element
FEATURE [App::DocumentObjectGroupPython] G4_URANIUM_DICARBIDE  # scripted group (container) (typed FeaturePython)
  Dunit = g/cm3
  Dvalue = 11.28
  Group = -> [U_element001,C_element117]
  conduct = 2
  density = 1
  expand = 3
  formula = G4_URANIUM_DICARBIDE
  name = G4_URANIUM_DICARBIDE
  specific = 4
FEATURE [App::DocumentObjectGroupPython] U_element002  label="U_element : 002"  # scripted group (container) (typed FeaturePython)
  n = 1
  ref = U_element
FEATURE [App::DocumentObjectGroupPython] C_element118  label="C_element : 065"  # scripted group (container) (typed FeaturePython)
  n = 1
  ref = C_element
FEATURE [App::DocumentObjectGroupPython] G4_URANIUM_MONOCARBIDE  # scripted group (container) (typed FeaturePython)
  Dunit = g/cm3
  Dvalue = 13.63
  Group = -> [U_element002,C_element118]
  conduct = 2
  density = 1
  expand = 3
  formula = G4_URANIUM_MONOCARBIDE
  name = G4_URANIUM_MONOCARBIDE
  specific = 4
FEATURE [App::DocumentObjectGroupPython] U_element003  label="U_element : 003"  # scripted group (container) (typed FeaturePython)
  n = 1
  ref = U_element
FEATURE [App::DocumentObjectGroupPython] O_element100  label="O_element : 054"  # scripted group (container) (typed FeaturePython)
  n = 2
  ref = O_element
FEATURE [App::DocumentObjectGroupPython] G4_URANIUM_OXIDE  # scripted group (container) (typed FeaturePython)
  Dunit = g/cm3
  Dvalue = 10.96
  Group = -> [U_element003,O_element100]
  conduct = 2
  density = 1
  expand = 3
  formula = G4_URANIUM_OXIDE
  name = G4_URANIUM_OXIDE
  specific = 4
FEATURE [App::DocumentObjectGroupPython] C_element119  label="C_element : 066"  # scripted group (container) (typed FeaturePython)
  n = 1
  ref = C_element
FEATURE [App::DocumentObjectGroupPython] H_element107  label="H_element : 057"  # scripted group (container) (typed FeaturePython)
  n = 4
  ref = H_element
FEATURE [App::DocumentObjectGroupPython] N_element046  label="N_element : 019"  # scripted group (container) (typed FeaturePython)
  n = 2
  ref = N_element
FEATURE [App::DocumentObjectGroupPython] O_element101  label="O_element : 055"  # scripted group (container) (typed FeaturePython)
  n = 1
  ref = O_element
FEATURE [App::DocumentObjectGroupPython] G4_UREA  # scripted group (container) (typed FeaturePython)
  Dunit = g/cm3
  Dvalue = 1.323
  Group = -> [C_element119,H_element107,N_element046,O_element101]
  conduct = 2
  density = 1
  expand = 3
  formula = G4_UREA
  name = G4_UREA
  specific = 4
FEATURE [App::DocumentObjectGroupPython] C_element120  label="C_element : 067"  # scripted group (container) (typed FeaturePython)
  n = 5
  ref = C_element
FEATURE [App::DocumentObjectGroupPython] H_element108  label="H_element : 058"  # scripted group (container) (typed FeaturePython)
  n = 11
  ref = H_element
FEATURE [App::DocumentObjectGroupPython] N_element047  label="N_element : 020"  # scripted group (container) (typed FeaturePython)
  n = 1
  ref = N_element
FEATURE [App::DocumentObjectGroupPython] O_element102  label="O_element : 056"  # scripted group (container) (typed FeaturePython)
  n = 2
  ref = O_element
FEATURE [App::DocumentObjectGroupPython] G4_VALINE  # scripted group (container) (typed FeaturePython)
  Dunit = g/cm3
  Dvalue = 1.23
  Group = -> [C_element120,H_element108,N_element047,O_element102]
  conduct = 2
  density = 1
  expand = 3
  formula = G4_VALINE
  name = G4_VALINE
  specific = 4
FEATURE [App::DocumentObjectGroupPython] H_element109  label="H_element : 0.009"  # scripted group (container) (typed FeaturePython)
  n = 0.009417
FEATURE [App::DocumentObjectGroupPython] C_element121  label="C_element : 0.281"  # scripted group (container) (typed FeaturePython)
  n = 0.280555
FEATURE [App::DocumentObjectGroupPython] F_element018  label="F_element : 0.710"  # scripted group (container) (typed FeaturePython)
  n = 0.710028
FEATURE [App::DocumentObjectGroupPython] G4_VITON  # scripted group (container) (typed FeaturePython)
  Dunit = g/cm3
  Dvalue = 1.8
  Group = -> [H_element109,C_element121,F_element018]
  conduct = 2
  density = 1
  expand = 3
  formula = G4_VITON
  name = G4_VITON
  specific = 4
FEATURE [App::DocumentObjectGroupPython] H_element110  label="H_element : 059"  # scripted group (container) (typed FeaturePython)
  n = 2
  ref = H_element
FEATURE [App::DocumentObjectGroupPython] O_element103  label="O_element : 057"  # scripted group (container) (typed FeaturePython)
  n = 1
  ref = O_element
FEATURE [App::DocumentObjectGroupPython] G4_WATER  # scripted group (container) (typed FeaturePython)
  Dunit = g/cm3
  Dvalue = 1
  Group = -> [H_element110,O_element103]
  conduct = 2
  density = 1
  expand = 3
  formula = G4_WATER
  name = G4_WATER
  specific = 4
FEATURE [App::DocumentObjectGroupPython] H_element111  label="H_element : 060"  # scripted group (container) (typed FeaturePython)
  n = 2
  ref = H_element
FEATURE [App::DocumentObjectGroupPython] O_element104  label="O_element : 058"  # scripted group (container) (typed FeaturePython)
  n = 1
  ref = O_element
FEATURE [App::DocumentObjectGroupPython] G4_WATER_VAPOR  # scripted group (container) (typed FeaturePython)
  Dunit = g/cm3
  Dvalue = 0.000756182
  Group = -> [H_element111,O_element104]
  conduct = 2
  density = 1
  expand = 3
  formula = G4_WATER_VAPOR
  name = G4_WATER_VAPOR
  specific = 4
FEATURE [App::DocumentObjectGroupPython] C_element122  label="C_element : 068"  # scripted group (container) (typed FeaturePython)
  n = 8
  ref = C_element
FEATURE [App::DocumentObjectGroupPython] H_element112  label="H_element : 061"  # scripted group (container) (typed FeaturePython)
  n = 10
  ref = H_element
FEATURE [App::DocumentObjectGroupPython] G4_XYLENE  # scripted group (container) (typed FeaturePython)
  Dunit = g/cm3
  Dvalue = 0.87
  Group = -> [C_element122,H_element112]
  conduct = 2
  density = 1
  expand = 3
  formula = G4_XYLENE
  name = G4_XYLENE
  specific = 4
FEATURE [App::DocumentObjectGroupPython] C_element123  label="C_element : 069"  # scripted group (container) (typed FeaturePython)
  n = 1
  ref = C_element
FEATURE [App::DocumentObjectGroupPython] G4_GRAPHITE  # scripted group (container) (typed FeaturePython)
  Dunit = g/cm3
  Dvalue = 2.21
  Group = -> [C_element123]
  conduct = 2
  density = 1
  expand = 3
  formula = G4_GRAPHITE
  name = G4_GRAPHITE
  specific = 4
FEATURE [App::DocumentObjectGroupPython] NIST  # scripted group (container) (typed FeaturePython)
  Group = -> [G4_A_150_TISSUE,G4_ACETONE,G4_ACETYLENE,G4_ADENINE,G4_ADIPOSE_TISSUE_ICRP,G4_AIR,G4_ALANINE,G4_ALUMINUM_OXIDE,G4_AMBER,G4_AMMONIA,G4_ANILINE,G4_ANTHRACENE,G4_B_100_BONE,G4_BAKELITE,G4_BARIUM_FLUORIDE,G4_BARIUM_SULFATE,G4_BENZENE,G4_BERYLLIUM_OXIDE,G4_BGO,G4_BLOOD_ICRP,G4_BONE_COMPACT_ICRU,G4_BONE_CORTICAL_ICRP,G4_BORON_CARBIDE,G4_BORON_OXIDE,G4_BRAIN_ICRP,G4_BUTANE,G4_N_BUTYL_ALCOHOL,G4_C_552,+152 more]
FEATURE [App::DocumentObjectGroupPython] H_element113  label="H_element : 062"  # scripted group (container) (typed FeaturePython)
  n = 1
  ref = H_element
FEATURE [App::DocumentObjectGroupPython] G4_H  # scripted group (container) (typed FeaturePython)
  Dunit = g/cm3
  Dvalue = 8.3748e-05
  Group = -> [H_element113]
  conduct = 2
  density = 1
  expand = 3
  formula = H
  name = G4_H
  specific = 4
FEATURE [App::DocumentObjectGroupPython] He_element001  label="He_element : 1"  # scripted group (container) (typed FeaturePython)
  n = 1
  ref = He_element
FEATURE [App::DocumentObjectGroupPython] G4_He  # scripted group (container) (typed FeaturePython)
  Dunit = g/cm3
  Dvalue = 0.000166322
  Group = -> [He_element001]
  conduct = 2
  density = 1
  expand = 3
  formula = He
  name = G4_He
  specific = 4
FEATURE [App::DocumentObjectGroupPython] Li_element008  label="Li_element : 008"  # scripted group (container) (typed FeaturePython)
  n = 1
  ref = Li_element
FEATURE [App::DocumentObjectGroupPython] G4_Li  # scripted group (container) (typed FeaturePython)
  Dunit = g/cm3
  Dvalue = 0.534
  Group = -> [Li_element008]
  conduct = 2
  density = 1
  expand = 3
  formula = Li
  name = G4_Li
  specific = 4
FEATURE [App::DocumentObjectGroupPython] Be_element002  label="Be_element : 002"  # scripted group (container) (typed FeaturePython)
  n = 1
  ref = Be_element
FEATURE [App::DocumentObjectGroupPython] G4_Be  # scripted group (container) (typed FeaturePython)
  Dunit = g/cm3
  Dvalue = 1.848
  Group = -> [Be_element002]
  conduct = 2
  density = 1
  expand = 3
  formula = Be
  name = G4_Be
  specific = 4
FEATURE [App::DocumentObjectGroupPython] B_element007  label="B_element : 007"  # scripted group (container) (typed FeaturePython)
  n = 1
  ref = B_element
FEATURE [App::DocumentObjectGroupPython] G4_B  # scripted group (container) (typed FeaturePython)
  Dunit = g/cm3
  Dvalue = 2.37
  Group = -> [B_element007]
  conduct = 2
  density = 1
  expand = 3
  formula = B
  name = G4_B
  specific = 4
FEATURE [App::DocumentObjectGroupPython] C_element124  label="C_element : 070"  # scripted group (container) (typed FeaturePython)
  n = 1
  ref = C_element
FEATURE [App::DocumentObjectGroupPython] G4_C  # scripted group (container) (typed FeaturePython)
  Dunit = g/cm3
  Dvalue = 2
  Group = -> [C_element124]
  conduct = 2
  density = 1
  expand = 3
  formula = C
  name = G4_C
  specific = 4
FEATURE [App::DocumentObjectGroupPython] N_element048  label="N_element : 021"  # scripted group (container) (typed FeaturePython)
  n = 1
  ref = N_element
FEATURE [App::DocumentObjectGroupPython] G4_N  # scripted group (container) (typed FeaturePython)
  Dunit = g/cm3
  Dvalue = 0.0011652
  Group = -> [N_element048]
  conduct = 2
  density = 1
  expand = 3
  formula = N
  name = G4_N
  specific = 4
FEATURE [App::DocumentObjectGroupPython] O_element105  label="O_element : 059"  # scripted group (container) (typed FeaturePython)
  n = 1
  ref = O_element
FEATURE [App::DocumentObjectGroupPython] G4_O  # scripted group (container) (typed FeaturePython)
  Dunit = g/cm3
  Dvalue = 0.00133151
  Group = -> [O_element105]
  conduct = 2
  density = 1
  expand = 3
  formula = O
  name = G4_O
  specific = 4
FEATURE [App::DocumentObjectGroupPython] F_element019  label="F_element : 008"  # scripted group (container) (typed FeaturePython)
  n = 1
  ref = F_element
FEATURE [App::DocumentObjectGroupPython] G4_F  # scripted group (container) (typed FeaturePython)
  Dunit = g/cm3
  Dvalue = 0.00158029
  Group = -> [F_element019]
  conduct = 2
  density = 1
  expand = 3
  formula = F
  name = G4_F
  specific = 4
FEATURE [App::DocumentObjectGroupPython] Ne_element001  label="Ne_element : 1"  # scripted group (container) (typed FeaturePython)
  n = 1
  ref = Ne_element
FEATURE [App::DocumentObjectGroupPython] G4_Ne  # scripted group (container) (typed FeaturePython)
  Dunit = g/cm3
  Dvalue = 0.000838505
  Group = -> [Ne_element001]
  conduct = 2
  density = 1
  expand = 3
  formula = Ne
  name = G4_Ne
  specific = 4
FEATURE [App::DocumentObjectGroupPython] Na_element020  label="Na_element : 005"  # scripted group (container) (typed FeaturePython)
  n = 1
  ref = Na_element
FEATURE [App::DocumentObjectGroupPython] G4_Na  # scripted group (container) (typed FeaturePython)
  Dunit = g/cm3
  Dvalue = 0.971
  Group = -> [Na_element020]
  conduct = 2
  density = 1
  expand = 3
  formula = Na
  name = G4_Na
  specific = 4
FEATURE [App::DocumentObjectGroupPython] Mg_element011  label="Mg_element : 005"  # scripted group (container) (typed FeaturePython)
  n = 1
  ref = Mg_element
FEATURE [App::DocumentObjectGroupPython] G4_Mg  # scripted group (container) (typed FeaturePython)
  Dunit = g/cm3
  Dvalue = 1.74
  Group = -> [Mg_element011]
  conduct = 2
  density = 1
  expand = 3
  formula = Mg
  name = G4_Mg
  specific = 4
FEATURE [App::DocumentObjectGroupPython] Al_element004  label="Al_element : 1"  # scripted group (container) (typed FeaturePython)
  n = 1
  ref = Al_element
FEATURE [App::DocumentObjectGroupPython] G4_Al  # scripted group (container) (typed FeaturePython)
  Dunit = g/cm3
  Dvalue = 2.699
  Group = -> [Al_element004]
  conduct = 2
  density = 1
  expand = 3
  formula = Al
  name = G4_Al
  specific = 4
FEATURE [App::DocumentObjectGroupPython] Si_element007  label="Si_element : 002"  # scripted group (container) (typed FeaturePython)
  n = 1
  ref = Si_element
FEATURE [App::DocumentObjectGroupPython] G4_Si  # scripted group (container) (typed FeaturePython)
  Dunit = g/cm3
  Dvalue = 2.33
  Group = -> [Si_element007]
  conduct = 2
  density = 1
  expand = 3
  formula = Si
  name = G4_Si
  specific = 4
FEATURE [App::DocumentObjectGroupPython] P_element013  label="P_element : 002"  # scripted group (container) (typed FeaturePython)
  n = 1
  ref = P_element
FEATURE [App::DocumentObjectGroupPython] G4_P  # scripted group (container) (typed FeaturePython)
  Dunit = g/cm3
  Dvalue = 2.2
  Group = -> [P_element013]
  conduct = 2
  density = 1
  expand = 3
  formula = P
  name = G4_P
  specific = 4
FEATURE [App::DocumentObjectGroupPython] S_element023  label="S_element : 007"  # scripted group (container) (typed FeaturePython)
  n = 1
  ref = S_element
FEATURE [App::DocumentObjectGroupPython] G4_S  # scripted group (container) (typed FeaturePython)
  Dunit = g/cm3
  Dvalue = 2
  Group = -> [S_element023]
  conduct = 2
  density = 1
  expand = 3
  formula = S
  name = G4_S
  specific = 4
FEATURE [App::DocumentObjectGroupPython] Cl_element029  label="Cl_element : 015"  # scripted group (container) (typed FeaturePython)
  n = 1
  ref = Cl_element
FEATURE [App::DocumentObjectGroupPython] G4_Cl  # scripted group (container) (typed FeaturePython)
  Dunit = g/cm3
  Dvalue = 0.00299473
  Group = -> [Cl_element029]
  conduct = 2
  density = 1
  expand = 3
  formula = Cl
  name = G4_Cl
  specific = 4
FEATURE [App::DocumentObjectGroupPython] Ar_element002  label="Ar_element : 1"  # scripted group (container) (typed FeaturePython)
  n = 1
  ref = Ar_element
FEATURE [App::DocumentObjectGroupPython] G4_Ar  # scripted group (container) (typed FeaturePython)
  Dunit = g/cm3
  Dvalue = 0.00166201
  Group = -> [Ar_element002]
  conduct = 2
  density = 1
  expand = 3
  formula = Ar
  name = G4_Ar
  specific = 4
FEATURE [App::DocumentObjectGroupPython] K_element013  label="K_element : 003"  # scripted group (container) (typed FeaturePython)
  n = 1
  ref = K_element
FEATURE [App::DocumentObjectGroupPython] G4_K  # scripted group (container) (typed FeaturePython)
  Dunit = g/cm3
  Dvalue = 0.862
  Group = -> [K_element013]
  conduct = 2
  density = 1
  expand = 3
  formula = K
  name = G4_K
  specific = 4
FEATURE [App::DocumentObjectGroupPython] Ca_element014  label="Ca_element : 007"  # scripted group (container) (typed FeaturePython)
  n = 1
  ref = Ca_element
FEATURE [App::DocumentObjectGroupPython] G4_Ca  # scripted group (container) (typed FeaturePython)
  Dunit = g/cm3
  Dvalue = 1.55
  Group = -> [Ca_element014]
  conduct = 2
  density = 1
  expand = 3
  formula = Ca
  name = G4_Ca
  specific = 4
FEATURE [App::DocumentObjectGroupPython] Sc_element001  label="Sc_element : 1"  # scripted group (container) (typed FeaturePython)
  n = 1
  ref = Sc_element
FEATURE [App::DocumentObjectGroupPython] G4_Sc  # scripted group (container) (typed FeaturePython)
  Dunit = g/cm3
  Dvalue = 2.989
  Group = -> [Sc_element001]
  conduct = 2
  density = 1
  expand = 3
  formula = Sc
  name = G4_Sc
  specific = 4
FEATURE [App::DocumentObjectGroupPython] Ti_element004  label="Ti_element : 002"  # scripted group (container) (typed FeaturePython)
  n = 1
  ref = Ti_element
FEATURE [App::DocumentObjectGroupPython] G4_Ti  # scripted group (container) (typed FeaturePython)
  Dunit = g/cm3
  Dvalue = 4.54
  Group = -> [Ti_element004]
  conduct = 2
  density = 1
  expand = 3
  formula = Ti
  name = G4_Ti
  specific = 4
FEATURE [App::DocumentObjectGroupPython] V_element001  label="V_element : 1"  # scripted group (container) (typed FeaturePython)
  n = 1
  ref = V_element
FEATURE [App::DocumentObjectGroupPython] G4_V  # scripted group (container) (typed FeaturePython)
  Dunit = g/cm3
  Dvalue = 6.11
  Group = -> [V_element001]
  conduct = 2
  density = 1
  expand = 3
  formula = V
  name = G4_V
  specific = 4
FEATURE [App::DocumentObjectGroupPython] Cr_element001  label="Cr_element : 1"  # scripted group (container) (typed FeaturePython)
  n = 1
  ref = Cr_element
FEATURE [App::DocumentObjectGroupPython] G4_Cr  # scripted group (container) (typed FeaturePython)
  Dunit = g/cm3
  Dvalue = 7.18
  Group = -> [Cr_element001]
  conduct = 2
  density = 1
  expand = 3
  formula = Cr
  name = G4_Cr
  specific = 4
FEATURE [App::DocumentObjectGroupPython] Mn_element001  label="Mn_element : 1"  # scripted group (container) (typed FeaturePython)
  n = 1
  ref = Mn_element
FEATURE [App::DocumentObjectGroupPython] G4_Mn  # scripted group (container) (typed FeaturePython)
  Dunit = g/cm3
  Dvalue = 7.44
  Group = -> [Mn_element001]
  conduct = 2
  density = 1
  expand = 3
  formula = Mn
  name = G4_Mn
  specific = 4
FEATURE [App::DocumentObjectGroupPython] Fe_element007  label="Fe_element : 004"  # scripted group (container) (typed FeaturePython)
  n = 1
  ref = Fe_element
FEATURE [App::DocumentObjectGroupPython] G4_Fe  # scripted group (container) (typed FeaturePython)
  Dunit = g/cm3
  Dvalue = 7.874
  Group = -> [Fe_element007]
  conduct = 2
  density = 1
  expand = 3
  formula = Fe
  name = G4_Fe
  specific = 4
FEATURE [App::DocumentObjectGroupPython] Co_element001  label="Co_element : 1"  # scripted group (container) (typed FeaturePython)
  n = 1
  ref = Co_element
FEATURE [App::DocumentObjectGroupPython] G4_Co  # scripted group (container) (typed FeaturePython)
  Dunit = g/cm3
  Dvalue = 8.9
  Group = -> [Co_element001]
  conduct = 2
  density = 1
  expand = 3
  formula = Co
  name = G4_Co
  specific = 4
FEATURE [App::DocumentObjectGroupPython] Ni_element001  label="Ni_element : 1"  # scripted group (container) (typed FeaturePython)
  n = 1
  ref = Ni_element
FEATURE [App::DocumentObjectGroupPython] G4_Ni  # scripted group (container) (typed FeaturePython)
  Dunit = g/cm3
  Dvalue = 8.902
  Group = -> [Ni_element001]
  conduct = 2
  density = 1
  expand = 3
  formula = Ni
  name = G4_Ni
  specific = 4
FEATURE [App::DocumentObjectGroupPython] Cu_element001  label="Cu_element : 1"  # scripted group (container) (typed FeaturePython)
  n = 1
  ref = Cu_element
FEATURE [App::DocumentObjectGroupPython] G4_Cu  # scripted group (container) (typed FeaturePython)
  Dunit = g/cm3
  Dvalue = 8.96
  Group = -> [Cu_element001]
  conduct = 2
  density = 1
  expand = 3
  formula = Cu
  name = G4_Cu
  specific = 4
FEATURE [App::DocumentObjectGroupPython] Zn_element001  label="Zn_element : 1"  # scripted group (container) (typed FeaturePython)
  n = 1
  ref = Zn_element
FEATURE [App::DocumentObjectGroupPython] G4_Zn  # scripted group (container) (typed FeaturePython)
  Dunit = g/cm3
  Dvalue = 7.133
  Group = -> [Zn_element001]
  conduct = 2
  density = 1
  expand = 3
  formula = Zn
  name = G4_Zn
  specific = 4
FEATURE [App::DocumentObjectGroupPython] Ga_element002  label="Ga_element : 002"  # scripted group (container) (typed FeaturePython)
  n = 1
  ref = Ga_element
FEATURE [App::DocumentObjectGroupPython] G4_Ga  # scripted group (container) (typed FeaturePython)
  Dunit = g/cm3
  Dvalue = 5.904
  Group = -> [Ga_element002]
  conduct = 2
  density = 1
  expand = 3
  formula = Ga
  name = G4_Ga
  specific = 4
FEATURE [App::DocumentObjectGroupPython] Ge_element002  label="Ge_element : 1"  # scripted group (container) (typed FeaturePython)
  n = 1
  ref = Ge_element
FEATURE [App::DocumentObjectGroupPython] G4_Ge  # scripted group (container) (typed FeaturePython)
  Dunit = g/cm3
  Dvalue = 5.323
  Group = -> [Ge_element002]
  conduct = 2
  density = 1
  expand = 3
  formula = Ge
  name = G4_Ge
  specific = 4
FEATURE [App::DocumentObjectGroupPython] As_element003  label="As_element : 002"  # scripted group (container) (typed FeaturePython)
  n = 1
  ref = As_element
FEATURE [App::DocumentObjectGroupPython] G4_As  # scripted group (container) (typed FeaturePython)
  Dunit = g/cm3
  Dvalue = 5.73
  Group = -> [As_element003]
  conduct = 2
  density = 1
  expand = 3
  formula = As
  name = G4_As
  specific = 4
FEATURE [App::DocumentObjectGroupPython] Se_element001  label="Se_element : 1"  # scripted group (container) (typed FeaturePython)
  n = 1
  ref = Se_element
FEATURE [App::DocumentObjectGroupPython] G4_Se  # scripted group (container) (typed FeaturePython)
  Dunit = g/cm3
  Dvalue = 4.5
  Group = -> [Se_element001]
  conduct = 2
  density = 1
  expand = 3
  formula = Se
  name = G4_Se
  specific = 4
FEATURE [App::DocumentObjectGroupPython] Br_element007  label="Br_element : 004"  # scripted group (container) (typed FeaturePython)
  n = 1
  ref = Br_element
FEATURE [App::DocumentObjectGroupPython] G4_Br  # scripted group (container) (typed FeaturePython)
  Dunit = g/cm3
  Dvalue = 0.0070721
  Group = -> [Br_element007]
  conduct = 2
  density = 1
  expand = 3
  formula = Br
  name = G4_Br
  specific = 4
FEATURE [App::DocumentObjectGroupPython] Kr_element001  label="Kr_element : 1"  # scripted group (container) (typed FeaturePython)
  n = 1
  ref = Kr_element
FEATURE [App::DocumentObjectGroupPython] G4_Kr  # scripted group (container) (typed FeaturePython)
  Dunit = g/cm3
  Dvalue = 0.00347832
  Group = -> [Kr_element001]
  conduct = 2
  density = 1
  expand = 3
  formula = Kr
  name = G4_Kr
  specific = 4
FEATURE [App::DocumentObjectGroupPython] Rb_element001  label="Rb_element : 1"  # scripted group (container) (typed FeaturePython)
  n = 1
  ref = Rb_element
FEATURE [App::DocumentObjectGroupPython] G4_Rb  # scripted group (container) (typed FeaturePython)
  Dunit = g/cm3
  Dvalue = 1.532
  Group = -> [Rb_element001]
  conduct = 2
  density = 1
  expand = 3
  formula = Rb
  name = G4_Rb
  specific = 4
FEATURE [App::DocumentObjectGroupPython] Sr_element001  label="Sr_element : 1"  # scripted group (container) (typed FeaturePython)
  n = 1
  ref = Sr_element
FEATURE [App::DocumentObjectGroupPython] G4_Sr  # scripted group (container) (typed FeaturePython)
  Dunit = g/cm3
  Dvalue = 2.54
  Group = -> [Sr_element001]
  conduct = 2
  density = 1
  expand = 3
  formula = Sr
  name = G4_Sr
  specific = 4
FEATURE [App::DocumentObjectGroupPython] Y_element001  label="Y_element : 1"  # scripted group (container) (typed FeaturePython)
  n = 1
  ref = Y_element
FEATURE [App::DocumentObjectGroupPython] G4_Y  # scripted group (container) (typed FeaturePython)
  Dunit = g/cm3
  Dvalue = 4.469
  Group = -> [Y_element001]
  conduct = 2
  density = 1
  expand = 3
  formula = Y
  name = G4_Y
  specific = 4
FEATURE [App::DocumentObjectGroupPython] Zr_element001  label="Zr_element : 1"  # scripted group (container) (typed FeaturePython)
  n = 1
  ref = Zr_element
FEATURE [App::DocumentObjectGroupPython] G4_Zr  # scripted group (container) (typed FeaturePython)
  Dunit = g/cm3
  Dvalue = 6.506
  Group = -> [Zr_element001]
  conduct = 2
  density = 1
  expand = 3
  formula = Zr
  name = G4_Zr
  specific = 4
FEATURE [App::DocumentObjectGroupPython] Nb_element001  label="Nb_element : 1"  # scripted group (container) (typed FeaturePython)
  n = 1
  ref = Nb_element
FEATURE [App::DocumentObjectGroupPython] G4_Nb  # scripted group (container) (typed FeaturePython)
  Dunit = g/cm3
  Dvalue = 8.57
  Group = -> [Nb_element001]
  conduct = 2
  density = 1
  expand = 3
  formula = Nb
  name = G4_Nb
  specific = 4
FEATURE [App::DocumentObjectGroupPython] Mo_element001  label="Mo_element : 1"  # scripted group (container) (typed FeaturePython)
  n = 1
  ref = Mo_element
FEATURE [App::DocumentObjectGroupPython] G4_Mo  # scripted group (container) (typed FeaturePython)
  Dunit = g/cm3
  Dvalue = 10.22
  Group = -> [Mo_element001]
  conduct = 2
  density = 1
  expand = 3
  formula = Mo
  name = G4_Mo
  specific = 4
FEATURE [App::DocumentObjectGroupPython] Tc_element001  label="Tc_element : 1"  # scripted group (container) (typed FeaturePython)
  n = 1
  ref = Tc_element
FEATURE [App::DocumentObjectGroupPython] G4_Tc  # scripted group (container) (typed FeaturePython)
  Dunit = g/cm3
  Dvalue = 11.5
  Group = -> [Tc_element001]
  conduct = 2
  density = 1
  expand = 3
  formula = Tc
  name = G4_Tc
  specific = 4
FEATURE [App::DocumentObjectGroupPython] Ru_element001  label="Ru_element : 1"  # scripted group (container) (typed FeaturePython)
  n = 1
  ref = Ru_element
FEATURE [App::DocumentObjectGroupPython] G4_Ru  # scripted group (container) (typed FeaturePython)
  Dunit = g/cm3
  Dvalue = 12.41
  Group = -> [Ru_element001]
  conduct = 2
  density = 1
  expand = 3
  formula = Ru
  name = G4_Ru
  specific = 4
FEATURE [App::DocumentObjectGroupPython] Rh_element001  label="Rh_element : 1"  # scripted group (container) (typed FeaturePython)
  n = 1
  ref = Rh_element
FEATURE [App::DocumentObjectGroupPython] G4_Rh  # scripted group (container) (typed FeaturePython)
  Dunit = g/cm3
  Dvalue = 12.41
  Group = -> [Rh_element001]
  conduct = 2
  density = 1
  expand = 3
  formula = Rh
  name = G4_Rh
  specific = 4
FEATURE [App::DocumentObjectGroupPython] Pd_element001  label="Pd_element : 1"  # scripted group (container) (typed FeaturePython)
  n = 1
  ref = Pd_element
FEATURE [App::DocumentObjectGroupPython] G4_Pd  # scripted group (container) (typed FeaturePython)
  Dunit = g/cm3
  Dvalue = 12.02
  Group = -> [Pd_element001]
  conduct = 2
  density = 1
  expand = 3
  formula = Pd
  name = G4_Pd
  specific = 4
FEATURE [App::DocumentObjectGroupPython] Ag_element006  label="Ag_element : 004"  # scripted group (container) (typed FeaturePython)
  n = 1
  ref = Ag_element
FEATURE [App::DocumentObjectGroupPython] G4_Ag  # scripted group (container) (typed FeaturePython)
  Dunit = g/cm3
  Dvalue = 10.5
  Group = -> [Ag_element006]
  conduct = 2
  density = 1
  expand = 3
  formula = Ag
  name = G4_Ag
  specific = 4
FEATURE [App::DocumentObjectGroupPython] Cd_element003  label="Cd_element : 003"  # scripted group (container) (typed FeaturePython)
  n = 1
  ref = Cd_element
FEATURE [App::DocumentObjectGroupPython] G4_Cd  # scripted group (container) (typed FeaturePython)
  Dunit = g/cm3
  Dvalue = 8.65
  Group = -> [Cd_element003]
  conduct = 2
  density = 1
  expand = 3
  formula = Cd
  name = G4_Cd
  specific = 4
FEATURE [App::DocumentObjectGroupPython] In_element001  label="In_element : 1"  # scripted group (container) (typed FeaturePython)
  n = 1
  ref = In_element
FEATURE [App::DocumentObjectGroupPython] G4_In  # scripted group (container) (typed FeaturePython)
  Dunit = g/cm3
  Dvalue = 7.31
  Group = -> [In_element001]
  conduct = 2
  density = 1
  expand = 3
  formula = In
  name = G4_In
  specific = 4
FEATURE [App::DocumentObjectGroupPython] Sn_element001  label="Sn_element : 1"  # scripted group (container) (typed FeaturePython)
  n = 1
  ref = Sn_element
FEATURE [App::DocumentObjectGroupPython] G4_Sn  # scripted group (container) (typed FeaturePython)
  Dunit = g/cm3
  Dvalue = 7.31
  Group = -> [Sn_element001]
  conduct = 2
  density = 1
  expand = 3
  formula = Sn
  name = G4_Sn
  specific = 4
FEATURE [App::DocumentObjectGroupPython] Sb_element001  label="Sb_element : 1"  # scripted group (container) (typed FeaturePython)
  n = 1
  ref = Sb_element
FEATURE [App::DocumentObjectGroupPython] G4_Sb  # scripted group (container) (typed FeaturePython)
  Dunit = g/cm3
  Dvalue = 6.691
  Group = -> [Sb_element001]
  conduct = 2
  density = 1
  expand = 3
  formula = Sb
  name = G4_Sb
  specific = 4
FEATURE [App::DocumentObjectGroupPython] Te_element002  label="Te_element : 002"  # scripted group (container) (typed FeaturePython)
  n = 1
  ref = Te_element
FEATURE [App::DocumentObjectGroupPython] G4_Te  # scripted group (container) (typed FeaturePython)
  Dunit = g/cm3
  Dvalue = 6.24
  Group = -> [Te_element002]
  conduct = 2
  density = 1
  expand = 3
  formula = Te
  name = G4_Te
  specific = 4
FEATURE [App::DocumentObjectGroupPython] I_element010  label="I_element : 006"  # scripted group (container) (typed FeaturePython)
  n = 1
  ref = I_element
FEATURE [App::DocumentObjectGroupPython] G4_I  # scripted group (container) (typed FeaturePython)
  Dunit = g/cm3
  Dvalue = 4.93
  Group = -> [I_element010]
  conduct = 2
  density = 1
  expand = 3
  formula = I
  name = G4_I
  specific = 4
FEATURE [App::DocumentObjectGroupPython] Xe_element001  label="Xe_element : 1"  # scripted group (container) (typed FeaturePython)
  n = 1
  ref = Xe_element
FEATURE [App::DocumentObjectGroupPython] G4_Xe  # scripted group (container) (typed FeaturePython)
  Dunit = g/cm3
  Dvalue = 0.00548536
  Group = -> [Xe_element001]
  conduct = 2
  density = 1
  expand = 3
  formula = Xe
  name = G4_Xe
  specific = 4
FEATURE [App::DocumentObjectGroupPython] Cs_element003  label="Cs_element : 003"  # scripted group (container) (typed FeaturePython)
  n = 1
  ref = Cs_element
FEATURE [App::DocumentObjectGroupPython] G4_Cs  # scripted group (container) (typed FeaturePython)
  Dunit = g/cm3
  Dvalue = 1.873
  Group = -> [Cs_element003]
  conduct = 2
  density = 1
  expand = 3
  formula = Cs
  name = G4_Cs
  specific = 4
FEATURE [App::DocumentObjectGroupPython] Ba_element003  label="Ba_element : 003"  # scripted group (container) (typed FeaturePython)
  n = 1
  ref = Ba_element
FEATURE [App::DocumentObjectGroupPython] G4_Ba  # scripted group (container) (typed FeaturePython)
  Dunit = g/cm3
  Dvalue = 3.5
  Group = -> [Ba_element003]
  conduct = 2
  density = 1
  expand = 3
  formula = Ba
  name = G4_Ba
  specific = 4
FEATURE [App::DocumentObjectGroupPython] La_element003  label="La_element : 003"  # scripted group (container) (typed FeaturePython)
  n = 1
  ref = La_element
FEATURE [App::DocumentObjectGroupPython] G4_La  # scripted group (container) (typed FeaturePython)
  Dunit = g/cm3
  Dvalue = 6.154
  Group = -> [La_element003]
  conduct = 2
  density = 1
  expand = 3
  formula = La
  name = G4_La
  specific = 4
FEATURE [App::DocumentObjectGroupPython] Ce_element002  label="Ce_element : 1"  # scripted group (container) (typed FeaturePython)
  n = 1
  ref = Ce_element
FEATURE [App::DocumentObjectGroupPython] G4_Ce  # scripted group (container) (typed FeaturePython)
  Dunit = g/cm3
  Dvalue = 6.657
  Group = -> [Ce_element002]
  conduct = 2
  density = 1
  expand = 3
  formula = Ce
  name = G4_Ce
  specific = 4
FEATURE [App::DocumentObjectGroupPython] Pr_element001  label="Pr_element : 1"  # scripted group (container) (typed FeaturePython)
  n = 1
  ref = Pr_element
FEATURE [App::DocumentObjectGroupPython] G4_Pr  # scripted group (container) (typed FeaturePython)
  Dunit = g/cm3
  Dvalue = 6.71
  Group = -> [Pr_element001]
  conduct = 2
  density = 1
  expand = 3
  formula = Pr
  name = G4_Pr
  specific = 4
FEATURE [App::DocumentObjectGroupPython] Nd_element001  label="Nd_element : 1"  # scripted group (container) (typed FeaturePython)
  n = 1
  ref = Nd_element
FEATURE [App::DocumentObjectGroupPython] G4_Nd  # scripted group (container) (typed FeaturePython)
  Dunit = g/cm3
  Dvalue = 6.9
  Group = -> [Nd_element001]
  conduct = 2
  density = 1
  expand = 3
  formula = Nd
  name = G4_Nd
  specific = 4
FEATURE [App::DocumentObjectGroupPython] Pm_element001  label="Pm_element : 1"  # scripted group (container) (typed FeaturePython)
  n = 1
  ref = Pm_element
FEATURE [App::DocumentObjectGroupPython] G4_Pm  # scripted group (container) (typed FeaturePython)
  Dunit = g/cm3
  Dvalue = 7.22
  Group = -> [Pm_element001]
  conduct = 2
  density = 1
  expand = 3
  formula = Pm
  name = G4_Pm
  specific = 4
FEATURE [App::DocumentObjectGroupPython] Sm_element001  label="Sm_element : 1"  # scripted group (container) (typed FeaturePython)
  n = 1
  ref = Sm_element
FEATURE [App::DocumentObjectGroupPython] G4_Sm  # scripted group (container) (typed FeaturePython)
  Dunit = g/cm3
  Dvalue = 7.46
  Group = -> [Sm_element001]
  conduct = 2
  density = 1
  expand = 3
  formula = Sm
  name = G4_Sm
  specific = 4
FEATURE [App::DocumentObjectGroupPython] Eu_element001  label="Eu_element : 1"  # scripted group (container) (typed FeaturePython)
  n = 1
  ref = Eu_element
FEATURE [App::DocumentObjectGroupPython] G4_Eu  # scripted group (container) (typed FeaturePython)
  Dunit = g/cm3
  Dvalue = 5.243
  Group = -> [Eu_element001]
  conduct = 2
  density = 1
  expand = 3
  formula = Eu
  name = G4_Eu
  specific = 4
FEATURE [App::DocumentObjectGroupPython] Gd_element002  label="Gd_element : 1"  # scripted group (container) (typed FeaturePython)
  n = 1
  ref = Gd_element
FEATURE [App::DocumentObjectGroupPython] G4_Gd  # scripted group (container) (typed FeaturePython)
  Dunit = g/cm3
  Dvalue = 7.9004
  Group = -> [Gd_element002]
  conduct = 2
  density = 1
  expand = 3
  formula = Gd
  name = G4_Gd
  specific = 4
FEATURE [App::DocumentObjectGroupPython] Tb_element001  label="Tb_element : 1"  # scripted group (container) (typed FeaturePython)
  n = 1
  ref = Tb_element
FEATURE [App::DocumentObjectGroupPython] G4_Tb  # scripted group (container) (typed FeaturePython)
  Dunit = g/cm3
  Dvalue = 8.229
  Group = -> [Tb_element001]
  conduct = 2
  density = 1
  expand = 3
  formula = Tb
  name = G4_Tb
  specific = 4
FEATURE [App::DocumentObjectGroupPython] Dy_element001  label="Dy_element : 1"  # scripted group (container) (typed FeaturePython)
  n = 1
  ref = Dy_element
FEATURE [App::DocumentObjectGroupPython] G4_Dy  # scripted group (container) (typed FeaturePython)
  Dunit = g/cm3
  Dvalue = 8.55
  Group = -> [Dy_element001]
  conduct = 2
  density = 1
  expand = 3
  formula = Dy
  name = G4_Dy
  specific = 4
FEATURE [App::DocumentObjectGroupPython] Ho_element001  label="Ho_element : 1"  # scripted group (container) (typed FeaturePython)
  n = 1
  ref = Ho_element
FEATURE [App::DocumentObjectGroupPython] G4_Ho  # scripted group (container) (typed FeaturePython)
  Dunit = g/cm3
  Dvalue = 8.795
  Group = -> [Ho_element001]
  conduct = 2
  density = 1
  expand = 3
  formula = Ho
  name = G4_Ho
  specific = 4
FEATURE [App::DocumentObjectGroupPython] Er_element001  label="Er_element : 1"  # scripted group (container) (typed FeaturePython)
  n = 1
  ref = Er_element
FEATURE [App::DocumentObjectGroupPython] G4_Er  # scripted group (container) (typed FeaturePython)
  Dunit = g/cm3
  Dvalue = 9.066
  Group = -> [Er_element001]
  conduct = 2
  density = 1
  expand = 3
  formula = Er
  name = G4_Er
  specific = 4
FEATURE [App::DocumentObjectGroupPython] Tm_element001  label="Tm_element : 1"  # scripted group (container) (typed FeaturePython)
  n = 1
  ref = Tm_element
FEATURE [App::DocumentObjectGroupPython] G4_Tm  # scripted group (container) (typed FeaturePython)
  Dunit = g/cm3
  Dvalue = 9.321
  Group = -> [Tm_element001]
  conduct = 2
  density = 1
  expand = 3
  formula = Tm
  name = G4_Tm
  specific = 4
FEATURE [App::DocumentObjectGroupPython] Yb_element001  label="Yb_element : 1"  # scripted group (container) (typed FeaturePython)
  n = 1
  ref = Yb_element
FEATURE [App::DocumentObjectGroupPython] G4_Yb  # scripted group (container) (typed FeaturePython)
  Dunit = g/cm3
  Dvalue = 6.73
  Group = -> [Yb_element001]
  conduct = 2
  density = 1
  expand = 3
  formula = Yb
  name = G4_Yb
  specific = 4
FEATURE [App::DocumentObjectGroupPython] Lu_element001  label="Lu_element : 1"  # scripted group (container) (typed FeaturePython)
  n = 1
  ref = Lu_element
FEATURE [App::DocumentObjectGroupPython] G4_Lu  # scripted group (container) (typed FeaturePython)
  Dunit = g/cm3
  Dvalue = 9.84
  Group = -> [Lu_element001]
  conduct = 2
  density = 1
  expand = 3
  formula = Lu
  name = G4_Lu
  specific = 4
FEATURE [App::DocumentObjectGroupPython] Hf_element001  label="Hf_element : 1"  # scripted group (container) (typed FeaturePython)
  n = 1
  ref = Hf_element
FEATURE [App::DocumentObjectGroupPython] G4_Hf  # scripted group (container) (typed FeaturePython)
  Dunit = g/cm3
  Dvalue = 13.31
  Group = -> [Hf_element001]
  conduct = 2
  density = 1
  expand = 3
  formula = Hf
  name = G4_Hf
  specific = 4
FEATURE [App::DocumentObjectGroupPython] Ta_element001  label="Ta_element : 1"  # scripted group (container) (typed FeaturePython)
  n = 1
  ref = Ta_element
FEATURE [App::DocumentObjectGroupPython] G4_Ta  # scripted group (container) (typed FeaturePython)
  Dunit = g/cm3
  Dvalue = 16.654
  Group = -> [Ta_element001]
  conduct = 2
  density = 1
  expand = 3
  formula = Ta
  name = G4_Ta
  specific = 4
FEATURE [App::DocumentObjectGroupPython] W_element004  label="W_element : 004"  # scripted group (container) (typed FeaturePython)
  n = 1
  ref = W_element
FEATURE [App::DocumentObjectGroupPython] G4_W  # scripted group (container) (typed FeaturePython)
  Dunit = g/cm3
  Dvalue = 19.3
  Group = -> [W_element004]
  conduct = 2
  density = 1
  expand = 3
  formula = W
  name = G4_W
  specific = 4
FEATURE [App::DocumentObjectGroupPython] Re_element001  label="Re_element : 1"  # scripted group (container) (typed FeaturePython)
  n = 1
  ref = Re_element
FEATURE [App::DocumentObjectGroupPython] G4_Re  # scripted group (container) (typed FeaturePython)
  Dunit = g/cm3
  Dvalue = 21.02
  Group = -> [Re_element001]
  conduct = 2
  density = 1
  expand = 3
  formula = Re
  name = G4_Re
  specific = 4
FEATURE [App::DocumentObjectGroupPython] Os_element001  label="Os_element : 1"  # scripted group (container) (typed FeaturePython)
  n = 1
  ref = Os_element
FEATURE [App::DocumentObjectGroupPython] G4_Os  # scripted group (container) (typed FeaturePython)
  Dunit = g/cm3
  Dvalue = 22.57
  Group = -> [Os_element001]
  conduct = 2
  density = 1
  expand = 3
  formula = Os
  name = G4_Os
  specific = 4
FEATURE [App::DocumentObjectGroupPython] Ir_element001  label="Ir_element : 1"  # scripted group (container) (typed FeaturePython)
  n = 1
  ref = Ir_element
FEATURE [App::DocumentObjectGroupPython] G4_Ir  # scripted group (container) (typed FeaturePython)
  Dunit = g/cm3
  Dvalue = 22.42
  Group = -> [Ir_element001]
  conduct = 2
  density = 1
  expand = 3
  formula = Ir
  name = G4_Ir
  specific = 4
FEATURE [App::DocumentObjectGroupPython] Pt_element001  label="Pt_element : 1"  # scripted group (container) (typed FeaturePython)
  n = 1
  ref = Pt_element
FEATURE [App::DocumentObjectGroupPython] G4_Pt  # scripted group (container) (typed FeaturePython)
  Dunit = g/cm3
  Dvalue = 21.45
  Group = -> [Pt_element001]
  conduct = 2
  density = 1
  expand = 3
  formula = Pt
  name = G4_Pt
  specific = 4
FEATURE [App::DocumentObjectGroupPython] Au_element001  label="Au_element : 1"  # scripted group (container) (typed FeaturePython)
  n = 1
  ref = Au_element
FEATURE [App::DocumentObjectGroupPython] G4_Au  # scripted group (container) (typed FeaturePython)
  Dunit = g/cm3
  Dvalue = 19.32
  Group = -> [Au_element001]
  conduct = 2
  density = 1
  expand = 3
  formula = Au
  name = G4_Au
  specific = 4
FEATURE [App::DocumentObjectGroupPython] Hg_element002  label="Hg_element : 002"  # scripted group (container) (typed FeaturePython)
  n = 1
  ref = Hg_element
FEATURE [App::DocumentObjectGroupPython] G4_Hg  # scripted group (container) (typed FeaturePython)
  Dunit = g/cm3
  Dvalue = 13.546
  Group = -> [Hg_element002]
  conduct = 2
  density = 1
  expand = 3
  formula = Hg
  name = G4_Hg
  specific = 4
FEATURE [App::DocumentObjectGroupPython] Tl_element002  label="Tl_element : 002"  # scripted group (container) (typed FeaturePython)
  n = 1
  ref = Tl_element
FEATURE [App::DocumentObjectGroupPython] G4_Tl  # scripted group (container) (typed FeaturePython)
  Dunit = g/cm3
  Dvalue = 11.72
  Group = -> [Tl_element002]
  conduct = 2
  density = 1
  expand = 3
  formula = Tl
  name = G4_Tl
  specific = 4
FEATURE [App::DocumentObjectGroupPython] Pb_element003  label="Pb_element : 1"  # scripted group (container) (typed FeaturePython)
  n = 1
  ref = Pb_element
FEATURE [App::DocumentObjectGroupPython] G4_Pb  # scripted group (container) (typed FeaturePython)
  Dunit = g/cm3
  Dvalue = 11.35
  Group = -> [Pb_element003]
  conduct = 2
  density = 1
  expand = 3
  formula = Pb
  name = G4_Pb
  specific = 4
FEATURE [App::DocumentObjectGroupPython] Bi_element002  label="Bi_element : 1"  # scripted group (container) (typed FeaturePython)
  n = 1
  ref = Bi_element
FEATURE [App::DocumentObjectGroupPython] G4_Bi  # scripted group (container) (typed FeaturePython)
  Dunit = g/cm3
  Dvalue = 9.747
  Group = -> [Bi_element002]
  conduct = 2
  density = 1
  expand = 3
  formula = Bi
  name = G4_Bi
  specific = 4
FEATURE [App::DocumentObjectGroupPython] Po_element001  label="Po_element : 1"  # scripted group (container) (typed FeaturePython)
  n = 1
  ref = Po_element
FEATURE [App::DocumentObjectGroupPython] G4_Po  # scripted group (container) (typed FeaturePython)
  Dunit = g/cm3
  Dvalue = 9.32
  Group = -> [Po_element001]
  conduct = 2
  density = 1
  expand = 3
  formula = Po
  name = G4_Po
  specific = 4
FEATURE [App::DocumentObjectGroupPython] At_element001  label="At_element : 1"  # scripted group (container) (typed FeaturePython)
  n = 1
  ref = At_element
FEATURE [App::DocumentObjectGroupPython] G4_At  # scripted group (container) (typed FeaturePython)
  Dunit = g/cm3
  Dvalue = 9.32
  Group = -> [At_element001]
  conduct = 2
  density = 1
  expand = 3
  formula = At
  name = G4_At
  specific = 4
FEATURE [App::DocumentObjectGroupPython] Rn_element001  label="Rn_element : 1"  # scripted group (container) (typed FeaturePython)
  n = 1
  ref = Rn_element
FEATURE [App::DocumentObjectGroupPython] G4_Rn  # scripted group (container) (typed FeaturePython)
  Dunit = g/cm3
  Dvalue = 0.00900662
  Group = -> [Rn_element001]
  conduct = 2
  density = 1
  expand = 3
  formula = Rn
  name = G4_Rn
  specific = 4
FEATURE [App::DocumentObjectGroupPython] Fr_element001  label="Fr_element : 1"  # scripted group (container) (typed FeaturePython)
  n = 1
  ref = Fr_element
FEATURE [App::DocumentObjectGroupPython] G4_Fr  # scripted group (container) (typed FeaturePython)
  Dunit = g/cm3
  Dvalue = 1
  Group = -> [Fr_element001]
  conduct = 2
  density = 1
  expand = 3
  formula = Fr
  name = G4_Fr
  specific = 4
FEATURE [App::DocumentObjectGroupPython] Ra_element001  label="Ra_element : 1"  # scripted group (container) (typed FeaturePython)
  n = 1
  ref = Ra_element
FEATURE [App::DocumentObjectGroupPython] G4_Ra  # scripted group (container) (typed FeaturePython)
  Dunit = g/cm3
  Dvalue = 5
  Group = -> [Ra_element001]
  conduct = 2
  density = 1
  expand = 3
  formula = Ra
  name = G4_Ra
  specific = 4
FEATURE [App::DocumentObjectGroupPython] Ac_element001  label="Ac_element : 1"  # scripted group (container) (typed FeaturePython)
  n = 1
  ref = Ac_element
FEATURE [App::DocumentObjectGroupPython] G4_Ac  # scripted group (container) (typed FeaturePython)
  Dunit = g/cm3
  Dvalue = 10.07
  Group = -> [Ac_element001]
  conduct = 2
  density = 1
  expand = 3
  formula = Ac
  name = G4_Ac
  specific = 4
FEATURE [App::DocumentObjectGroupPython] Th_element001  label="Th_element : 1"  # scripted group (container) (typed FeaturePython)
  n = 1
  ref = Th_element
FEATURE [App::DocumentObjectGroupPython] G4_Th  # scripted group (container) (typed FeaturePython)
  Dunit = g/cm3
  Dvalue = 11.72
  Group = -> [Th_element001]
  conduct = 2
  density = 1
  expand = 3
  formula = Th
  name = G4_Th
  specific = 4
FEATURE [App::DocumentObjectGroupPython] Pa_element001  label="Pa_element : 1"  # scripted group (container) (typed FeaturePython)
  n = 1
  ref = Pa_element
FEATURE [App::DocumentObjectGroupPython] G4_Pa  # scripted group (container) (typed FeaturePython)
  Dunit = g/cm3
  Dvalue = 15.37
  Group = -> [Pa_element001]
  conduct = 2
  density = 1
  expand = 3
  formula = Pa
  name = G4_Pa
  specific = 4
FEATURE [App::DocumentObjectGroupPython] U_element004  label="U_element : 004"  # scripted group (container) (typed FeaturePython)
  n = 1
  ref = U_element
FEATURE [App::DocumentObjectGroupPython] G4_U  # scripted group (container) (typed FeaturePython)
  Dunit = g/cm3
  Dvalue = 18.95
  Group = -> [U_element004]
  conduct = 2
  density = 1
  expand = 3
  formula = U
  name = G4_U
  specific = 4
FEATURE [App::DocumentObjectGroupPython] Np_element001  label="Np_element : 1"  # scripted group (container) (typed FeaturePython)
  n = 1
  ref = Np_element
FEATURE [App::DocumentObjectGroupPython] G4_Np  # scripted group (container) (typed FeaturePython)
  Dunit = g/cm3
  Dvalue = 20.25
  Group = -> [Np_element001]
  conduct = 2
  density = 1
  expand = 3
  formula = Np
  name = G4_Np
  specific = 4
FEATURE [App::DocumentObjectGroupPython] Pu_element002  label="Pu_element : 002"  # scripted group (container) (typed FeaturePython)
  n = 1
  ref = Pu_element
FEATURE [App::DocumentObjectGroupPython] G4_Pu  # scripted group (container) (typed FeaturePython)
  Dunit = g/cm3
  Dvalue = 19.84
  Group = -> [Pu_element002]
  conduct = 2
  density = 1
  expand = 3
  formula = Pu
  name = G4_Pu
  specific = 4
FEATURE [App::DocumentObjectGroupPython] Am_element001  label="Am_element : 1"  # scripted group (container) (typed FeaturePython)
  n = 1
  ref = Am_element
FEATURE [App::DocumentObjectGroupPython] G4_Am  # scripted group (container) (typed FeaturePython)
  Dunit = g/cm3
  Dvalue = 13.67
  Group = -> [Am_element001]
  conduct = 2
  density = 1
  expand = 3
  formula = Am
  name = G4_Am
  specific = 4
FEATURE [App::DocumentObjectGroupPython] Cm_element001  label="Cm_element : 1"  # scripted group (container) (typed FeaturePython)
  n = 1
  ref = Cm_element
FEATURE [App::DocumentObjectGroupPython] G4_Cm  # scripted group (container) (typed FeaturePython)
  Dunit = g/cm3
  Dvalue = 13.51
  Group = -> [Cm_element001]
  conduct = 2
  density = 1
  expand = 3
  formula = Cm
  name = G4_Cm
  specific = 4
FEATURE [App::DocumentObjectGroupPython] Bk_element001  label="Bk_element : 1"  # scripted group (container) (typed FeaturePython)
  n = 1
  ref = Bk_element
FEATURE [App::DocumentObjectGroupPython] G4_Bk  # scripted group (container) (typed FeaturePython)
  Dunit = g/cm3
  Dvalue = 14
  Group = -> [Bk_element001]
  conduct = 2
  density = 1
  expand = 3
  formula = Bk
  name = G4_Bk
  specific = 4
FEATURE [App::DocumentObjectGroupPython] Cf_element001  label="Cf_element : 1"  # scripted group (container) (typed FeaturePython)
  n = 1
  ref = Cf_element
FEATURE [App::DocumentObjectGroupPython] G4_Cf  # scripted group (container) (typed FeaturePython)
  Dunit = g/cm3
  Dvalue = 10
  Group = -> [Cf_element001]
  conduct = 2
  density = 1
  expand = 3
  formula = Cf
  name = G4_Cf
  specific = 4
FEATURE [App::DocumentObjectGroupPython] Element  # scripted group (container) (typed FeaturePython)
  Group = -> [G4_H,G4_He,G4_Li,G4_Be,G4_B,G4_C,G4_N,G4_O,G4_F,G4_Ne,G4_Na,G4_Mg,G4_Al,G4_Si,G4_P,G4_S,G4_Cl,G4_Ar,G4_K,G4_Ca,G4_Sc,G4_Ti,G4_V,G4_Cr,G4_Mn,G4_Fe,G4_Co,G4_Ni,G4_Cu,G4_Zn,G4_Ga,G4_Ge,G4_As,G4_Se,G4_Br,G4_Kr,G4_Rb,G4_Sr,G4_Y,G4_Zr,G4_Nb,G4_Mo,G4_Tc,G4_Ru,G4_Rh,G4_Pd,G4_Ag,G4_Cd,G4_In,G4_Sn,G4_Sb,G4_Te,G4_I,G4_Xe,G4_Cs,G4_Ba,G4_La,G4_Ce,G4_Pr,G4_Nd,G4_Pm,G4_Sm,G4_Eu,G4_Gd,G4_Tb,G4_Dy,G4_Ho,G4_Er,+30 more]
FEATURE [App::DocumentObjectGroupPython] H_element114  label="H_element : 063"  # scripted group (container) (typed FeaturePython)
  n = 2
  ref = H_element
FEATURE [App::DocumentObjectGroupPython] G4_lH2  # scripted group (container) (typed FeaturePython)
  Dunit = g/cm3
  Dvalue = 0.0708
  Group = -> [H_element114]
  conduct = 2
  density = 1
  expand = 3
  formula = G4_lH2
  name = G4_lH2
  specific = 4
FEATURE [App::DocumentObjectGroupPython] N_element049  label="N_element : 022"  # scripted group (container) (typed FeaturePython)
  n = 2
  ref = N_element
FEATURE [App::DocumentObjectGroupPython] G4_lN2  # scripted group (container) (typed FeaturePython)
  Dunit = g/cm3
  Dvalue = 0.807
  Group = -> [N_element049]
  conduct = 2
  density = 1
  expand = 3
  formula = G4_lN2
  name = G4_lN2
  specific = 4
FEATURE [App::DocumentObjectGroupPython] O_element106  label="O_element : 060"  # scripted group (container) (typed FeaturePython)
  n = 2
  ref = O_element
FEATURE [App::DocumentObjectGroupPython] G4_lO2  # scripted group (container) (typed FeaturePython)
  Dunit = g/cm3
  Dvalue = 1.141
  Group = -> [O_element106]
  conduct = 2
  density = 1
  expand = 3
  formula = G4_lO2
  name = G4_lO2
  specific = 4
FEATURE [App::DocumentObjectGroupPython] Ar  label="Ar : 1"  # scripted group (container) (typed FeaturePython)
  n = 1
  ref = Ar
FEATURE [App::DocumentObjectGroupPython] G4_lAr  # scripted group (container) (typed FeaturePython)
  Dunit = g/cm3
  Dvalue = 1.396
  Group = -> [Ar]
  conduct = 2
  density = 1
  expand = 3
  formula = G4_lAr
  name = G4_lAr
  specific = 4
FEATURE [App::DocumentObjectGroupPython] Br  label="Br : 1"  # scripted group (container) (typed FeaturePython)
  n = 1
  ref = Br
FEATURE [App::DocumentObjectGroupPython] G4_lBr  # scripted group (container) (typed FeaturePython)
  Dunit = g/cm3
  Dvalue = 3.1028
  Group = -> [Br]
  conduct = 2
  density = 1
  expand = 3
  formula = G4_lBr
  name = G4_lBr
  specific = 4
FEATURE [App::DocumentObjectGroupPython] Kr  label="Kr : 1"  # scripted group (container) (typed FeaturePython)
  n = 1
  ref = Kr
FEATURE [App::DocumentObjectGroupPython] G4_lKr  # scripted group (container) (typed FeaturePython)
  Dunit = g/cm3
  Dvalue = 2.418
  Group = -> [Kr]
  conduct = 2
  density = 1
  expand = 3
  formula = G4_lKr
  name = G4_lKr
  specific = 4
FEATURE [App::DocumentObjectGroupPython] Xe  label="Xe : 1"  # scripted group (container) (typed FeaturePython)
  n = 1
  ref = Xe
FEATURE [App::DocumentObjectGroupPython] G4_lXe  # scripted group (container) (typed FeaturePython)
  Dunit = g/cm3
  Dvalue = 2.953
  Group = -> [Xe]
  conduct = 2
  density = 1
  expand = 3
  formula = G4_lXe
  name = G4_lXe
  specific = 4
FEATURE [App::DocumentObjectGroupPython] O_element107  label="O_element : 061"  # scripted group (container) (typed FeaturePython)
  n = 4
  ref = O_element
FEATURE [App::DocumentObjectGroupPython] Pb_element004  label="Pb_element : 002"  # scripted group (container) (typed FeaturePython)
  n = 1
  ref = Pb_element
FEATURE [App::DocumentObjectGroupPython] W_element005  label="W_element : 005"  # scripted group (container) (typed FeaturePython)
  n = 1
  ref = W_element
FEATURE [App::DocumentObjectGroupPython] G4_PbWO4  # scripted group (container) (typed FeaturePython)
  Dunit = g/cm3
  Dvalue = 8.28
  Group = -> [O_element107,Pb_element004,W_element005]
  conduct = 2
  density = 1
  expand = 3
  formula = G4_PbWO4
  name = G4_PbWO4
  specific = 4
FEATURE [App::DocumentObjectGroupPython] alactic  label="alactic : 1"  # scripted group (container) (typed FeaturePython)
  n = 1
  ref = alactic
FEATURE [App::DocumentObjectGroupPython] G4_Galactic  # scripted group (container) (typed FeaturePython)
  Dunit = g/cm3
  Dvalue = 0
  Group = -> [alactic]
  conduct = 2
  density = 1
  expand = 3
  formula = G4_Galactic
  name = G4_Galactic
  specific = 4
FEATURE [App::DocumentObjectGroupPython] RAPHITE_POROUS  label="RAPHITE_POROUS : 1"  # scripted group (container) (typed FeaturePython)
  n = 1
  ref = RAPHITE_POROUS
FEATURE [App::DocumentObjectGroupPython] G4_GRAPHITE_POROUS  # scripted group (container) (typed FeaturePython)
  Dunit = g/cm3
  Dvalue = 1.7
  Group = -> [RAPHITE_POROUS]
  conduct = 2
  density = 1
  expand = 3
  formula = G4_GRAPHITE_POROUS
  name = G4_GRAPHITE_POROUS
  specific = 4
FEATURE [App::DocumentObjectGroupPython] H_element115  label="H_element : 0.150"  # scripted group (container) (typed FeaturePython)
  n = 0.080538
FEATURE [App::DocumentObjectGroupPython] C_element125  label="C_element : 0.600"  # scripted group (container) (typed FeaturePython)
  n = 0.599848
FEATURE [App::DocumentObjectGroupPython] O_element108  label="O_element : 0.320"  # scripted group (container) (typed FeaturePython)
  n = 0.319614
FEATURE [App::DocumentObjectGroupPython] G4_LUCITE  # scripted group (container) (typed FeaturePython)
  Dunit = g/cm3
  Dvalue = 1.19
  Group = -> [H_element115,C_element125,O_element108]
  conduct = 2
  density = 1
  expand = 3
  formula = G4_LUCITE
  name = G4_LUCITE
  specific = 4
FEATURE [App::DocumentObjectGroupPython] Cu_element002  label="Cu_element : 62"  # scripted group (container) (typed FeaturePython)
  n = 62
  ref = Cu_element
FEATURE [App::DocumentObjectGroupPython] Zn_element002  label="Zn_element : 35"  # scripted group (container) (typed FeaturePython)
  n = 35
  ref = Zn_element
FEATURE [App::DocumentObjectGroupPython] Pb_element005  label="Pb_element : 3"  # scripted group (container) (typed FeaturePython)
  n = 3
  ref = Pb_element
FEATURE [App::DocumentObjectGroupPython] G4_BRASS  # scripted group (container) (typed FeaturePython)
  Dunit = g/cm3
  Dvalue = 8.52
  Group = -> [Cu_element002,Zn_element002,Pb_element005]
  conduct = 2
  density = 1
  expand = 3
  formula = G4_BRASS
  name = G4_BRASS
  specific = 4
FEATURE [App::DocumentObjectGroupPython] Cu_element003  label="Cu_element : 89"  # scripted group (container) (typed FeaturePython)
  n = 89
  ref = Cu_element
FEATURE [App::DocumentObjectGroupPython] Zn_element003  label="Zn_element : 9"  # scripted group (container) (typed FeaturePython)
  n = 9
  ref = Zn_element
FEATURE [App::DocumentObjectGroupPython] Pb_element006  label="Pb_element : 2"  # scripted group (container) (typed FeaturePython)
  n = 2
  ref = Pb_element
FEATURE [App::DocumentObjectGroupPython] G4_BRONZE  # scripted group (container) (typed FeaturePython)
  Dunit = g/cm3
  Dvalue = 8.82
  Group = -> [Cu_element003,Zn_element003,Pb_element006]
  conduct = 2
  density = 1
  expand = 3
  formula = G4_BRONZE
  name = G4_BRONZE
  specific = 4
FEATURE [App::DocumentObjectGroupPython] Fe_element008  label="Fe_element : 74"  # scripted group (container) (typed FeaturePython)
  n = 74
  ref = Fe_element
FEATURE [App::DocumentObjectGroupPython] Cr_element002  label="Cr_element : 18"  # scripted group (container) (typed FeaturePython)
  n = 18
  ref = Cr_element
FEATURE [App::DocumentObjectGroupPython] Ni_element002  label="Ni_element : 8"  # scripted group (container) (typed FeaturePython)
  n = 8
  ref = Ni_element
FEATURE [App::DocumentObjectGroupPython] G4_STAINLESS_STEEL  label="G4_STAINLESS-STEEL"  # scripted group (container) (typed FeaturePython)
  Dunit = g/cm3
  Dvalue = 8
  Group = -> [Fe_element008,Cr_element002,Ni_element002]
  conduct = 2
  density = 1
  expand = 3
  formula = G4_STAINLESS-STEEL
  name = G4_STAINLESS-STEEL
  specific = 4
FEATURE [App::DocumentObjectGroupPython] H_element116  label="H_element : 064"  # scripted group (container) (typed FeaturePython)
  n = 18
  ref = H_element
FEATURE [App::DocumentObjectGroupPython] C_element126  label="C_element : 071"  # scripted group (container) (typed FeaturePython)
  n = 12
  ref = C_element
FEATURE [App::DocumentObjectGroupPython] O_element109  label="O_element : 062"  # scripted group (container) (typed FeaturePython)
  n = 7
  ref = O_element
FEATURE [App::DocumentObjectGroupPython] G4_CR39  # scripted group (container) (typed FeaturePython)
  Dunit = g/cm3
  Dvalue = 1.32
  Group = -> [H_element116,C_element126,O_element109]
  conduct = 2
  density = 1
  expand = 3
  formula = G4_CR39
  name = G4_CR39
  specific = 4
FEATURE [App::DocumentObjectGroupPython] H_element117  label="H_element : 38"  # scripted group (container) (typed FeaturePython)
  n = 38
  ref = H_element
FEATURE [App::DocumentObjectGroupPython] C_element127  label="C_element : 072"  # scripted group (container) (typed FeaturePython)
  n = 18
  ref = C_element
FEATURE [App::DocumentObjectGroupPython] O_element110  label="O_element : 063"  # scripted group (container) (typed FeaturePython)
  n = 1
  ref = O_element
FEATURE [App::DocumentObjectGroupPython] G4_OCTADECANOL  # scripted group (container) (typed FeaturePython)
  Dunit = g/cm3
  Dvalue = 0.812
  Group = -> [H_element117,C_element127,O_element110]
  conduct = 2
  density = 1
  expand = 3
  formula = G4_OCTADECANOL
  name = G4_OCTADECANOL
  specific = 4
FEATURE [App::DocumentObjectGroupPython] HEP  # scripted group (container) (typed FeaturePython)
  Group = -> [G4_lH2,G4_lN2,G4_lO2,G4_lAr,G4_lBr,G4_lKr,G4_lXe,G4_PbWO4,G4_Galactic,G4_GRAPHITE_POROUS,G4_LUCITE,G4_BRASS,G4_BRONZE,G4_STAINLESS_STEEL,G4_CR39,G4_OCTADECANOL]
FEATURE [App::DocumentObjectGroupPython] C_element128  label="C_element : 073"  # scripted group (container) (typed FeaturePython)
  n = 14
  ref = C_element
FEATURE [App::DocumentObjectGroupPython] H_element118  label="H_element : 065"  # scripted group (container) (typed FeaturePython)
  n = 10
  ref = H_element
FEATURE [App::DocumentObjectGroupPython] O_element111  label="O_element : 064"  # scripted group (container) (typed FeaturePython)
  n = 2
  ref = O_element
FEATURE [App::DocumentObjectGroupPython] N_element050  label="N_element : 023"  # scripted group (container) (typed FeaturePython)
  n = 2
  ref = N_element
FEATURE [App::DocumentObjectGroupPython] G4_KEVLAR  # scripted group (container) (typed FeaturePython)
  Dunit = g/cm3
  Dvalue = 1.44
  Group = -> [C_element128,H_element118,O_element111,N_element050]
  conduct = 2
  density = 1
  expand = 3
  formula = G4_KEVLAR
  name = G4_KEVLAR
  specific = 4
FEATURE [App::DocumentObjectGroupPython] C_element129  label="C_element : 074"  # scripted group (container) (typed FeaturePython)
  n = 10
  ref = C_element
FEATURE [App::DocumentObjectGroupPython] H_element119  label="H_element : 066"  # scripted group (container) (typed FeaturePython)
  n = 8
  ref = H_element
FEATURE [App::DocumentObjectGroupPython] O_element112  label="O_element : 065"  # scripted group (container) (typed FeaturePython)
  n = 4
  ref = O_element
FEATURE [App::DocumentObjectGroupPython] G4_DACRON  # scripted group (container) (typed FeaturePython)
  Dunit = g/cm3
  Dvalue = 1.4
  Group = -> [C_element129,H_element119,O_element112]
  conduct = 2
  density = 1
  expand = 3
  formula = G4_DACRON
  name = G4_DACRON
  specific = 4
FEATURE [App::DocumentObjectGroupPython] C_element130  label="C_element : 075"  # scripted group (container) (typed FeaturePython)
  n = 4
  ref = C_element
FEATURE [App::DocumentObjectGroupPython] H_element120  label="H_element : 067"  # scripted group (container) (typed FeaturePython)
  n = 5
  ref = H_element
FEATURE [App::DocumentObjectGroupPython] Cl_element030  label="Cl_element : 016"  # scripted group (container) (typed FeaturePython)
  n = 1
  ref = Cl_element
FEATURE [App::DocumentObjectGroupPython] G4_NEOPRENE  # scripted group (container) (typed FeaturePython)
  Dunit = g/cm3
  Dvalue = 1.23
  Group = -> [C_element130,H_element120,Cl_element030]
  conduct = 2
  density = 1
  expand = 3
  formula = G4_NEOPRENE
  name = G4_NEOPRENE
  specific = 4
FEATURE [App::DocumentObjectGroupPython] Space  # scripted group (container) (typed FeaturePython)
  Group = -> [G4_KEVLAR,G4_DACRON,G4_NEOPRENE]
FEATURE [App::DocumentObjectGroupPython] H_element121  label="H_element : 068"  # scripted group (container) (typed FeaturePython)
  n = 5
  ref = H_element
FEATURE [App::DocumentObjectGroupPython] C_element131  label="C_element : 076"  # scripted group (container) (typed FeaturePython)
  n = 4
  ref = C_element
FEATURE [App::DocumentObjectGroupPython] N_element051  label="N_element : 3"  # scripted group (container) (typed FeaturePython)
  n = 3
  ref = N_element
FEATURE [App::DocumentObjectGroupPython] O_element113  label="O_element : 066"  # scripted group (container) (typed FeaturePython)
  n = 1
  ref = O_element
FEATURE [App::DocumentObjectGroupPython] G4_CYTOSINE  # scripted group (container) (typed FeaturePython)
  Dunit = g/cm3
  Dvalue = 1.55
  Group = -> [H_element121,C_element131,N_element051,O_element113]
  conduct = 2
  density = 1
  expand = 3
  formula = G4_CYTOSINE
  name = G4_CYTOSINE
  specific = 4
FEATURE [App::DocumentObjectGroupPython] H_element122  label="H_element : 069"  # scripted group (container) (typed FeaturePython)
  n = 6
  ref = H_element
FEATURE [App::DocumentObjectGroupPython] C_element132  label="C_element : 077"  # scripted group (container) (typed FeaturePython)
  n = 5
  ref = C_element
FEATURE [App::DocumentObjectGroupPython] N_element052  label="N_element : 024"  # scripted group (container) (typed FeaturePython)
  n = 2
  ref = N_element
FEATURE [App::DocumentObjectGroupPython] O_element114  label="O_element : 067"  # scripted group (container) (typed FeaturePython)
  n = 2
  ref = O_element
FEATURE [App::DocumentObjectGroupPython] G4_THYMINE  # scripted group (container) (typed FeaturePython)
  Dunit = g/cm3
  Dvalue = 1.23
  Group = -> [H_element122,C_element132,N_element052,O_element114]
  conduct = 2
  density = 1
  expand = 3
  formula = G4_THYMINE
  name = G4_THYMINE
  specific = 4
FEATURE [App::DocumentObjectGroupPython] H_element123  label="H_element : 070"  # scripted group (container) (typed FeaturePython)
  n = 4
  ref = H_element
FEATURE [App::DocumentObjectGroupPython] C_element133  label="C_element : 078"  # scripted group (container) (typed FeaturePython)
  n = 4
  ref = C_element
FEATURE [App::DocumentObjectGroupPython] N_element053  label="N_element : 025"  # scripted group (container) (typed FeaturePython)
  n = 2
  ref = N_element
FEATURE [App::DocumentObjectGroupPython] O_element115  label="O_element : 068"  # scripted group (container) (typed FeaturePython)
  n = 2
  ref = O_element
FEATURE [App::DocumentObjectGroupPython] G4_URACIL  # scripted group (container) (typed FeaturePython)
  Dunit = g/cm3
  Dvalue = 1.32
  Group = -> [H_element123,C_element133,N_element053,O_element115]
  conduct = 2
  density = 1
  expand = 3
  formula = G4_URACIL
  name = G4_URACIL
  specific = 4
FEATURE [App::DocumentObjectGroupPython] H_element124  label="H_element : 071"  # scripted group (container) (typed FeaturePython)
  n = 4
  ref = H_element
FEATURE [App::DocumentObjectGroupPython] C_element134  label="C_element : 079"  # scripted group (container) (typed FeaturePython)
  n = 5
  ref = C_element
FEATURE [App::DocumentObjectGroupPython] N_element054  label="N_element : 026"  # scripted group (container) (typed FeaturePython)
  n = 5
  ref = N_element
FEATURE [App::DocumentObjectGroupPython] G4_DNA_ADENINE  # scripted group (container) (typed FeaturePython)
  Dunit = g/cm3
  Dvalue = 1
  Group = -> [H_element124,C_element134,N_element054]
  conduct = 2
  density = 1
  expand = 3
  formula = G4_DNA_ADENINE
  name = G4_DNA_ADENINE
  specific = 4
FEATURE [App::DocumentObjectGroupPython] H_element125  label="H_element : 072"  # scripted group (container) (typed FeaturePython)
  n = 4
  ref = H_element
FEATURE [App::DocumentObjectGroupPython] C_element135  label="C_element : 080"  # scripted group (container) (typed FeaturePython)
  n = 5
  ref = C_element
FEATURE [App::DocumentObjectGroupPython] N_element055  label="N_element : 027"  # scripted group (container) (typed FeaturePython)
  n = 5
  ref = N_element
FEATURE [App::DocumentObjectGroupPython] O_element116  label="O_element : 069"  # scripted group (container) (typed FeaturePython)
  n = 1
  ref = O_element
FEATURE [App::DocumentObjectGroupPython] G4_DNA_GUANINE  # scripted group (container) (typed FeaturePython)
  Dunit = g/cm3
  Dvalue = 1
  Group = -> [H_element125,C_element135,N_element055,O_element116]
  conduct = 2
  density = 1
  expand = 3
  formula = G4_DNA_GUANINE
  name = G4_DNA_GUANINE
  specific = 4
FEATURE [App::DocumentObjectGroupPython] H_element126  label="H_element : 073"  # scripted group (container) (typed FeaturePython)
  n = 4
  ref = H_element
FEATURE [App::DocumentObjectGroupPython] C_element136  label="C_element : 081"  # scripted group (container) (typed FeaturePython)
  n = 4
  ref = C_element
FEATURE [App::DocumentObjectGroupPython] N_element056  label="N_element : 028"  # scripted group (container) (typed FeaturePython)
  n = 3
  ref = N_element
FEATURE [App::DocumentObjectGroupPython] O_element117  label="O_element : 070"  # scripted group (container) (typed FeaturePython)
  n = 1
  ref = O_element
FEATURE [App::DocumentObjectGroupPython] G4_DNA_CYTOSINE  # scripted group (container) (typed FeaturePython)
  Dunit = g/cm3
  Dvalue = 1
  Group = -> [H_element126,C_element136,N_element056,O_element117]
  conduct = 2
  density = 1
  expand = 3
  formula = G4_DNA_CYTOSINE
  name = G4_DNA_CYTOSINE
  specific = 4
FEATURE [App::DocumentObjectGroupPython] H_element127  label="H_element : 074"  # scripted group (container) (typed FeaturePython)
  n = 5
  ref = H_element
FEATURE [App::DocumentObjectGroupPython] C_element137  label="C_element : 082"  # scripted group (container) (typed FeaturePython)
  n = 5
  ref = C_element
FEATURE [App::DocumentObjectGroupPython] N_element057  label="N_element : 029"  # scripted group (container) (typed FeaturePython)
  n = 2
  ref = N_element
FEATURE [App::DocumentObjectGroupPython] O_element118  label="O_element : 071"  # scripted group (container) (typed FeaturePython)
  n = 2
  ref = O_element
FEATURE [App::DocumentObjectGroupPython] G4_DNA_THYMINE  # scripted group (container) (typed FeaturePython)
  Dunit = g/cm3
  Dvalue = 1
  Group = -> [H_element127,C_element137,N_element057,O_element118]
  conduct = 2
  density = 1
  expand = 3
  formula = G4_DNA_THYMINE
  name = G4_DNA_THYMINE
  specific = 4
FEATURE [App::DocumentObjectGroupPython] H_element128  label="H_element : 075"  # scripted group (container) (typed FeaturePython)
  n = 3
  ref = H_element
FEATURE [App::DocumentObjectGroupPython] C_element138  label="C_element : 083"  # scripted group (container) (typed FeaturePython)
  n = 4
  ref = C_element
FEATURE [App::DocumentObjectGroupPython] N_element058  label="N_element : 030"  # scripted group (container) (typed FeaturePython)
  n = 2
  ref = N_element
FEATURE [App::DocumentObjectGroupPython] O_element119  label="O_element : 072"  # scripted group (container) (typed FeaturePython)
  n = 2
  ref = O_element
FEATURE [App::DocumentObjectGroupPython] G4_DNA_URACIL  # scripted group (container) (typed FeaturePython)
  Dunit = g/cm3
  Dvalue = 1
  Group = -> [H_element128,C_element138,N_element058,O_element119]
  conduct = 2
  density = 1
  expand = 3
  formula = G4_DNA_URACIL
  name = G4_DNA_URACIL
  specific = 4
FEATURE [App::DocumentObjectGroupPython] H_element129  label="H_element : 076"  # scripted group (container) (typed FeaturePython)
  n = 10
  ref = H_element
FEATURE [App::DocumentObjectGroupPython] C_element139  label="C_element : 084"  # scripted group (container) (typed FeaturePython)
  n = 10
  ref = C_element
FEATURE [App::DocumentObjectGroupPython] N_element059  label="N_element : 031"  # scripted group (container) (typed FeaturePython)
  n = 5
  ref = N_element
FEATURE [App::DocumentObjectGroupPython] O_element120  label="O_element : 073"  # scripted group (container) (typed FeaturePython)
  n = 4
  ref = O_element
FEATURE [App::DocumentObjectGroupPython] G4_DNA_ADENOSINE  # scripted group (container) (typed FeaturePython)
  Dunit = g/cm3
  Dvalue = 1
  Group = -> [H_element129,C_element139,N_element059,O_element120]
  conduct = 2
  density = 1
  expand = 3
  formula = G4_DNA_ADENOSINE
  name = G4_DNA_ADENOSINE
  specific = 4
FEATURE [App::DocumentObjectGroupPython] H_element130  label="H_element : 077"  # scripted group (container) (typed FeaturePython)
  n = 10
  ref = H_element
FEATURE [App::DocumentObjectGroupPython] C_element140  label="C_element : 085"  # scripted group (container) (typed FeaturePython)
  n = 10
  ref = C_element
FEATURE [App::DocumentObjectGroupPython] N_element060  label="N_element : 032"  # scripted group (container) (typed FeaturePython)
  n = 5
  ref = N_element
FEATURE [App::DocumentObjectGroupPython] O_element121  label="O_element : 074"  # scripted group (container) (typed FeaturePython)
  n = 5
  ref = O_element
FEATURE [App::DocumentObjectGroupPython] G4_DNA_GUANOSINE  # scripted group (container) (typed FeaturePython)
  Dunit = g/cm3
  Dvalue = 1
  Group = -> [H_element130,C_element140,N_element060,O_element121]
  conduct = 2
  density = 1
  expand = 3
  formula = G4_DNA_GUANOSINE
  name = G4_DNA_GUANOSINE
  specific = 4
FEATURE [App::DocumentObjectGroupPython] H_element131  label="H_element : 078"  # scripted group (container) (typed FeaturePython)
  n = 10
  ref = H_element
FEATURE [App::DocumentObjectGroupPython] C_element141  label="C_element : 086"  # scripted group (container) (typed FeaturePython)
  n = 9
  ref = C_element
FEATURE [App::DocumentObjectGroupPython] N_element061  label="N_element : 033"  # scripted group (container) (typed FeaturePython)
  n = 3
  ref = N_element
FEATURE [App::DocumentObjectGroupPython] O_element122  label="O_element : 075"  # scripted group (container) (typed FeaturePython)
  n = 5
  ref = O_element
FEATURE [App::DocumentObjectGroupPython] G4_DNA_CYTIDINE  # scripted group (container) (typed FeaturePython)
  Dunit = g/cm3
  Dvalue = 1
  Group = -> [H_element131,C_element141,N_element061,O_element122]
  conduct = 2
  density = 1
  expand = 3
  formula = G4_DNA_CYTIDINE
  name = G4_DNA_CYTIDINE
  specific = 4
FEATURE [App::DocumentObjectGroupPython] H_element132  label="H_element : 079"  # scripted group (container) (typed FeaturePython)
  n = 9
  ref = H_element
FEATURE [App::DocumentObjectGroupPython] C_element142  label="C_element : 087"  # scripted group (container) (typed FeaturePython)
  n = 9
  ref = C_element
FEATURE [App::DocumentObjectGroupPython] N_element062  label="N_element : 034"  # scripted group (container) (typed FeaturePython)
  n = 2
  ref = N_element
FEATURE [App::DocumentObjectGroupPython] O_element123  label="O_element : 076"  # scripted group (container) (typed FeaturePython)
  n = 6
  ref = O_element
FEATURE [App::DocumentObjectGroupPython] G4_DNA_URIDINE  # scripted group (container) (typed FeaturePython)
  Dunit = g/cm3
  Dvalue = 1
  Group = -> [H_element132,C_element142,N_element062,O_element123]
  conduct = 2
  density = 1
  expand = 3
  formula = G4_DNA_URIDINE
  name = G4_DNA_URIDINE
  specific = 4
FEATURE [App::DocumentObjectGroupPython] H_element133  label="H_element : 080"  # scripted group (container) (typed FeaturePython)
  n = 11
  ref = H_element
FEATURE [App::DocumentObjectGroupPython] C_element143  label="C_element : 088"  # scripted group (container) (typed FeaturePython)
  n = 10
  ref = C_element
FEATURE [App::DocumentObjectGroupPython] N_element063  label="N_element : 035"  # scripted group (container) (typed FeaturePython)
  n = 2
  ref = N_element
FEATURE [App::DocumentObjectGroupPython] O_element124  label="O_element : 077"  # scripted group (container) (typed FeaturePython)
  n = 6
  ref = O_element
FEATURE [App::DocumentObjectGroupPython] G4_DNA_METHYLURIDINE  # scripted group (container) (typed FeaturePython)
  Dunit = g/cm3
  Dvalue = 1
  Group = -> [H_element133,C_element143,N_element063,O_element124]
  conduct = 2
  density = 1
  expand = 3
  formula = G4_DNA_METHYLURIDINE
  name = G4_DNA_METHYLURIDINE
  specific = 4
FEATURE [App::DocumentObjectGroupPython] P_element014  label="P_element : 003"  # scripted group (container) (typed FeaturePython)
  n = 1
  ref = P_element
FEATURE [App::DocumentObjectGroupPython] O_element125  label="O_element : 078"  # scripted group (container) (typed FeaturePython)
  n = 3
  ref = O_element
FEATURE [App::DocumentObjectGroupPython] G4_DNA_MONOPHOSPHATE  # scripted group (container) (typed FeaturePython)
  Dunit = g/cm3
  Dvalue = 1
  Group = -> [P_element014,O_element125]
  conduct = 2
  density = 1
  expand = 3
  formula = G4_DNA_MONOPHOSPHATE
  name = G4_DNA_MONOPHOSPHATE
  specific = 4
FEATURE [App::DocumentObjectGroupPython] H_element134  label="H_element : 081"  # scripted group (container) (typed FeaturePython)
  n = 10
  ref = H_element
FEATURE [App::DocumentObjectGroupPython] C_element144  label="C_element : 089"  # scripted group (container) (typed FeaturePython)
  n = 10
  ref = C_element
FEATURE [App::DocumentObjectGroupPython] N_element064  label="N_element : 036"  # scripted group (container) (typed FeaturePython)
  n = 5
  ref = N_element
FEATURE [App::DocumentObjectGroupPython] O_element126  label="O_element : 079"  # scripted group (container) (typed FeaturePython)
  n = 7
  ref = O_element
FEATURE [App::DocumentObjectGroupPython] P_element015  label="P_element : 004"  # scripted group (container) (typed FeaturePython)
  n = 1
  ref = P_element
FEATURE [App::DocumentObjectGroupPython] G4_DNA_A  # scripted group (container) (typed FeaturePython)
  Dunit = g/cm3
  Dvalue = 1
  Group = -> [H_element134,C_element144,N_element064,O_element126,P_element015]
  conduct = 2
  density = 1
  expand = 3
  formula = G4_DNA_A
  name = G4_DNA_A
  specific = 4
FEATURE [App::DocumentObjectGroupPython] H_element135  label="H_element : 082"  # scripted group (container) (typed FeaturePython)
  n = 10
  ref = H_element
FEATURE [App::DocumentObjectGroupPython] C_element145  label="C_element : 090"  # scripted group (container) (typed FeaturePython)
  n = 10
  ref = C_element
FEATURE [App::DocumentObjectGroupPython] N_element065  label="N_element : 037"  # scripted group (container) (typed FeaturePython)
  n = 5
  ref = N_element
FEATURE [App::DocumentObjectGroupPython] O_element127  label="O_element : 8"  # scripted group (container) (typed FeaturePython)
  n = 8
  ref = O_element
FEATURE [App::DocumentObjectGroupPython] P_element016  label="P_element : 005"  # scripted group (container) (typed FeaturePython)
  n = 1
  ref = P_element
FEATURE [App::DocumentObjectGroupPython] G4_DNA_G  # scripted group (container) (typed FeaturePython)
  Dunit = g/cm3
  Dvalue = 1
  Group = -> [H_element135,C_element145,N_element065,O_element127,P_element016]
  conduct = 2
  density = 1
  expand = 3
  formula = G4_DNA_G
  name = G4_DNA_G
  specific = 4
FEATURE [App::DocumentObjectGroupPython] H_element136  label="H_element : 083"  # scripted group (container) (typed FeaturePython)
  n = 10
  ref = H_element
FEATURE [App::DocumentObjectGroupPython] C_element146  label="C_element : 091"  # scripted group (container) (typed FeaturePython)
  n = 9
  ref = C_element
FEATURE [App::DocumentObjectGroupPython] N_element066  label="N_element : 038"  # scripted group (container) (typed FeaturePython)
  n = 3
  ref = N_element
FEATURE [App::DocumentObjectGroupPython] O_element128  label="O_element : 080"  # scripted group (container) (typed FeaturePython)
  n = 8
  ref = O_element
FEATURE [App::DocumentObjectGroupPython] P_element017  label="P_element : 006"  # scripted group (container) (typed FeaturePython)
  n = 1
  ref = P_element
FEATURE [App::DocumentObjectGroupPython] G4_DNA_C  # scripted group (container) (typed FeaturePython)
  Dunit = g/cm3
  Dvalue = 1
  Group = -> [H_element136,C_element146,N_element066,O_element128,P_element017]
  conduct = 2
  density = 1
  expand = 3
  formula = G4_DNA_C
  name = G4_DNA_C
  specific = 4
FEATURE [App::DocumentObjectGroupPython] H_element137  label="H_element : 084"  # scripted group (container) (typed FeaturePython)
  n = 9
  ref = H_element
FEATURE [App::DocumentObjectGroupPython] C_element147  label="C_element : 092"  # scripted group (container) (typed FeaturePython)
  n = 9
  ref = C_element
FEATURE [App::DocumentObjectGroupPython] N_element067  label="N_element : 039"  # scripted group (container) (typed FeaturePython)
  n = 2
  ref = N_element
FEATURE [App::DocumentObjectGroupPython] O_element129  label="O_element : 9"  # scripted group (container) (typed FeaturePython)
  n = 9
  ref = O_element
FEATURE [App::DocumentObjectGroupPython] P_element018  label="P_element : 007"  # scripted group (container) (typed FeaturePython)
  n = 1
  ref = P_element
FEATURE [App::DocumentObjectGroupPython] G4_DNA_U  # scripted group (container) (typed FeaturePython)
  Dunit = g/cm3
  Dvalue = 1
  Group = -> [H_element137,C_element147,N_element067,O_element129,P_element018]
  conduct = 2
  density = 1
  expand = 3
  formula = G4_DNA_U
  name = G4_DNA_U
  specific = 4
FEATURE [App::DocumentObjectGroupPython] H_element138  label="H_element : 085"  # scripted group (container) (typed FeaturePython)
  n = 11
  ref = H_element
FEATURE [App::DocumentObjectGroupPython] C_element148  label="C_element : 093"  # scripted group (container) (typed FeaturePython)
  n = 10
  ref = C_element
FEATURE [App::DocumentObjectGroupPython] N_element068  label="N_element : 040"  # scripted group (container) (typed FeaturePython)
  n = 2
  ref = N_element
FEATURE [App::DocumentObjectGroupPython] O_element130  label="O_element : 081"  # scripted group (container) (typed FeaturePython)
  n = 9
  ref = O_element
FEATURE [App::DocumentObjectGroupPython] P_element019  label="P_element : 008"  # scripted group (container) (typed FeaturePython)
  n = 1
  ref = P_element
FEATURE [App::DocumentObjectGroupPython] G4_DNA_MU  # scripted group (container) (typed FeaturePython)
  Dunit = g/cm3
  Dvalue = 1
  Group = -> [H_element138,C_element148,N_element068,O_element130,P_element019]
  conduct = 2
  density = 1
  expand = 3
  formula = G4_DNA_MU
  name = G4_DNA_MU
  specific = 4
FEATURE [App::DocumentObjectGroupPython] BioChemical  # scripted group (container) (typed FeaturePython)
  Group = -> [G4_CYTOSINE,G4_THYMINE,G4_URACIL,G4_DNA_ADENINE,G4_DNA_GUANINE,G4_DNA_CYTOSINE,G4_DNA_THYMINE,G4_DNA_URACIL,G4_DNA_ADENOSINE,G4_DNA_GUANOSINE,G4_DNA_CYTIDINE,G4_DNA_URIDINE,G4_DNA_METHYLURIDINE,G4_DNA_MONOPHOSPHATE,G4_DNA_A,G4_DNA_G,G4_DNA_C,G4_DNA_U,G4_DNA_MU]
FEATURE [App::DocumentObjectGroupPython] G4Materials  # scripted group (container) (typed FeaturePython)
  Group = -> [NIST,Element,HEP,Space,BioChemical]
  version = 1
FEATURE [App::DocumentObjectGroupPython] Geant4  # scripted group (container) (typed FeaturePython)
  Group = -> [G4Isotopes,G4Elements,G4Materials]
FEATURE [App::DocumentObjectGroupPython] Materials  # scripted group (container) (typed FeaturePython)
  Group = -> [Geant4]
FEATURE [Part::FeaturePython] GDMLBox_WorldBox  # WARN: FeaturePython — macro-defined, semantics opaque (R4)
  lunit = 2
  material = 5
  x = 100
  y = 100
  z = 100
FEATURE [Sketcher::SketchObject] Sketch
  FullyConstrained = false
  sketch-geometry (15):
    g0-g5: Circle x6 (B-spline internal-alignment scaffolding for g6; pole/knot coordinates omitted)
    g6: BSplineCurve PolesCount=7 KnotsCount=5 Degree=3 IsPeriodic=0
    g7-g10: GeomPoint x4 (B-spline internal-alignment scaffolding for g6; pole/knot coordinates omitted)
    g11: LineSegment StartX=-4.39557 StartY=8.39124 StartZ=0 EndX=-5.2662 EndY=10.5884 EndZ=0
    g12: LineSegment StartX=-5.2662 StartY=10.5884 StartZ=0 EndX=-7.82152 EndY=9.89481 EndZ=0
    g13: LineSegment StartX=-7.82152 StartY=9.89481 StartZ=0 EndX=-9.50073 EndY=7.63152 EndZ=0
    g14: ArcOfCircle CenterX=-7.8377 CenterY=5.34547 CenterZ=0 NormalX=0 NormalY=0 NormalZ=1 AngleXU=0 Radius=2.82696 StartAngle=4.84147 EndAngle=8.48291
  constraints (9):
    c: Weight(g0) = 1
    c: Equal(g0, g1-g5) x5
    c: InternalAlignment(g0-g5 -> g6) x6
    c: InternalAlignment(g7-g10 -> g6) x4
    c: Coincident(g11,g6)
    c: Coincident(g11,g12)
    c: Coincident(g12,g13)
    c: Coincident(g14,g13)
    c: Coincident(g14,g6)
FEATURE [Part::Extrusion] Extrude
  Base = -> Sketch
  Dir = (0,0,1)
  DirMode = 2
  FaceMakerClass = Part::FaceMakerBullseye
  LengthFwd = 10
  LengthRev = 0
  Placement = pos=(13,12,0) rot=(0,0,1;0rad)
  Solid = true
  Symmetric = false
  material = 1
FEATURE [Part::Mirroring] Part__Mirroring  label="mirror1"
  Base = (0,0,0)
  Normal = (1,0,0)
  Placement = pos=(0,0,0) rot=(0,0,1;0.523599rad)
  Source = -> Extrude
  material = 261
FEATURE [Part::Mirroring] Part__Mirroring002  label="mirror2"
  Base = (0,0,0)
  Normal = (0,1,0)
  Source = -> Part__Mirroring
FEATURE [App::Part] Part
  Group = -> [Sketch,Extrude,Part__Mirroring,Part__Mirroring002]
  Origin = -> Origin001
FEATURE [App::Part] worldVOL
  Group = -> [GDMLBox_WorldBox,Part]
  Origin = -> Origin
